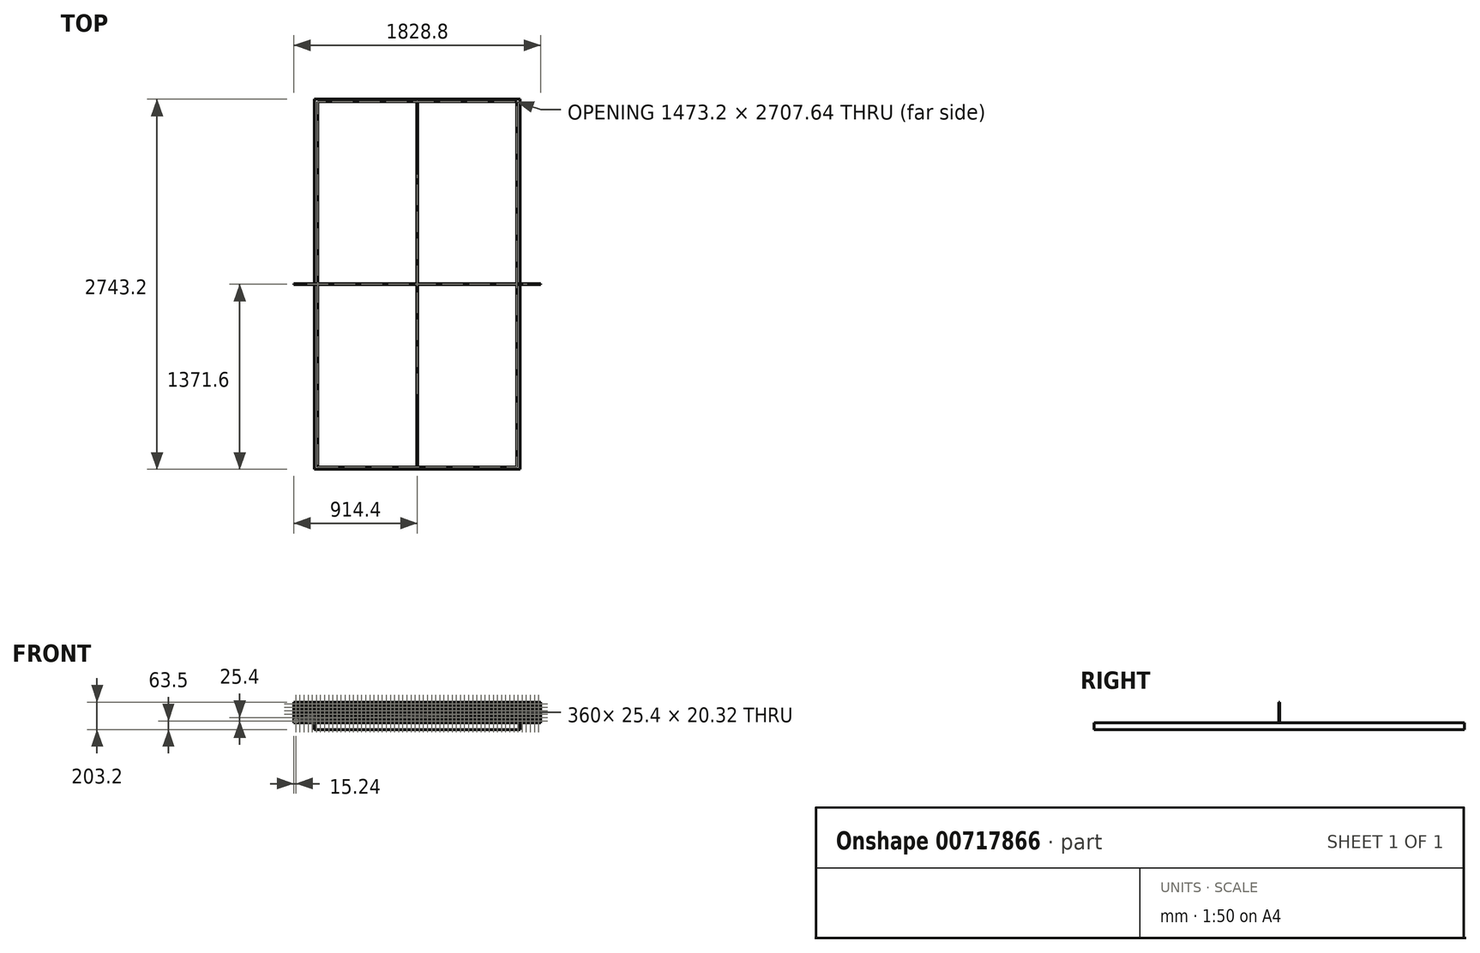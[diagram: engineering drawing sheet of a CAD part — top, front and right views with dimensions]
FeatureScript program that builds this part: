
annotation { "Feature Type Name" : "Feature", "Feature Type Description" : "" }
export const myFeature = defineFeature(function(context is Context, id is Id, definition is map)
    precondition{}
    {
        {
            var Q0;
            Q0=qCreatedBy(makeId("Top.planeOp"),FACE);
            var sketch = newSketch(context, id + "F0", { "sketchPlane" : qUnion([Q0])});
            skLineSegment(sketch, "E0.bottom", {"start": v(762, 1371.6) * mm, "end": v(-762, 1371.6) * mm});
            skLineSegment(sketch, "E0.top", {"start": v(762, -1371.6) * mm, "end": v(-762, -1371.6) * mm});
            skLineSegment(sketch, "E0.left", {"start": v(762, 1371.6) * mm, "end": v(762, -1371.6) * mm});
            skLineSegment(sketch, "E0.right", {"start": v(-762, 1371.6) * mm, "end": v(-762, -1371.6) * mm});
            skPoint(sketch, "E0.middle", {"position": v(0, 0) * mm});
            skSolve(sketch);
        }
        {
            var Q0;
            Q0=makeQuery(id+"F0.imprint","IMPRINT",FACE,{"disambiguationData":[TD([[makeQuery(id+"F0.imprint","IMPRINT",EDGE,{"derivedFrom":sQuery(id+"F0.wireOp",EDGE,"E0.bottom")}),1.0]])]});
            extrude(context, id + "F1", {"entities" : qUnion([Q0]), "endBound" : BoundingType.SYMMETRIC, "depth" : 50.8 * mm, "offsetDistance" : 25.4 * mm});
        }
        {
            var Q0;
            Q0=makeQuery(id+"F1.opExtrude","CAP_FACE",FACE,{"disambiguationData":[OSD([sQuery(id+"F0.wireOp",EDGE,"E0.bottom"),sQuery(id+"F0.wireOp",EDGE,"E0.top"),sQuery(id+"F0.wireOp",EDGE,"E0.left"),sQuery(id+"F0.wireOp",EDGE,"E0.right")])],"isStart":false});
            var sketch = newSketch(context, id + "F2", { "sketchPlane" : qUnion([Q0])});
            skLineSegment(sketch, "E1.bottom", {"start": v(914.4, 3.18) * mm, "end": v(-914.4, 3.18) * mm});
            skLineSegment(sketch, "E1.top", {"start": v(914.4, -3.18) * mm, "end": v(-914.4, -3.18) * mm});
            skLineSegment(sketch, "E1.left", {"start": v(914.4, 3.18) * mm, "end": v(914.4, -3.18) * mm});
            skLineSegment(sketch, "E1.right", {"start": v(-914.4, 3.18) * mm, "end": v(-914.4, -3.18) * mm});
            skPoint(sketch, "E1.middle", {"position": v(0, 0) * mm});
            skSolve(sketch);
        }
        {
            var Q0;
            {var subQ0=sQuery(id+"F2.wireOp",EDGE,"E1.right");Q0=makeQuery(id+"F2.imprint","IMPRINT",FACE,{"disambiguationData":[TD([[makeQuery(id+"F2.imprint","IMPRINT",EDGE,{"derivedFrom":subQ0}),1.0]])]});}
            var Q1;
            {var subQ0=sQuery(id+"F2.wireOp",EDGE,"E1.bottom");var subQ1=makeQuery(id+"F1.opExtrude","CAP_EDGE",EDGE,{"disambiguationData":[OSD([sQuery(id+"F0.wireOp",EDGE,"E0.left")])],"isStart":false});var subQ2=makeQuery(id+"F2.imprint","INTERSECT",VERTEX,{"derivedFrom":[subQ1,subQ0]});Q1=makeQuery(id+"F2.imprint","IMPRINT",FACE,{"disambiguationData":[TD([[makeQuery(id+"F2.imprint","IMPRINT",EDGE,{"disambiguationData":[TD([[subQ2,-1.0]])],"derivedFrom":subQ0}),1.0]])]});}
            var Q2;
            {var subQ0=sQuery(id+"F2.wireOp",EDGE,"E1.left");Q2=makeQuery(id+"F2.imprint","IMPRINT",FACE,{"disambiguationData":[TD([[makeQuery(id+"F2.imprint","IMPRINT",EDGE,{"derivedFrom":subQ0}),-1.0]])]});}
            extrude(context, id + "F3", {"entities" : qUnion([Q0, Q1, Q2]), "operationType" : NewBodyOperationType.ADD, "depth" : 152.4 * mm, "offsetDistance" : 25.4 * mm});
        }
        {
            var Q0;
            Q0=makeQuery(id+"F3.opExtrude","SWEPT_FACE",FACE,{"disambiguationData":[OSD([sQuery(id+"F2.wireOp",EDGE,"E1.top")])]});
            var sketch = newSketch(context, id + "F4", { "sketchPlane" : qUnion([Q0])});
            skLineSegment(sketch, "E2.bottom", {"start": v(-911.86, 175.26) * mm, "end": v(-886.46, 175.26) * mm});
            skLineSegment(sketch, "E2.top", {"start": v(-911.86, 154.94) * mm, "end": v(-886.46, 154.94) * mm});
            skLineSegment(sketch, "E2.left", {"start": v(-911.86, 175.26) * mm, "end": v(-911.86, 154.94) * mm});
            skLineSegment(sketch, "E3.1.0.3", {"start": v(-886.46, 175.26) * mm, "end": v(-886.46, 154.94) * mm});
            skLineSegment(sketch, "E4.1.0.0", {"start": v(-855.98, 175.26) * mm, "end": v(-855.98, 154.94) * mm});
            skLineSegment(sketch, "E4.1.0.1", {"start": v(-881.38, 175.26) * mm, "end": v(-855.98, 175.26) * mm});
            skLineSegment(sketch, "E4.1.0.2", {"start": v(-881.38, 175.26) * mm, "end": v(-881.38, 154.94) * mm});
            skLineSegment(sketch, "E4.1.0.3", {"start": v(-881.38, 154.94) * mm, "end": v(-855.98, 154.94) * mm});
            skLineSegment(sketch, "E4.2.0.0", {"start": v(-825.5, 175.26) * mm, "end": v(-825.5, 154.94) * mm});
            skLineSegment(sketch, "E4.2.0.1", {"start": v(-850.9, 175.26) * mm, "end": v(-825.5, 175.26) * mm});
            skLineSegment(sketch, "E4.2.0.2", {"start": v(-850.9, 175.26) * mm, "end": v(-850.9, 154.94) * mm});
            skLineSegment(sketch, "E4.2.0.3", {"start": v(-850.9, 154.94) * mm, "end": v(-825.5, 154.94) * mm});
            skLineSegment(sketch, "E4.3.0.0", {"start": v(-795.02, 175.26) * mm, "end": v(-795.02, 154.94) * mm});
            skLineSegment(sketch, "E4.3.0.1", {"start": v(-820.42, 175.26) * mm, "end": v(-795.02, 175.26) * mm});
            skLineSegment(sketch, "E4.3.0.2", {"start": v(-820.42, 175.26) * mm, "end": v(-820.42, 154.94) * mm});
            skLineSegment(sketch, "E4.3.0.3", {"start": v(-820.42, 154.94) * mm, "end": v(-795.02, 154.94) * mm});
            skLineSegment(sketch, "E4.4.0.0", {"start": v(-764.54, 175.26) * mm, "end": v(-764.54, 154.94) * mm});
            skLineSegment(sketch, "E4.4.0.1", {"start": v(-789.94, 175.26) * mm, "end": v(-764.54, 175.26) * mm});
            skLineSegment(sketch, "E4.4.0.2", {"start": v(-789.94, 175.26) * mm, "end": v(-789.94, 154.94) * mm});
            skLineSegment(sketch, "E4.4.0.3", {"start": v(-789.94, 154.94) * mm, "end": v(-764.54, 154.94) * mm});
            skLineSegment(sketch, "E4.5.0.0", {"start": v(-734.06, 175.26) * mm, "end": v(-734.06, 154.94) * mm});
            skLineSegment(sketch, "E4.5.0.1", {"start": v(-759.46, 175.26) * mm, "end": v(-734.06, 175.26) * mm});
            skLineSegment(sketch, "E4.5.0.2", {"start": v(-759.46, 175.26) * mm, "end": v(-759.46, 154.94) * mm});
            skLineSegment(sketch, "E4.5.0.3", {"start": v(-759.46, 154.94) * mm, "end": v(-734.06, 154.94) * mm});
            skLineSegment(sketch, "E4.6.0.0", {"start": v(-703.58, 175.26) * mm, "end": v(-703.58, 154.94) * mm});
            skLineSegment(sketch, "E4.6.0.1", {"start": v(-728.98, 175.26) * mm, "end": v(-703.58, 175.26) * mm});
            skLineSegment(sketch, "E4.6.0.2", {"start": v(-728.98, 175.26) * mm, "end": v(-728.98, 154.94) * mm});
            skLineSegment(sketch, "E4.6.0.3", {"start": v(-728.98, 154.94) * mm, "end": v(-703.58, 154.94) * mm});
            skLineSegment(sketch, "E4.7.0.0", {"start": v(-673.1, 175.26) * mm, "end": v(-673.1, 154.94) * mm});
            skLineSegment(sketch, "E4.7.0.1", {"start": v(-698.5, 175.26) * mm, "end": v(-673.1, 175.26) * mm});
            skLineSegment(sketch, "E4.7.0.2", {"start": v(-698.5, 175.26) * mm, "end": v(-698.5, 154.94) * mm});
            skLineSegment(sketch, "E4.7.0.3", {"start": v(-698.5, 154.94) * mm, "end": v(-673.1, 154.94) * mm});
            skLineSegment(sketch, "E4.8.0.0", {"start": v(-642.62, 175.26) * mm, "end": v(-642.62, 154.94) * mm});
            skLineSegment(sketch, "E4.8.0.1", {"start": v(-668.02, 175.26) * mm, "end": v(-642.62, 175.26) * mm});
            skLineSegment(sketch, "E4.8.0.2", {"start": v(-668.02, 175.26) * mm, "end": v(-668.02, 154.94) * mm});
            skLineSegment(sketch, "E4.8.0.3", {"start": v(-668.02, 154.94) * mm, "end": v(-642.62, 154.94) * mm});
            skLineSegment(sketch, "E4.9.0.0", {"start": v(-612.14, 175.26) * mm, "end": v(-612.14, 154.94) * mm});
            skLineSegment(sketch, "E4.9.0.1", {"start": v(-637.54, 175.26) * mm, "end": v(-612.14, 175.26) * mm});
            skLineSegment(sketch, "E4.9.0.2", {"start": v(-637.54, 175.26) * mm, "end": v(-637.54, 154.94) * mm});
            skLineSegment(sketch, "E4.9.0.3", {"start": v(-637.54, 154.94) * mm, "end": v(-612.14, 154.94) * mm});
            skLineSegment(sketch, "E4.10.0.0", {"start": v(-581.66, 175.26) * mm, "end": v(-581.66, 154.94) * mm});
            skLineSegment(sketch, "E4.10.0.1", {"start": v(-607.06, 175.26) * mm, "end": v(-581.66, 175.26) * mm});
            skLineSegment(sketch, "E4.10.0.2", {"start": v(-607.06, 175.26) * mm, "end": v(-607.06, 154.94) * mm});
            skLineSegment(sketch, "E4.10.0.3", {"start": v(-607.06, 154.94) * mm, "end": v(-581.66, 154.94) * mm});
            skLineSegment(sketch, "E4.11.0.0", {"start": v(-551.18, 175.26) * mm, "end": v(-551.18, 154.94) * mm});
            skLineSegment(sketch, "E4.11.0.1", {"start": v(-576.58, 175.26) * mm, "end": v(-551.18, 175.26) * mm});
            skLineSegment(sketch, "E4.11.0.2", {"start": v(-576.58, 175.26) * mm, "end": v(-576.58, 154.94) * mm});
            skLineSegment(sketch, "E4.11.0.3", {"start": v(-576.58, 154.94) * mm, "end": v(-551.18, 154.94) * mm});
            skLineSegment(sketch, "E4.12.0.0", {"start": v(-520.7, 175.26) * mm, "end": v(-520.7, 154.94) * mm});
            skLineSegment(sketch, "E4.12.0.1", {"start": v(-546.1, 175.26) * mm, "end": v(-520.7, 175.26) * mm});
            skLineSegment(sketch, "E4.12.0.2", {"start": v(-546.1, 175.26) * mm, "end": v(-546.1, 154.94) * mm});
            skLineSegment(sketch, "E4.12.0.3", {"start": v(-546.1, 154.94) * mm, "end": v(-520.7, 154.94) * mm});
            skLineSegment(sketch, "E4.13.0.0", {"start": v(-490.22, 175.26) * mm, "end": v(-490.22, 154.94) * mm});
            skLineSegment(sketch, "E4.13.0.1", {"start": v(-515.62, 175.26) * mm, "end": v(-490.22, 175.26) * mm});
            skLineSegment(sketch, "E4.13.0.2", {"start": v(-515.62, 175.26) * mm, "end": v(-515.62, 154.94) * mm});
            skLineSegment(sketch, "E4.13.0.3", {"start": v(-515.62, 154.94) * mm, "end": v(-490.22, 154.94) * mm});
            skLineSegment(sketch, "E4.14.0.0", {"start": v(-459.74, 175.26) * mm, "end": v(-459.74, 154.94) * mm});
            skLineSegment(sketch, "E4.14.0.1", {"start": v(-485.14, 175.26) * mm, "end": v(-459.74, 175.26) * mm});
            skLineSegment(sketch, "E4.14.0.2", {"start": v(-485.14, 175.26) * mm, "end": v(-485.14, 154.94) * mm});
            skLineSegment(sketch, "E4.14.0.3", {"start": v(-485.14, 154.94) * mm, "end": v(-459.74, 154.94) * mm});
            skLineSegment(sketch, "E4.15.0.0", {"start": v(-429.26, 175.26) * mm, "end": v(-429.26, 154.94) * mm});
            skLineSegment(sketch, "E4.15.0.1", {"start": v(-454.66, 175.26) * mm, "end": v(-429.26, 175.26) * mm});
            skLineSegment(sketch, "E4.15.0.2", {"start": v(-454.66, 175.26) * mm, "end": v(-454.66, 154.94) * mm});
            skLineSegment(sketch, "E4.15.0.3", {"start": v(-454.66, 154.94) * mm, "end": v(-429.26, 154.94) * mm});
            skLineSegment(sketch, "E4.16.0.0", {"start": v(-398.78, 175.26) * mm, "end": v(-398.78, 154.94) * mm});
            skLineSegment(sketch, "E4.16.0.1", {"start": v(-424.18, 175.26) * mm, "end": v(-398.78, 175.26) * mm});
            skLineSegment(sketch, "E4.16.0.2", {"start": v(-424.18, 175.26) * mm, "end": v(-424.18, 154.94) * mm});
            skLineSegment(sketch, "E4.16.0.3", {"start": v(-424.18, 154.94) * mm, "end": v(-398.78, 154.94) * mm});
            skLineSegment(sketch, "E4.17.0.0", {"start": v(-368.3, 175.26) * mm, "end": v(-368.3, 154.94) * mm});
            skLineSegment(sketch, "E4.17.0.1", {"start": v(-393.7, 175.26) * mm, "end": v(-368.3, 175.26) * mm});
            skLineSegment(sketch, "E4.17.0.2", {"start": v(-393.7, 175.26) * mm, "end": v(-393.7, 154.94) * mm});
            skLineSegment(sketch, "E4.17.0.3", {"start": v(-393.7, 154.94) * mm, "end": v(-368.3, 154.94) * mm});
            skLineSegment(sketch, "E4.18.0.0", {"start": v(-337.82, 175.26) * mm, "end": v(-337.82, 154.94) * mm});
            skLineSegment(sketch, "E4.18.0.1", {"start": v(-363.22, 175.26) * mm, "end": v(-337.82, 175.26) * mm});
            skLineSegment(sketch, "E4.18.0.2", {"start": v(-363.22, 175.26) * mm, "end": v(-363.22, 154.94) * mm});
            skLineSegment(sketch, "E4.18.0.3", {"start": v(-363.22, 154.94) * mm, "end": v(-337.82, 154.94) * mm});
            skLineSegment(sketch, "E4.19.0.0", {"start": v(-307.34, 175.26) * mm, "end": v(-307.34, 154.94) * mm});
            skLineSegment(sketch, "E4.19.0.1", {"start": v(-332.74, 175.26) * mm, "end": v(-307.34, 175.26) * mm});
            skLineSegment(sketch, "E4.19.0.2", {"start": v(-332.74, 175.26) * mm, "end": v(-332.74, 154.94) * mm});
            skLineSegment(sketch, "E4.19.0.3", {"start": v(-332.74, 154.94) * mm, "end": v(-307.34, 154.94) * mm});
            skLineSegment(sketch, "E4.20.0.0", {"start": v(-276.86, 175.26) * mm, "end": v(-276.86, 154.94) * mm});
            skLineSegment(sketch, "E4.20.0.1", {"start": v(-302.26, 175.26) * mm, "end": v(-276.86, 175.26) * mm});
            skLineSegment(sketch, "E4.20.0.2", {"start": v(-302.26, 175.26) * mm, "end": v(-302.26, 154.94) * mm});
            skLineSegment(sketch, "E4.20.0.3", {"start": v(-302.26, 154.94) * mm, "end": v(-276.86, 154.94) * mm});
            skLineSegment(sketch, "E4.21.0.0", {"start": v(-246.38, 175.26) * mm, "end": v(-246.38, 154.94) * mm});
            skLineSegment(sketch, "E4.21.0.1", {"start": v(-271.78, 175.26) * mm, "end": v(-246.38, 175.26) * mm});
            skLineSegment(sketch, "E4.21.0.2", {"start": v(-271.78, 175.26) * mm, "end": v(-271.78, 154.94) * mm});
            skLineSegment(sketch, "E4.21.0.3", {"start": v(-271.78, 154.94) * mm, "end": v(-246.38, 154.94) * mm});
            skLineSegment(sketch, "E4.22.0.0", {"start": v(-215.9, 175.26) * mm, "end": v(-215.9, 154.94) * mm});
            skLineSegment(sketch, "E4.22.0.1", {"start": v(-241.3, 175.26) * mm, "end": v(-215.9, 175.26) * mm});
            skLineSegment(sketch, "E4.22.0.2", {"start": v(-241.3, 175.26) * mm, "end": v(-241.3, 154.94) * mm});
            skLineSegment(sketch, "E4.22.0.3", {"start": v(-241.3, 154.94) * mm, "end": v(-215.9, 154.94) * mm});
            skLineSegment(sketch, "E4.23.0.0", {"start": v(-185.42, 175.26) * mm, "end": v(-185.42, 154.94) * mm});
            skLineSegment(sketch, "E4.23.0.1", {"start": v(-210.82, 175.26) * mm, "end": v(-185.42, 175.26) * mm});
            skLineSegment(sketch, "E4.23.0.2", {"start": v(-210.82, 175.26) * mm, "end": v(-210.82, 154.94) * mm});
            skLineSegment(sketch, "E4.23.0.3", {"start": v(-210.82, 154.94) * mm, "end": v(-185.42, 154.94) * mm});
            skLineSegment(sketch, "E4.24.0.0", {"start": v(-154.94, 175.26) * mm, "end": v(-154.94, 154.94) * mm});
            skLineSegment(sketch, "E4.24.0.1", {"start": v(-180.34, 175.26) * mm, "end": v(-154.94, 175.26) * mm});
            skLineSegment(sketch, "E4.24.0.2", {"start": v(-180.34, 175.26) * mm, "end": v(-180.34, 154.94) * mm});
            skLineSegment(sketch, "E4.24.0.3", {"start": v(-180.34, 154.94) * mm, "end": v(-154.94, 154.94) * mm});
            skLineSegment(sketch, "E4.25.0.0", {"start": v(-124.46, 175.26) * mm, "end": v(-124.46, 154.94) * mm});
            skLineSegment(sketch, "E4.25.0.1", {"start": v(-149.86, 175.26) * mm, "end": v(-124.46, 175.26) * mm});
            skLineSegment(sketch, "E4.25.0.2", {"start": v(-149.86, 175.26) * mm, "end": v(-149.86, 154.94) * mm});
            skLineSegment(sketch, "E4.25.0.3", {"start": v(-149.86, 154.94) * mm, "end": v(-124.46, 154.94) * mm});
            skLineSegment(sketch, "E4.26.0.0", {"start": v(-93.98, 175.26) * mm, "end": v(-93.98, 154.94) * mm});
            skLineSegment(sketch, "E4.26.0.1", {"start": v(-119.38, 175.26) * mm, "end": v(-93.98, 175.26) * mm});
            skLineSegment(sketch, "E4.26.0.2", {"start": v(-119.38, 175.26) * mm, "end": v(-119.38, 154.94) * mm});
            skLineSegment(sketch, "E4.26.0.3", {"start": v(-119.38, 154.94) * mm, "end": v(-93.98, 154.94) * mm});
            skLineSegment(sketch, "E4.27.0.0", {"start": v(-63.5, 175.26) * mm, "end": v(-63.5, 154.94) * mm});
            skLineSegment(sketch, "E4.27.0.1", {"start": v(-88.9, 175.26) * mm, "end": v(-63.5, 175.26) * mm});
            skLineSegment(sketch, "E4.27.0.2", {"start": v(-88.9, 175.26) * mm, "end": v(-88.9, 154.94) * mm});
            skLineSegment(sketch, "E4.27.0.3", {"start": v(-88.9, 154.94) * mm, "end": v(-63.5, 154.94) * mm});
            skLineSegment(sketch, "E4.28.0.0", {"start": v(-33.02, 175.26) * mm, "end": v(-33.02, 154.94) * mm});
            skLineSegment(sketch, "E4.28.0.1", {"start": v(-58.42, 175.26) * mm, "end": v(-33.02, 175.26) * mm});
            skLineSegment(sketch, "E4.28.0.2", {"start": v(-58.42, 175.26) * mm, "end": v(-58.42, 154.94) * mm});
            skLineSegment(sketch, "E4.28.0.3", {"start": v(-58.42, 154.94) * mm, "end": v(-33.02, 154.94) * mm});
            skLineSegment(sketch, "E4.29.0.0", {"start": v(-2.54, 175.26) * mm, "end": v(-2.54, 154.94) * mm});
            skLineSegment(sketch, "E4.29.0.1", {"start": v(-27.94, 175.26) * mm, "end": v(-2.54, 175.26) * mm});
            skLineSegment(sketch, "E4.29.0.2", {"start": v(-27.94, 175.26) * mm, "end": v(-27.94, 154.94) * mm});
            skLineSegment(sketch, "E4.29.0.3", {"start": v(-27.94, 154.94) * mm, "end": v(-2.54, 154.94) * mm});
            skLineSegment(sketch, "E4.30.0.0", {"start": v(27.94, 175.26) * mm, "end": v(27.94, 154.94) * mm});
            skLineSegment(sketch, "E4.30.0.1", {"start": v(2.54, 175.26) * mm, "end": v(27.94, 175.26) * mm});
            skLineSegment(sketch, "E4.30.0.2", {"start": v(2.54, 175.26) * mm, "end": v(2.54, 154.94) * mm});
            skLineSegment(sketch, "E4.30.0.3", {"start": v(2.54, 154.94) * mm, "end": v(27.94, 154.94) * mm});
            skLineSegment(sketch, "E4.31.0.0", {"start": v(58.42, 175.26) * mm, "end": v(58.42, 154.94) * mm});
            skLineSegment(sketch, "E4.31.0.1", {"start": v(33.02, 175.26) * mm, "end": v(58.42, 175.26) * mm});
            skLineSegment(sketch, "E4.31.0.2", {"start": v(33.02, 175.26) * mm, "end": v(33.02, 154.94) * mm});
            skLineSegment(sketch, "E4.31.0.3", {"start": v(33.02, 154.94) * mm, "end": v(58.42, 154.94) * mm});
            skLineSegment(sketch, "E4.32.0.0", {"start": v(88.9, 175.26) * mm, "end": v(88.9, 154.94) * mm});
            skLineSegment(sketch, "E4.32.0.1", {"start": v(63.5, 175.26) * mm, "end": v(88.9, 175.26) * mm});
            skLineSegment(sketch, "E4.32.0.2", {"start": v(63.5, 175.26) * mm, "end": v(63.5, 154.94) * mm});
            skLineSegment(sketch, "E4.32.0.3", {"start": v(63.5, 154.94) * mm, "end": v(88.9, 154.94) * mm});
            skLineSegment(sketch, "E4.33.0.0", {"start": v(119.38, 175.26) * mm, "end": v(119.38, 154.94) * mm});
            skLineSegment(sketch, "E4.33.0.1", {"start": v(93.98, 175.26) * mm, "end": v(119.38, 175.26) * mm});
            skLineSegment(sketch, "E4.33.0.2", {"start": v(93.98, 175.26) * mm, "end": v(93.98, 154.94) * mm});
            skLineSegment(sketch, "E4.33.0.3", {"start": v(93.98, 154.94) * mm, "end": v(119.38, 154.94) * mm});
            skLineSegment(sketch, "E4.34.0.0", {"start": v(149.86, 175.26) * mm, "end": v(149.86, 154.94) * mm});
            skLineSegment(sketch, "E4.34.0.1", {"start": v(124.46, 175.26) * mm, "end": v(149.86, 175.26) * mm});
            skLineSegment(sketch, "E4.34.0.2", {"start": v(124.46, 175.26) * mm, "end": v(124.46, 154.94) * mm});
            skLineSegment(sketch, "E4.34.0.3", {"start": v(124.46, 154.94) * mm, "end": v(149.86, 154.94) * mm});
            skLineSegment(sketch, "E4.35.0.0", {"start": v(180.34, 175.26) * mm, "end": v(180.34, 154.94) * mm});
            skLineSegment(sketch, "E4.35.0.1", {"start": v(154.94, 175.26) * mm, "end": v(180.34, 175.26) * mm});
            skLineSegment(sketch, "E4.35.0.2", {"start": v(154.94, 175.26) * mm, "end": v(154.94, 154.94) * mm});
            skLineSegment(sketch, "E4.35.0.3", {"start": v(154.94, 154.94) * mm, "end": v(180.34, 154.94) * mm});
            skLineSegment(sketch, "E4.36.0.0", {"start": v(210.82, 175.26) * mm, "end": v(210.82, 154.94) * mm});
            skLineSegment(sketch, "E4.36.0.1", {"start": v(185.42, 175.26) * mm, "end": v(210.82, 175.26) * mm});
            skLineSegment(sketch, "E4.36.0.2", {"start": v(185.42, 175.26) * mm, "end": v(185.42, 154.94) * mm});
            skLineSegment(sketch, "E4.36.0.3", {"start": v(185.42, 154.94) * mm, "end": v(210.82, 154.94) * mm});
            skLineSegment(sketch, "E4.37.0.0", {"start": v(241.3, 175.26) * mm, "end": v(241.3, 154.94) * mm});
            skLineSegment(sketch, "E4.37.0.1", {"start": v(215.9, 175.26) * mm, "end": v(241.3, 175.26) * mm});
            skLineSegment(sketch, "E4.37.0.2", {"start": v(215.9, 175.26) * mm, "end": v(215.9, 154.94) * mm});
            skLineSegment(sketch, "E4.37.0.3", {"start": v(215.9, 154.94) * mm, "end": v(241.3, 154.94) * mm});
            skLineSegment(sketch, "E4.38.0.0", {"start": v(271.78, 175.26) * mm, "end": v(271.78, 154.94) * mm});
            skLineSegment(sketch, "E4.38.0.1", {"start": v(246.38, 175.26) * mm, "end": v(271.78, 175.26) * mm});
            skLineSegment(sketch, "E4.38.0.2", {"start": v(246.38, 175.26) * mm, "end": v(246.38, 154.94) * mm});
            skLineSegment(sketch, "E4.38.0.3", {"start": v(246.38, 154.94) * mm, "end": v(271.78, 154.94) * mm});
            skLineSegment(sketch, "E4.39.0.0", {"start": v(302.26, 175.26) * mm, "end": v(302.26, 154.94) * mm});
            skLineSegment(sketch, "E4.39.0.1", {"start": v(276.86, 175.26) * mm, "end": v(302.26, 175.26) * mm});
            skLineSegment(sketch, "E4.39.0.2", {"start": v(276.86, 175.26) * mm, "end": v(276.86, 154.94) * mm});
            skLineSegment(sketch, "E4.39.0.3", {"start": v(276.86, 154.94) * mm, "end": v(302.26, 154.94) * mm});
            skLineSegment(sketch, "E4.40.0.0", {"start": v(332.74, 175.26) * mm, "end": v(332.74, 154.94) * mm});
            skLineSegment(sketch, "E4.40.0.1", {"start": v(307.34, 175.26) * mm, "end": v(332.74, 175.26) * mm});
            skLineSegment(sketch, "E4.40.0.2", {"start": v(307.34, 175.26) * mm, "end": v(307.34, 154.94) * mm});
            skLineSegment(sketch, "E4.40.0.3", {"start": v(307.34, 154.94) * mm, "end": v(332.74, 154.94) * mm});
            skLineSegment(sketch, "E4.41.0.0", {"start": v(363.22, 175.26) * mm, "end": v(363.22, 154.94) * mm});
            skLineSegment(sketch, "E4.41.0.1", {"start": v(337.82, 175.26) * mm, "end": v(363.22, 175.26) * mm});
            skLineSegment(sketch, "E4.41.0.2", {"start": v(337.82, 175.26) * mm, "end": v(337.82, 154.94) * mm});
            skLineSegment(sketch, "E4.41.0.3", {"start": v(337.82, 154.94) * mm, "end": v(363.22, 154.94) * mm});
            skLineSegment(sketch, "E4.42.0.0", {"start": v(393.7, 175.26) * mm, "end": v(393.7, 154.94) * mm});
            skLineSegment(sketch, "E4.42.0.1", {"start": v(368.3, 175.26) * mm, "end": v(393.7, 175.26) * mm});
            skLineSegment(sketch, "E4.42.0.2", {"start": v(368.3, 175.26) * mm, "end": v(368.3, 154.94) * mm});
            skLineSegment(sketch, "E4.42.0.3", {"start": v(368.3, 154.94) * mm, "end": v(393.7, 154.94) * mm});
            skLineSegment(sketch, "E4.43.0.0", {"start": v(424.18, 175.26) * mm, "end": v(424.18, 154.94) * mm});
            skLineSegment(sketch, "E4.43.0.1", {"start": v(398.78, 175.26) * mm, "end": v(424.18, 175.26) * mm});
            skLineSegment(sketch, "E4.43.0.2", {"start": v(398.78, 175.26) * mm, "end": v(398.78, 154.94) * mm});
            skLineSegment(sketch, "E4.43.0.3", {"start": v(398.78, 154.94) * mm, "end": v(424.18, 154.94) * mm});
            skLineSegment(sketch, "E4.44.0.0", {"start": v(454.66, 175.26) * mm, "end": v(454.66, 154.94) * mm});
            skLineSegment(sketch, "E4.44.0.1", {"start": v(429.26, 175.26) * mm, "end": v(454.66, 175.26) * mm});
            skLineSegment(sketch, "E4.44.0.2", {"start": v(429.26, 175.26) * mm, "end": v(429.26, 154.94) * mm});
            skLineSegment(sketch, "E4.44.0.3", {"start": v(429.26, 154.94) * mm, "end": v(454.66, 154.94) * mm});
            skLineSegment(sketch, "E4.45.0.0", {"start": v(485.14, 175.26) * mm, "end": v(485.14, 154.94) * mm});
            skLineSegment(sketch, "E4.45.0.1", {"start": v(459.74, 175.26) * mm, "end": v(485.14, 175.26) * mm});
            skLineSegment(sketch, "E4.45.0.2", {"start": v(459.74, 175.26) * mm, "end": v(459.74, 154.94) * mm});
            skLineSegment(sketch, "E4.45.0.3", {"start": v(459.74, 154.94) * mm, "end": v(485.14, 154.94) * mm});
            skLineSegment(sketch, "E4.46.0.0", {"start": v(515.62, 175.26) * mm, "end": v(515.62, 154.94) * mm});
            skLineSegment(sketch, "E4.46.0.1", {"start": v(490.22, 175.26) * mm, "end": v(515.62, 175.26) * mm});
            skLineSegment(sketch, "E4.46.0.2", {"start": v(490.22, 175.26) * mm, "end": v(490.22, 154.94) * mm});
            skLineSegment(sketch, "E4.46.0.3", {"start": v(490.22, 154.94) * mm, "end": v(515.62, 154.94) * mm});
            skLineSegment(sketch, "E4.47.0.0", {"start": v(546.1, 175.26) * mm, "end": v(546.1, 154.94) * mm});
            skLineSegment(sketch, "E4.47.0.1", {"start": v(520.7, 175.26) * mm, "end": v(546.1, 175.26) * mm});
            skLineSegment(sketch, "E4.47.0.2", {"start": v(520.7, 175.26) * mm, "end": v(520.7, 154.94) * mm});
            skLineSegment(sketch, "E4.47.0.3", {"start": v(520.7, 154.94) * mm, "end": v(546.1, 154.94) * mm});
            skLineSegment(sketch, "E4.48.0.0", {"start": v(576.58, 175.26) * mm, "end": v(576.58, 154.94) * mm});
            skLineSegment(sketch, "E4.48.0.1", {"start": v(551.18, 175.26) * mm, "end": v(576.58, 175.26) * mm});
            skLineSegment(sketch, "E4.48.0.2", {"start": v(551.18, 175.26) * mm, "end": v(551.18, 154.94) * mm});
            skLineSegment(sketch, "E4.48.0.3", {"start": v(551.18, 154.94) * mm, "end": v(576.58, 154.94) * mm});
            skLineSegment(sketch, "E4.49.0.0", {"start": v(607.06, 175.26) * mm, "end": v(607.06, 154.94) * mm});
            skLineSegment(sketch, "E4.49.0.1", {"start": v(581.66, 175.26) * mm, "end": v(607.06, 175.26) * mm});
            skLineSegment(sketch, "E4.49.0.2", {"start": v(581.66, 175.26) * mm, "end": v(581.66, 154.94) * mm});
            skLineSegment(sketch, "E4.49.0.3", {"start": v(581.66, 154.94) * mm, "end": v(607.06, 154.94) * mm});
            skLineSegment(sketch, "E4.50.0.0", {"start": v(637.54, 175.26) * mm, "end": v(637.54, 154.94) * mm});
            skLineSegment(sketch, "E4.50.0.1", {"start": v(612.14, 175.26) * mm, "end": v(637.54, 175.26) * mm});
            skLineSegment(sketch, "E4.50.0.2", {"start": v(612.14, 175.26) * mm, "end": v(612.14, 154.94) * mm});
            skLineSegment(sketch, "E4.50.0.3", {"start": v(612.14, 154.94) * mm, "end": v(637.54, 154.94) * mm});
            skLineSegment(sketch, "E4.51.0.0", {"start": v(668.02, 175.26) * mm, "end": v(668.02, 154.94) * mm});
            skLineSegment(sketch, "E4.51.0.1", {"start": v(642.62, 175.26) * mm, "end": v(668.02, 175.26) * mm});
            skLineSegment(sketch, "E4.51.0.2", {"start": v(642.62, 175.26) * mm, "end": v(642.62, 154.94) * mm});
            skLineSegment(sketch, "E4.51.0.3", {"start": v(642.62, 154.94) * mm, "end": v(668.02, 154.94) * mm});
            skLineSegment(sketch, "E4.52.0.0", {"start": v(698.5, 175.26) * mm, "end": v(698.5, 154.94) * mm});
            skLineSegment(sketch, "E4.52.0.1", {"start": v(673.1, 175.26) * mm, "end": v(698.5, 175.26) * mm});
            skLineSegment(sketch, "E4.52.0.2", {"start": v(673.1, 175.26) * mm, "end": v(673.1, 154.94) * mm});
            skLineSegment(sketch, "E4.52.0.3", {"start": v(673.1, 154.94) * mm, "end": v(698.5, 154.94) * mm});
            skLineSegment(sketch, "E4.53.0.0", {"start": v(728.98, 175.26) * mm, "end": v(728.98, 154.94) * mm});
            skLineSegment(sketch, "E4.53.0.1", {"start": v(703.58, 175.26) * mm, "end": v(728.98, 175.26) * mm});
            skLineSegment(sketch, "E4.53.0.2", {"start": v(703.58, 175.26) * mm, "end": v(703.58, 154.94) * mm});
            skLineSegment(sketch, "E4.53.0.3", {"start": v(703.58, 154.94) * mm, "end": v(728.98, 154.94) * mm});
            skLineSegment(sketch, "E4.54.0.0", {"start": v(759.46, 175.26) * mm, "end": v(759.46, 154.94) * mm});
            skLineSegment(sketch, "E4.54.0.1", {"start": v(734.06, 175.26) * mm, "end": v(759.46, 175.26) * mm});
            skLineSegment(sketch, "E4.54.0.2", {"start": v(734.06, 175.26) * mm, "end": v(734.06, 154.94) * mm});
            skLineSegment(sketch, "E4.54.0.3", {"start": v(734.06, 154.94) * mm, "end": v(759.46, 154.94) * mm});
            skLineSegment(sketch, "E4.55.0.0", {"start": v(789.94, 175.26) * mm, "end": v(789.94, 154.94) * mm});
            skLineSegment(sketch, "E4.55.0.1", {"start": v(764.54, 175.26) * mm, "end": v(789.94, 175.26) * mm});
            skLineSegment(sketch, "E4.55.0.2", {"start": v(764.54, 175.26) * mm, "end": v(764.54, 154.94) * mm});
            skLineSegment(sketch, "E4.55.0.3", {"start": v(764.54, 154.94) * mm, "end": v(789.94, 154.94) * mm});
            skLineSegment(sketch, "E4.56.0.0", {"start": v(820.42, 175.26) * mm, "end": v(820.42, 154.94) * mm});
            skLineSegment(sketch, "E4.56.0.1", {"start": v(795.02, 175.26) * mm, "end": v(820.42, 175.26) * mm});
            skLineSegment(sketch, "E4.56.0.2", {"start": v(795.02, 175.26) * mm, "end": v(795.02, 154.94) * mm});
            skLineSegment(sketch, "E4.56.0.3", {"start": v(795.02, 154.94) * mm, "end": v(820.42, 154.94) * mm});
            skLineSegment(sketch, "E4.57.0.0", {"start": v(850.9, 175.26) * mm, "end": v(850.9, 154.94) * mm});
            skLineSegment(sketch, "E4.57.0.1", {"start": v(825.5, 175.26) * mm, "end": v(850.9, 175.26) * mm});
            skLineSegment(sketch, "E4.57.0.2", {"start": v(825.5, 175.26) * mm, "end": v(825.5, 154.94) * mm});
            skLineSegment(sketch, "E4.57.0.3", {"start": v(825.5, 154.94) * mm, "end": v(850.9, 154.94) * mm});
            skLineSegment(sketch, "E4.58.0.0", {"start": v(881.38, 175.26) * mm, "end": v(881.38, 154.94) * mm});
            skLineSegment(sketch, "E4.58.0.1", {"start": v(855.98, 175.26) * mm, "end": v(881.38, 175.26) * mm});
            skLineSegment(sketch, "E4.58.0.2", {"start": v(855.98, 175.26) * mm, "end": v(855.98, 154.94) * mm});
            skLineSegment(sketch, "E4.58.0.3", {"start": v(855.98, 154.94) * mm, "end": v(881.38, 154.94) * mm});
            skLineSegment(sketch, "E4.59.0.0", {"start": v(911.86, 175.26) * mm, "end": v(911.86, 154.94) * mm});
            skLineSegment(sketch, "E4.59.0.1", {"start": v(886.46, 175.26) * mm, "end": v(911.86, 175.26) * mm});
            skLineSegment(sketch, "E4.59.0.2", {"start": v(886.46, 175.26) * mm, "end": v(886.46, 154.94) * mm});
            skLineSegment(sketch, "E4.59.0.3", {"start": v(886.46, 154.94) * mm, "end": v(911.86, 154.94) * mm});
            skLineSegment(sketch, "E4.direction1", {"start": v(-886.46, 154.94) * mm, "end": v(-855.98, 154.94) * mm, "construction": true});
            skLineSegment(sketch, "E5.0.1.0", {"start": v(886.46, 129.54) * mm, "end": v(911.86, 129.54) * mm});
            skLineSegment(sketch, "E5.0.1.1", {"start": v(911.86, 149.86) * mm, "end": v(911.86, 129.54) * mm});
            skLineSegment(sketch, "E5.0.1.2", {"start": v(886.46, 149.86) * mm, "end": v(911.86, 149.86) * mm});
            skLineSegment(sketch, "E5.0.1.3", {"start": v(886.46, 149.86) * mm, "end": v(886.46, 129.54) * mm});
            skLineSegment(sketch, "E5.0.1.4", {"start": v(881.38, 149.86) * mm, "end": v(881.38, 129.54) * mm});
            skLineSegment(sketch, "E5.0.1.5", {"start": v(855.98, 149.86) * mm, "end": v(881.38, 149.86) * mm});
            skLineSegment(sketch, "E5.0.1.6", {"start": v(855.98, 129.54) * mm, "end": v(881.38, 129.54) * mm});
            skLineSegment(sketch, "E5.0.1.7", {"start": v(855.98, 149.86) * mm, "end": v(855.98, 129.54) * mm});
            skLineSegment(sketch, "E5.0.1.8", {"start": v(520.7, 129.54) * mm, "end": v(546.1, 129.54) * mm});
            skLineSegment(sketch, "E5.0.1.9", {"start": v(398.78, 129.54) * mm, "end": v(424.18, 129.54) * mm});
            skLineSegment(sketch, "E5.0.1.10", {"start": v(820.42, 149.86) * mm, "end": v(820.42, 129.54) * mm});
            skLineSegment(sketch, "E5.0.1.11", {"start": v(642.62, 129.54) * mm, "end": v(668.02, 129.54) * mm});
            skLineSegment(sketch, "E5.0.1.12", {"start": v(764.54, 129.54) * mm, "end": v(789.94, 129.54) * mm});
            skLineSegment(sketch, "E5.0.1.13", {"start": v(698.5, 149.86) * mm, "end": v(698.5, 129.54) * mm});
            skLineSegment(sketch, "E5.0.1.14", {"start": v(576.58, 149.86) * mm, "end": v(576.58, 129.54) * mm});
            skLineSegment(sketch, "E5.0.1.15", {"start": v(454.66, 149.86) * mm, "end": v(454.66, 129.54) * mm});
            skLineSegment(sketch, "E5.0.1.16", {"start": v(795.02, 149.86) * mm, "end": v(820.42, 149.86) * mm});
            skLineSegment(sketch, "E5.0.1.17", {"start": v(673.1, 149.86) * mm, "end": v(698.5, 149.86) * mm});
            skLineSegment(sketch, "E5.0.1.18", {"start": v(551.18, 149.86) * mm, "end": v(576.58, 149.86) * mm});
            skLineSegment(sketch, "E5.0.1.19", {"start": v(429.26, 149.86) * mm, "end": v(454.66, 149.86) * mm});
            skLineSegment(sketch, "E5.0.1.20", {"start": v(795.02, 149.86) * mm, "end": v(795.02, 129.54) * mm});
            skLineSegment(sketch, "E5.0.1.21", {"start": v(673.1, 149.86) * mm, "end": v(673.1, 129.54) * mm});
            skLineSegment(sketch, "E5.0.1.22", {"start": v(551.18, 149.86) * mm, "end": v(551.18, 129.54) * mm});
            skLineSegment(sketch, "E5.0.1.23", {"start": v(429.26, 149.86) * mm, "end": v(429.26, 129.54) * mm});
            skLineSegment(sketch, "E5.0.1.24", {"start": v(795.02, 129.54) * mm, "end": v(820.42, 129.54) * mm});
            skLineSegment(sketch, "E5.0.1.25", {"start": v(673.1, 129.54) * mm, "end": v(698.5, 129.54) * mm});
            skLineSegment(sketch, "E5.0.1.26", {"start": v(551.18, 129.54) * mm, "end": v(576.58, 129.54) * mm});
            skLineSegment(sketch, "E5.0.1.27", {"start": v(429.26, 129.54) * mm, "end": v(454.66, 129.54) * mm});
            skLineSegment(sketch, "E5.0.1.28", {"start": v(850.9, 149.86) * mm, "end": v(850.9, 129.54) * mm});
            skLineSegment(sketch, "E5.0.1.29", {"start": v(728.98, 149.86) * mm, "end": v(728.98, 129.54) * mm});
            skLineSegment(sketch, "E5.0.1.30", {"start": v(607.06, 149.86) * mm, "end": v(607.06, 129.54) * mm});
            skLineSegment(sketch, "E5.0.1.31", {"start": v(485.14, 149.86) * mm, "end": v(485.14, 129.54) * mm});
            skLineSegment(sketch, "E5.0.1.32", {"start": v(825.5, 149.86) * mm, "end": v(850.9, 149.86) * mm});
            skLineSegment(sketch, "E5.0.1.33", {"start": v(703.58, 149.86) * mm, "end": v(728.98, 149.86) * mm});
            skLineSegment(sketch, "E5.0.1.34", {"start": v(581.66, 149.86) * mm, "end": v(607.06, 149.86) * mm});
            skLineSegment(sketch, "E5.0.1.35", {"start": v(459.74, 149.86) * mm, "end": v(485.14, 149.86) * mm});
            skLineSegment(sketch, "E5.0.1.36", {"start": v(825.5, 149.86) * mm, "end": v(825.5, 129.54) * mm});
            skLineSegment(sketch, "E5.0.1.37", {"start": v(703.58, 149.86) * mm, "end": v(703.58, 129.54) * mm});
            skLineSegment(sketch, "E5.0.1.38", {"start": v(581.66, 149.86) * mm, "end": v(581.66, 129.54) * mm});
            skLineSegment(sketch, "E5.0.1.39", {"start": v(459.74, 149.86) * mm, "end": v(459.74, 129.54) * mm});
            skLineSegment(sketch, "E5.0.1.40", {"start": v(581.66, 129.54) * mm, "end": v(607.06, 129.54) * mm});
            skLineSegment(sketch, "E5.0.1.41", {"start": v(459.74, 129.54) * mm, "end": v(485.14, 129.54) * mm});
            skLineSegment(sketch, "E5.0.1.42", {"start": v(825.5, 129.54) * mm, "end": v(850.9, 129.54) * mm});
            skLineSegment(sketch, "E5.0.1.43", {"start": v(703.58, 129.54) * mm, "end": v(728.98, 129.54) * mm});
            skLineSegment(sketch, "E5.0.1.44", {"start": v(637.54, 149.86) * mm, "end": v(637.54, 129.54) * mm});
            skLineSegment(sketch, "E5.0.1.45", {"start": v(515.62, 149.86) * mm, "end": v(515.62, 129.54) * mm});
            skLineSegment(sketch, "E5.0.1.46", {"start": v(393.7, 149.86) * mm, "end": v(393.7, 129.54) * mm});
            skLineSegment(sketch, "E5.0.1.47", {"start": v(759.46, 149.86) * mm, "end": v(759.46, 129.54) * mm});
            skLineSegment(sketch, "E5.0.1.48", {"start": v(612.14, 149.86) * mm, "end": v(637.54, 149.86) * mm});
            skLineSegment(sketch, "E5.0.1.49", {"start": v(490.22, 149.86) * mm, "end": v(515.62, 149.86) * mm});
            skLineSegment(sketch, "E5.0.1.50", {"start": v(368.3, 149.86) * mm, "end": v(393.7, 149.86) * mm});
            skLineSegment(sketch, "E5.0.1.51", {"start": v(734.06, 149.86) * mm, "end": v(759.46, 149.86) * mm});
            skLineSegment(sketch, "E5.0.1.52", {"start": v(612.14, 149.86) * mm, "end": v(612.14, 129.54) * mm});
            skLineSegment(sketch, "E5.0.1.53", {"start": v(490.22, 149.86) * mm, "end": v(490.22, 129.54) * mm});
            skLineSegment(sketch, "E5.0.1.54", {"start": v(734.06, 149.86) * mm, "end": v(734.06, 129.54) * mm});
            skLineSegment(sketch, "E5.0.1.55", {"start": v(612.14, 129.54) * mm, "end": v(637.54, 129.54) * mm});
            skLineSegment(sketch, "E5.0.1.56", {"start": v(490.22, 129.54) * mm, "end": v(515.62, 129.54) * mm});
            skLineSegment(sketch, "E5.0.1.57", {"start": v(368.3, 129.54) * mm, "end": v(393.7, 129.54) * mm});
            skLineSegment(sketch, "E5.0.1.58", {"start": v(734.06, 129.54) * mm, "end": v(759.46, 129.54) * mm});
            skLineSegment(sketch, "E5.0.1.59", {"start": v(764.54, 149.86) * mm, "end": v(789.94, 149.86) * mm});
            skLineSegment(sketch, "E5.0.1.60", {"start": v(642.62, 149.86) * mm, "end": v(668.02, 149.86) * mm});
            skLineSegment(sketch, "E5.0.1.61", {"start": v(520.7, 149.86) * mm, "end": v(546.1, 149.86) * mm});
            skLineSegment(sketch, "E5.0.1.62", {"start": v(398.78, 149.86) * mm, "end": v(424.18, 149.86) * mm});
            skLineSegment(sketch, "E5.0.1.63", {"start": v(668.02, 149.86) * mm, "end": v(668.02, 129.54) * mm});
            skLineSegment(sketch, "E5.0.1.64", {"start": v(546.1, 149.86) * mm, "end": v(546.1, 129.54) * mm});
            skLineSegment(sketch, "E5.0.1.65", {"start": v(424.18, 149.86) * mm, "end": v(424.18, 129.54) * mm});
            skLineSegment(sketch, "E5.0.1.66", {"start": v(789.94, 149.86) * mm, "end": v(789.94, 129.54) * mm});
            skLineSegment(sketch, "E5.0.1.67", {"start": v(764.54, 149.86) * mm, "end": v(764.54, 129.54) * mm});
            skLineSegment(sketch, "E5.0.1.68", {"start": v(642.62, 149.86) * mm, "end": v(642.62, 129.54) * mm});
            skLineSegment(sketch, "E5.0.1.69", {"start": v(520.7, 149.86) * mm, "end": v(520.7, 129.54) * mm});
            skLineSegment(sketch, "E5.0.1.70", {"start": v(398.78, 149.86) * mm, "end": v(398.78, 129.54) * mm});
            skLineSegment(sketch, "E5.0.1.71", {"start": v(332.74, 149.86) * mm, "end": v(332.74, 129.54) * mm});
            skLineSegment(sketch, "E5.0.1.72", {"start": v(210.82, 149.86) * mm, "end": v(210.82, 129.54) * mm});
            skLineSegment(sketch, "E5.0.1.73", {"start": v(88.9, 149.86) * mm, "end": v(88.9, 129.54) * mm});
            skLineSegment(sketch, "E5.0.1.74", {"start": v(33.02, 129.54) * mm, "end": v(58.42, 129.54) * mm});
            skLineSegment(sketch, "E5.0.1.75", {"start": v(154.94, 129.54) * mm, "end": v(180.34, 129.54) * mm});
            skLineSegment(sketch, "E5.0.1.76", {"start": v(276.86, 129.54) * mm, "end": v(302.26, 129.54) * mm});
            skLineSegment(sketch, "E5.0.1.77", {"start": v(307.34, 149.86) * mm, "end": v(332.74, 149.86) * mm});
            skLineSegment(sketch, "E5.0.1.78", {"start": v(185.42, 149.86) * mm, "end": v(210.82, 149.86) * mm});
            skLineSegment(sketch, "E5.0.1.79", {"start": v(63.5, 149.86) * mm, "end": v(88.9, 149.86) * mm});
            skLineSegment(sketch, "E5.0.1.80", {"start": v(307.34, 149.86) * mm, "end": v(307.34, 129.54) * mm});
            skLineSegment(sketch, "E5.0.1.81", {"start": v(185.42, 149.86) * mm, "end": v(185.42, 129.54) * mm});
            skLineSegment(sketch, "E5.0.1.82", {"start": v(63.5, 149.86) * mm, "end": v(63.5, 129.54) * mm});
            skLineSegment(sketch, "E5.0.1.83", {"start": v(307.34, 129.54) * mm, "end": v(332.74, 129.54) * mm});
            skLineSegment(sketch, "E5.0.1.84", {"start": v(185.42, 129.54) * mm, "end": v(210.82, 129.54) * mm});
            skLineSegment(sketch, "E5.0.1.85", {"start": v(63.5, 129.54) * mm, "end": v(88.9, 129.54) * mm});
            skLineSegment(sketch, "E5.0.1.86", {"start": v(363.22, 149.86) * mm, "end": v(363.22, 129.54) * mm});
            skLineSegment(sketch, "E5.0.1.87", {"start": v(241.3, 149.86) * mm, "end": v(241.3, 129.54) * mm});
            skLineSegment(sketch, "E5.0.1.88", {"start": v(119.38, 149.86) * mm, "end": v(119.38, 129.54) * mm});
            skLineSegment(sketch, "E5.0.1.89", {"start": v(337.82, 149.86) * mm, "end": v(363.22, 149.86) * mm});
            skLineSegment(sketch, "E5.0.1.90", {"start": v(215.9, 149.86) * mm, "end": v(241.3, 149.86) * mm});
            skLineSegment(sketch, "E5.0.1.91", {"start": v(93.98, 149.86) * mm, "end": v(119.38, 149.86) * mm});
            skLineSegment(sketch, "E5.0.1.92", {"start": v(337.82, 149.86) * mm, "end": v(337.82, 129.54) * mm});
            skLineSegment(sketch, "E5.0.1.93", {"start": v(215.9, 149.86) * mm, "end": v(215.9, 129.54) * mm});
            skLineSegment(sketch, "E5.0.1.94", {"start": v(93.98, 149.86) * mm, "end": v(93.98, 129.54) * mm});
            skLineSegment(sketch, "E5.0.1.95", {"start": v(93.98, 129.54) * mm, "end": v(119.38, 129.54) * mm});
            skLineSegment(sketch, "E5.0.1.96", {"start": v(337.82, 129.54) * mm, "end": v(363.22, 129.54) * mm});
            skLineSegment(sketch, "E5.0.1.97", {"start": v(215.9, 129.54) * mm, "end": v(241.3, 129.54) * mm});
            skLineSegment(sketch, "E5.0.1.98", {"start": v(149.86, 149.86) * mm, "end": v(149.86, 129.54) * mm});
            skLineSegment(sketch, "E5.0.1.99", {"start": v(27.94, 149.86) * mm, "end": v(27.94, 129.54) * mm});
            skLineSegment(sketch, "E5.0.1.100", {"start": v(271.78, 149.86) * mm, "end": v(271.78, 129.54) * mm});
            skLineSegment(sketch, "E5.0.1.101", {"start": v(124.46, 149.86) * mm, "end": v(149.86, 149.86) * mm});
            skLineSegment(sketch, "E5.0.1.102", {"start": v(2.54, 149.86) * mm, "end": v(27.94, 149.86) * mm});
            skLineSegment(sketch, "E5.0.1.103", {"start": v(246.38, 149.86) * mm, "end": v(271.78, 149.86) * mm});
            skLineSegment(sketch, "E5.0.1.104", {"start": v(124.46, 149.86) * mm, "end": v(124.46, 129.54) * mm});
            skLineSegment(sketch, "E5.0.1.105", {"start": v(2.54, 149.86) * mm, "end": v(2.54, 129.54) * mm});
            skLineSegment(sketch, "E5.0.1.106", {"start": v(368.3, 149.86) * mm, "end": v(368.3, 129.54) * mm});
            skLineSegment(sketch, "E5.0.1.107", {"start": v(246.38, 149.86) * mm, "end": v(246.38, 129.54) * mm});
            skLineSegment(sketch, "E5.0.1.108", {"start": v(124.46, 129.54) * mm, "end": v(149.86, 129.54) * mm});
            skLineSegment(sketch, "E5.0.1.109", {"start": v(2.54, 129.54) * mm, "end": v(27.94, 129.54) * mm});
            skLineSegment(sketch, "E5.0.1.110", {"start": v(246.38, 129.54) * mm, "end": v(271.78, 129.54) * mm});
            skLineSegment(sketch, "E5.0.1.111", {"start": v(276.86, 149.86) * mm, "end": v(302.26, 149.86) * mm});
            skLineSegment(sketch, "E5.0.1.112", {"start": v(154.94, 149.86) * mm, "end": v(180.34, 149.86) * mm});
            skLineSegment(sketch, "E5.0.1.113", {"start": v(33.02, 149.86) * mm, "end": v(58.42, 149.86) * mm});
            skLineSegment(sketch, "E5.0.1.114", {"start": v(180.34, 149.86) * mm, "end": v(180.34, 129.54) * mm});
            skLineSegment(sketch, "E5.0.1.115", {"start": v(58.42, 149.86) * mm, "end": v(58.42, 129.54) * mm});
            skLineSegment(sketch, "E5.0.1.116", {"start": v(302.26, 149.86) * mm, "end": v(302.26, 129.54) * mm});
            skLineSegment(sketch, "E5.0.1.117", {"start": v(276.86, 149.86) * mm, "end": v(276.86, 129.54) * mm});
            skLineSegment(sketch, "E5.0.1.118", {"start": v(154.94, 149.86) * mm, "end": v(154.94, 129.54) * mm});
            skLineSegment(sketch, "E5.0.1.119", {"start": v(33.02, 149.86) * mm, "end": v(33.02, 129.54) * mm});
            skLineSegment(sketch, "E5.0.1.120", {"start": v(-520.7, 149.86) * mm, "end": v(-520.7, 129.54) * mm});
            skLineSegment(sketch, "E5.0.1.121", {"start": v(-332.74, 129.54) * mm, "end": v(-307.34, 129.54) * mm});
            skLineSegment(sketch, "E5.0.1.122", {"start": v(-398.78, 149.86) * mm, "end": v(-398.78, 129.54) * mm});
            skLineSegment(sketch, "E5.0.1.123", {"start": v(-33.02, 149.86) * mm, "end": v(-33.02, 129.54) * mm});
            skLineSegment(sketch, "E5.0.1.124", {"start": v(-88.9, 129.54) * mm, "end": v(-63.5, 129.54) * mm});
            skLineSegment(sketch, "E5.0.1.125", {"start": v(-698.5, 129.54) * mm, "end": v(-673.1, 129.54) * mm});
            skLineSegment(sketch, "E5.0.1.126", {"start": v(-454.66, 129.54) * mm, "end": v(-429.26, 129.54) * mm});
            skLineSegment(sketch, "E5.0.1.127", {"start": v(-642.62, 149.86) * mm, "end": v(-642.62, 129.54) * mm});
            skLineSegment(sketch, "E5.0.1.128", {"start": v(-764.54, 149.86) * mm, "end": v(-764.54, 129.54) * mm});
            skLineSegment(sketch, "E5.0.1.129", {"start": v(-154.94, 149.86) * mm, "end": v(-154.94, 129.54) * mm});
            skLineSegment(sketch, "E5.0.1.130", {"start": v(-210.82, 129.54) * mm, "end": v(-185.42, 129.54) * mm});
            skLineSegment(sketch, "E5.0.1.131", {"start": v(-576.58, 129.54) * mm, "end": v(-551.18, 129.54) * mm});
            skLineSegment(sketch, "E5.0.1.132", {"start": v(-276.86, 149.86) * mm, "end": v(-276.86, 129.54) * mm});
            skLineSegment(sketch, "E5.0.1.133", {"start": v(-886.46, 129.54) * mm, "end": v(-855.98, 129.54) * mm, "construction": true});
            skLineSegment(sketch, "E5.0.1.134", {"start": v(-180.34, 149.86) * mm, "end": v(-154.94, 149.86) * mm});
            skLineSegment(sketch, "E5.0.1.135", {"start": v(-302.26, 149.86) * mm, "end": v(-276.86, 149.86) * mm});
            skLineSegment(sketch, "E5.0.1.136", {"start": v(-424.18, 149.86) * mm, "end": v(-398.78, 149.86) * mm});
            skLineSegment(sketch, "E5.0.1.137", {"start": v(-546.1, 149.86) * mm, "end": v(-520.7, 149.86) * mm});
            skLineSegment(sketch, "E5.0.1.138", {"start": v(-58.42, 149.86) * mm, "end": v(-33.02, 149.86) * mm});
            skLineSegment(sketch, "E5.0.1.139", {"start": v(-668.02, 149.86) * mm, "end": v(-642.62, 149.86) * mm});
            skLineSegment(sketch, "E5.0.1.140", {"start": v(-789.94, 149.86) * mm, "end": v(-764.54, 149.86) * mm});
            skLineSegment(sketch, "E5.0.1.141", {"start": v(-58.42, 149.86) * mm, "end": v(-58.42, 129.54) * mm});
            skLineSegment(sketch, "E5.0.1.142", {"start": v(-668.02, 149.86) * mm, "end": v(-668.02, 129.54) * mm});
            skLineSegment(sketch, "E5.0.1.143", {"start": v(-789.94, 149.86) * mm, "end": v(-789.94, 129.54) * mm});
            skLineSegment(sketch, "E5.0.1.144", {"start": v(-180.34, 149.86) * mm, "end": v(-180.34, 129.54) * mm});
            skLineSegment(sketch, "E5.0.1.145", {"start": v(-302.26, 149.86) * mm, "end": v(-302.26, 129.54) * mm});
            skLineSegment(sketch, "E5.0.1.146", {"start": v(-424.18, 149.86) * mm, "end": v(-424.18, 129.54) * mm});
            skLineSegment(sketch, "E5.0.1.147", {"start": v(-546.1, 149.86) * mm, "end": v(-546.1, 129.54) * mm});
            skLineSegment(sketch, "E5.0.1.148", {"start": v(-668.02, 129.54) * mm, "end": v(-642.62, 129.54) * mm});
            skLineSegment(sketch, "E5.0.1.149", {"start": v(-789.94, 129.54) * mm, "end": v(-764.54, 129.54) * mm});
            skLineSegment(sketch, "E5.0.1.150", {"start": v(-180.34, 129.54) * mm, "end": v(-154.94, 129.54) * mm});
            skLineSegment(sketch, "E5.0.1.151", {"start": v(-302.26, 129.54) * mm, "end": v(-276.86, 129.54) * mm});
            skLineSegment(sketch, "E5.0.1.152", {"start": v(-424.18, 129.54) * mm, "end": v(-398.78, 129.54) * mm});
            skLineSegment(sketch, "E5.0.1.153", {"start": v(-546.1, 129.54) * mm, "end": v(-520.7, 129.54) * mm});
            skLineSegment(sketch, "E5.0.1.154", {"start": v(-58.42, 129.54) * mm, "end": v(-33.02, 129.54) * mm});
            skLineSegment(sketch, "E5.0.1.155", {"start": v(-612.14, 149.86) * mm, "end": v(-612.14, 129.54) * mm});
            skLineSegment(sketch, "E5.0.1.156", {"start": v(-734.06, 149.86) * mm, "end": v(-734.06, 129.54) * mm});
            skLineSegment(sketch, "E5.0.1.157", {"start": v(-124.46, 149.86) * mm, "end": v(-124.46, 129.54) * mm});
            skLineSegment(sketch, "E5.0.1.158", {"start": v(-246.38, 149.86) * mm, "end": v(-246.38, 129.54) * mm});
            skLineSegment(sketch, "E5.0.1.159", {"start": v(-368.3, 149.86) * mm, "end": v(-368.3, 129.54) * mm});
            skLineSegment(sketch, "E5.0.1.160", {"start": v(-490.22, 149.86) * mm, "end": v(-490.22, 129.54) * mm});
            skLineSegment(sketch, "E5.0.1.161", {"start": v(-2.54, 149.86) * mm, "end": v(-2.54, 129.54) * mm});
            skLineSegment(sketch, "E5.0.1.162", {"start": v(-637.54, 149.86) * mm, "end": v(-612.14, 149.86) * mm});
            skLineSegment(sketch, "E5.0.1.163", {"start": v(-759.46, 149.86) * mm, "end": v(-734.06, 149.86) * mm});
            skLineSegment(sketch, "E5.0.1.164", {"start": v(-149.86, 149.86) * mm, "end": v(-124.46, 149.86) * mm});
            skLineSegment(sketch, "E5.0.1.165", {"start": v(-271.78, 149.86) * mm, "end": v(-246.38, 149.86) * mm});
            skLineSegment(sketch, "E5.0.1.166", {"start": v(-393.7, 149.86) * mm, "end": v(-368.3, 149.86) * mm});
            skLineSegment(sketch, "E5.0.1.167", {"start": v(-515.62, 149.86) * mm, "end": v(-490.22, 149.86) * mm});
            skLineSegment(sketch, "E5.0.1.168", {"start": v(-27.94, 149.86) * mm, "end": v(-2.54, 149.86) * mm});
            skLineSegment(sketch, "E5.0.1.169", {"start": v(-637.54, 149.86) * mm, "end": v(-637.54, 129.54) * mm});
            skLineSegment(sketch, "E5.0.1.170", {"start": v(-759.46, 149.86) * mm, "end": v(-759.46, 129.54) * mm});
            skLineSegment(sketch, "E5.0.1.171", {"start": v(-149.86, 149.86) * mm, "end": v(-149.86, 129.54) * mm});
            skLineSegment(sketch, "E5.0.1.172", {"start": v(-271.78, 149.86) * mm, "end": v(-271.78, 129.54) * mm});
            skLineSegment(sketch, "E5.0.1.173", {"start": v(-393.7, 149.86) * mm, "end": v(-393.7, 129.54) * mm});
            skLineSegment(sketch, "E5.0.1.174", {"start": v(-515.62, 149.86) * mm, "end": v(-515.62, 129.54) * mm});
            skLineSegment(sketch, "E5.0.1.175", {"start": v(-27.94, 149.86) * mm, "end": v(-27.94, 129.54) * mm});
            skLineSegment(sketch, "E5.0.1.176", {"start": v(-393.7, 129.54) * mm, "end": v(-368.3, 129.54) * mm});
            skLineSegment(sketch, "E5.0.1.177", {"start": v(-515.62, 129.54) * mm, "end": v(-490.22, 129.54) * mm});
            skLineSegment(sketch, "E5.0.1.178", {"start": v(-637.54, 129.54) * mm, "end": v(-612.14, 129.54) * mm});
            skLineSegment(sketch, "E5.0.1.179", {"start": v(-759.46, 129.54) * mm, "end": v(-734.06, 129.54) * mm});
            skLineSegment(sketch, "E5.0.1.180", {"start": v(-27.94, 129.54) * mm, "end": v(-2.54, 129.54) * mm});
            skLineSegment(sketch, "E5.0.1.181", {"start": v(-149.86, 129.54) * mm, "end": v(-124.46, 129.54) * mm});
            skLineSegment(sketch, "E5.0.1.182", {"start": v(-271.78, 129.54) * mm, "end": v(-246.38, 129.54) * mm});
            skLineSegment(sketch, "E5.0.1.183", {"start": v(-337.82, 149.86) * mm, "end": v(-337.82, 129.54) * mm});
            skLineSegment(sketch, "E5.0.1.184", {"start": v(-459.74, 149.86) * mm, "end": v(-459.74, 129.54) * mm});
            skLineSegment(sketch, "E5.0.1.185", {"start": v(-581.66, 149.86) * mm, "end": v(-581.66, 129.54) * mm});
            skLineSegment(sketch, "E5.0.1.186", {"start": v(-703.58, 149.86) * mm, "end": v(-703.58, 129.54) * mm});
            skLineSegment(sketch, "E5.0.1.187", {"start": v(-93.98, 149.86) * mm, "end": v(-93.98, 129.54) * mm});
            skLineSegment(sketch, "E5.0.1.188", {"start": v(-215.9, 149.86) * mm, "end": v(-215.9, 129.54) * mm});
            skLineSegment(sketch, "E5.0.1.189", {"start": v(-363.22, 149.86) * mm, "end": v(-337.82, 149.86) * mm});
            skLineSegment(sketch, "E5.0.1.190", {"start": v(-485.14, 149.86) * mm, "end": v(-459.74, 149.86) * mm});
            skLineSegment(sketch, "E5.0.1.191", {"start": v(-607.06, 149.86) * mm, "end": v(-581.66, 149.86) * mm});
            skLineSegment(sketch, "E5.0.1.192", {"start": v(-728.98, 149.86) * mm, "end": v(-703.58, 149.86) * mm});
            skLineSegment(sketch, "E5.0.1.193", {"start": v(-119.38, 149.86) * mm, "end": v(-93.98, 149.86) * mm});
            skLineSegment(sketch, "E5.0.1.194", {"start": v(-241.3, 149.86) * mm, "end": v(-215.9, 149.86) * mm});
            skLineSegment(sketch, "E5.0.1.195", {"start": v(-363.22, 149.86) * mm, "end": v(-363.22, 129.54) * mm});
            skLineSegment(sketch, "E5.0.1.196", {"start": v(-485.14, 149.86) * mm, "end": v(-485.14, 129.54) * mm});
            skLineSegment(sketch, "E5.0.1.197", {"start": v(-607.06, 149.86) * mm, "end": v(-607.06, 129.54) * mm});
            skLineSegment(sketch, "E5.0.1.198", {"start": v(-728.98, 149.86) * mm, "end": v(-728.98, 129.54) * mm});
            skLineSegment(sketch, "E5.0.1.199", {"start": v(-119.38, 149.86) * mm, "end": v(-119.38, 129.54) * mm});
            skLineSegment(sketch, "E5.0.1.200", {"start": v(-241.3, 149.86) * mm, "end": v(-241.3, 129.54) * mm});
            skLineSegment(sketch, "E5.0.1.201", {"start": v(-363.22, 129.54) * mm, "end": v(-337.82, 129.54) * mm});
            skLineSegment(sketch, "E5.0.1.202", {"start": v(-485.14, 129.54) * mm, "end": v(-459.74, 129.54) * mm});
            skLineSegment(sketch, "E5.0.1.203", {"start": v(-607.06, 129.54) * mm, "end": v(-581.66, 129.54) * mm});
            skLineSegment(sketch, "E5.0.1.204", {"start": v(-728.98, 129.54) * mm, "end": v(-703.58, 129.54) * mm});
            skLineSegment(sketch, "E5.0.1.205", {"start": v(-119.38, 129.54) * mm, "end": v(-93.98, 129.54) * mm});
            skLineSegment(sketch, "E5.0.1.206", {"start": v(-241.3, 129.54) * mm, "end": v(-215.9, 129.54) * mm});
            skLineSegment(sketch, "E5.0.1.207", {"start": v(-698.5, 149.86) * mm, "end": v(-673.1, 149.86) * mm});
            skLineSegment(sketch, "E5.0.1.208", {"start": v(-210.82, 149.86) * mm, "end": v(-185.42, 149.86) * mm});
            skLineSegment(sketch, "E5.0.1.209", {"start": v(-332.74, 149.86) * mm, "end": v(-307.34, 149.86) * mm});
            skLineSegment(sketch, "E5.0.1.210", {"start": v(-454.66, 149.86) * mm, "end": v(-429.26, 149.86) * mm});
            skLineSegment(sketch, "E5.0.1.211", {"start": v(-576.58, 149.86) * mm, "end": v(-551.18, 149.86) * mm});
            skLineSegment(sketch, "E5.0.1.212", {"start": v(-88.9, 149.86) * mm, "end": v(-63.5, 149.86) * mm});
            skLineSegment(sketch, "E5.0.1.213", {"start": v(-820.42, 149.86) * mm, "end": v(-795.02, 149.86) * mm});
            skLineSegment(sketch, "E5.0.1.214", {"start": v(-820.42, 149.86) * mm, "end": v(-820.42, 129.54) * mm});
            skLineSegment(sketch, "E5.0.1.215", {"start": v(-820.42, 129.54) * mm, "end": v(-795.02, 129.54) * mm});
            skLineSegment(sketch, "E5.0.1.216", {"start": v(-911.86, 149.86) * mm, "end": v(-886.46, 149.86) * mm});
            skLineSegment(sketch, "E5.0.1.217", {"start": v(-911.86, 129.54) * mm, "end": v(-886.46, 129.54) * mm});
            skLineSegment(sketch, "E5.0.1.218", {"start": v(-911.86, 149.86) * mm, "end": v(-911.86, 129.54) * mm});
            skLineSegment(sketch, "E5.0.1.219", {"start": v(-886.46, 149.86) * mm, "end": v(-886.46, 129.54) * mm});
            skLineSegment(sketch, "E5.0.1.220", {"start": v(-855.98, 149.86) * mm, "end": v(-855.98, 129.54) * mm});
            skLineSegment(sketch, "E5.0.1.221", {"start": v(-881.38, 149.86) * mm, "end": v(-855.98, 149.86) * mm});
            skLineSegment(sketch, "E5.0.1.222", {"start": v(-881.38, 149.86) * mm, "end": v(-881.38, 129.54) * mm});
            skLineSegment(sketch, "E5.0.1.223", {"start": v(-825.5, 149.86) * mm, "end": v(-825.5, 129.54) * mm});
            skLineSegment(sketch, "E5.0.1.224", {"start": v(-850.9, 149.86) * mm, "end": v(-825.5, 149.86) * mm});
            skLineSegment(sketch, "E5.0.1.225", {"start": v(-307.34, 149.86) * mm, "end": v(-307.34, 129.54) * mm});
            skLineSegment(sketch, "E5.0.1.226", {"start": v(-850.9, 149.86) * mm, "end": v(-850.9, 129.54) * mm});
            skLineSegment(sketch, "E5.0.1.227", {"start": v(-429.26, 149.86) * mm, "end": v(-429.26, 129.54) * mm});
            skLineSegment(sketch, "E5.0.1.228", {"start": v(-551.18, 149.86) * mm, "end": v(-551.18, 129.54) * mm});
            skLineSegment(sketch, "E5.0.1.229", {"start": v(-673.1, 149.86) * mm, "end": v(-673.1, 129.54) * mm});
            skLineSegment(sketch, "E5.0.1.230", {"start": v(-850.9, 129.54) * mm, "end": v(-825.5, 129.54) * mm});
            skLineSegment(sketch, "E5.0.1.231", {"start": v(-63.5, 149.86) * mm, "end": v(-63.5, 129.54) * mm});
            skLineSegment(sketch, "E5.0.1.232", {"start": v(-185.42, 149.86) * mm, "end": v(-185.42, 129.54) * mm});
            skLineSegment(sketch, "E5.0.1.233", {"start": v(-795.02, 149.86) * mm, "end": v(-795.02, 129.54) * mm});
            skLineSegment(sketch, "E5.0.1.234", {"start": v(-698.5, 149.86) * mm, "end": v(-698.5, 129.54) * mm});
            skLineSegment(sketch, "E5.0.1.235", {"start": v(-210.82, 149.86) * mm, "end": v(-210.82, 129.54) * mm});
            skLineSegment(sketch, "E5.0.1.236", {"start": v(-332.74, 149.86) * mm, "end": v(-332.74, 129.54) * mm});
            skLineSegment(sketch, "E5.0.1.237", {"start": v(-454.66, 149.86) * mm, "end": v(-454.66, 129.54) * mm});
            skLineSegment(sketch, "E5.0.1.238", {"start": v(-576.58, 149.86) * mm, "end": v(-576.58, 129.54) * mm});
            skLineSegment(sketch, "E5.0.1.239", {"start": v(-88.9, 149.86) * mm, "end": v(-88.9, 129.54) * mm});
            skLineSegment(sketch, "E5.0.1.240", {"start": v(-881.38, 129.54) * mm, "end": v(-855.98, 129.54) * mm});
            skLineSegment(sketch, "E5.direction1", {"start": v(886.46, 154.94) * mm, "end": v(966.22, 154.94) * mm, "construction": true});
            skLineSegment(sketch, "E5.direction2", {"start": v(886.46, 154.94) * mm, "end": v(886.46, 129.54) * mm, "construction": true});
            skLineSegment(sketch, "E6.0.0.2", {"start": v(886.46, 104.14) * mm, "end": v(911.86, 104.14) * mm});
            skLineSegment(sketch, "E6.3.0.2", {"start": v(911.86, 124.46) * mm, "end": v(911.86, 104.14) * mm});
            skLineSegment(sketch, "E6.6.0.2", {"start": v(886.46, 124.46) * mm, "end": v(911.86, 124.46) * mm});
            skLineSegment(sketch, "E6.9.0.2", {"start": v(886.46, 124.46) * mm, "end": v(886.46, 104.14) * mm});
            skLineSegment(sketch, "E6.12.0.2", {"start": v(881.38, 124.46) * mm, "end": v(881.38, 104.14) * mm});
            skLineSegment(sketch, "E6.15.0.2", {"start": v(855.98, 124.46) * mm, "end": v(881.38, 124.46) * mm});
            skLineSegment(sketch, "E6.18.0.2", {"start": v(855.98, 104.14) * mm, "end": v(881.38, 104.14) * mm});
            skLineSegment(sketch, "E6.21.0.2", {"start": v(855.98, 124.46) * mm, "end": v(855.98, 104.14) * mm});
            skLineSegment(sketch, "E6.24.0.2", {"start": v(520.7, 104.14) * mm, "end": v(546.1, 104.14) * mm});
            skLineSegment(sketch, "E6.27.0.2", {"start": v(398.78, 104.14) * mm, "end": v(424.18, 104.14) * mm});
            skLineSegment(sketch, "E6.30.0.2", {"start": v(820.42, 124.46) * mm, "end": v(820.42, 104.14) * mm});
            skLineSegment(sketch, "E6.33.0.2", {"start": v(642.62, 104.14) * mm, "end": v(668.02, 104.14) * mm});
            skLineSegment(sketch, "E6.36.0.2", {"start": v(764.54, 104.14) * mm, "end": v(789.94, 104.14) * mm});
            skLineSegment(sketch, "E6.39.0.2", {"start": v(698.5, 124.46) * mm, "end": v(698.5, 104.14) * mm});
            skLineSegment(sketch, "E6.42.0.2", {"start": v(576.58, 124.46) * mm, "end": v(576.58, 104.14) * mm});
            skLineSegment(sketch, "E6.45.0.2", {"start": v(454.66, 124.46) * mm, "end": v(454.66, 104.14) * mm});
            skLineSegment(sketch, "E6.48.0.2", {"start": v(795.02, 124.46) * mm, "end": v(820.42, 124.46) * mm});
            skLineSegment(sketch, "E6.51.0.2", {"start": v(673.1, 124.46) * mm, "end": v(698.5, 124.46) * mm});
            skLineSegment(sketch, "E6.54.0.2", {"start": v(551.18, 124.46) * mm, "end": v(576.58, 124.46) * mm});
            skLineSegment(sketch, "E6.57.0.2", {"start": v(429.26, 124.46) * mm, "end": v(454.66, 124.46) * mm});
            skLineSegment(sketch, "E6.60.0.2", {"start": v(795.02, 124.46) * mm, "end": v(795.02, 104.14) * mm});
            skLineSegment(sketch, "E6.63.0.2", {"start": v(673.1, 124.46) * mm, "end": v(673.1, 104.14) * mm});
            skLineSegment(sketch, "E6.66.0.2", {"start": v(551.18, 124.46) * mm, "end": v(551.18, 104.14) * mm});
            skLineSegment(sketch, "E6.69.0.2", {"start": v(429.26, 124.46) * mm, "end": v(429.26, 104.14) * mm});
            skLineSegment(sketch, "E6.72.0.2", {"start": v(795.02, 104.14) * mm, "end": v(820.42, 104.14) * mm});
            skLineSegment(sketch, "E6.75.0.2", {"start": v(673.1, 104.14) * mm, "end": v(698.5, 104.14) * mm});
            skLineSegment(sketch, "E6.78.0.2", {"start": v(551.18, 104.14) * mm, "end": v(576.58, 104.14) * mm});
            skLineSegment(sketch, "E6.81.0.2", {"start": v(429.26, 104.14) * mm, "end": v(454.66, 104.14) * mm});
            skLineSegment(sketch, "E6.84.0.2", {"start": v(850.9, 124.46) * mm, "end": v(850.9, 104.14) * mm});
            skLineSegment(sketch, "E6.87.0.2", {"start": v(728.98, 124.46) * mm, "end": v(728.98, 104.14) * mm});
            skLineSegment(sketch, "E6.90.0.2", {"start": v(607.06, 124.46) * mm, "end": v(607.06, 104.14) * mm});
            skLineSegment(sketch, "E6.93.0.2", {"start": v(485.14, 124.46) * mm, "end": v(485.14, 104.14) * mm});
            skLineSegment(sketch, "E6.96.0.2", {"start": v(825.5, 124.46) * mm, "end": v(850.9, 124.46) * mm});
            skLineSegment(sketch, "E6.99.0.2", {"start": v(703.58, 124.46) * mm, "end": v(728.98, 124.46) * mm});
            skLineSegment(sketch, "E6.102.0.2", {"start": v(581.66, 124.46) * mm, "end": v(607.06, 124.46) * mm});
            skLineSegment(sketch, "E6.105.0.2", {"start": v(459.74, 124.46) * mm, "end": v(485.14, 124.46) * mm});
            skLineSegment(sketch, "E6.108.0.2", {"start": v(825.5, 124.46) * mm, "end": v(825.5, 104.14) * mm});
            skLineSegment(sketch, "E6.111.0.2", {"start": v(703.58, 124.46) * mm, "end": v(703.58, 104.14) * mm});
            skLineSegment(sketch, "E6.114.0.2", {"start": v(581.66, 124.46) * mm, "end": v(581.66, 104.14) * mm});
            skLineSegment(sketch, "E6.117.0.2", {"start": v(459.74, 124.46) * mm, "end": v(459.74, 104.14) * mm});
            skLineSegment(sketch, "E6.120.0.2", {"start": v(581.66, 104.14) * mm, "end": v(607.06, 104.14) * mm});
            skLineSegment(sketch, "E6.123.0.2", {"start": v(459.74, 104.14) * mm, "end": v(485.14, 104.14) * mm});
            skLineSegment(sketch, "E6.126.0.2", {"start": v(825.5, 104.14) * mm, "end": v(850.9, 104.14) * mm});
            skLineSegment(sketch, "E6.129.0.2", {"start": v(703.58, 104.14) * mm, "end": v(728.98, 104.14) * mm});
            skLineSegment(sketch, "E6.132.0.2", {"start": v(637.54, 124.46) * mm, "end": v(637.54, 104.14) * mm});
            skLineSegment(sketch, "E6.135.0.2", {"start": v(515.62, 124.46) * mm, "end": v(515.62, 104.14) * mm});
            skLineSegment(sketch, "E6.138.0.2", {"start": v(393.7, 124.46) * mm, "end": v(393.7, 104.14) * mm});
            skLineSegment(sketch, "E6.141.0.2", {"start": v(759.46, 124.46) * mm, "end": v(759.46, 104.14) * mm});
            skLineSegment(sketch, "E6.144.0.2", {"start": v(612.14, 124.46) * mm, "end": v(637.54, 124.46) * mm});
            skLineSegment(sketch, "E6.147.0.2", {"start": v(490.22, 124.46) * mm, "end": v(515.62, 124.46) * mm});
            skLineSegment(sketch, "E6.150.0.2", {"start": v(368.3, 124.46) * mm, "end": v(393.7, 124.46) * mm});
            skLineSegment(sketch, "E6.153.0.2", {"start": v(734.06, 124.46) * mm, "end": v(759.46, 124.46) * mm});
            skLineSegment(sketch, "E6.156.0.2", {"start": v(612.14, 124.46) * mm, "end": v(612.14, 104.14) * mm});
            skLineSegment(sketch, "E6.159.0.2", {"start": v(490.22, 124.46) * mm, "end": v(490.22, 104.14) * mm});
            skLineSegment(sketch, "E6.162.0.2", {"start": v(734.06, 124.46) * mm, "end": v(734.06, 104.14) * mm});
            skLineSegment(sketch, "E6.165.0.2", {"start": v(612.14, 104.14) * mm, "end": v(637.54, 104.14) * mm});
            skLineSegment(sketch, "E6.168.0.2", {"start": v(490.22, 104.14) * mm, "end": v(515.62, 104.14) * mm});
            skLineSegment(sketch, "E6.171.0.2", {"start": v(368.3, 104.14) * mm, "end": v(393.7, 104.14) * mm});
            skLineSegment(sketch, "E6.174.0.2", {"start": v(734.06, 104.14) * mm, "end": v(759.46, 104.14) * mm});
            skLineSegment(sketch, "E6.177.0.2", {"start": v(764.54, 124.46) * mm, "end": v(789.94, 124.46) * mm});
            skLineSegment(sketch, "E6.180.0.2", {"start": v(642.62, 124.46) * mm, "end": v(668.02, 124.46) * mm});
            skLineSegment(sketch, "E6.183.0.2", {"start": v(520.7, 124.46) * mm, "end": v(546.1, 124.46) * mm});
            skLineSegment(sketch, "E6.186.0.2", {"start": v(398.78, 124.46) * mm, "end": v(424.18, 124.46) * mm});
            skLineSegment(sketch, "E6.189.0.2", {"start": v(668.02, 124.46) * mm, "end": v(668.02, 104.14) * mm});
            skLineSegment(sketch, "E6.192.0.2", {"start": v(546.1, 124.46) * mm, "end": v(546.1, 104.14) * mm});
            skLineSegment(sketch, "E6.195.0.2", {"start": v(424.18, 124.46) * mm, "end": v(424.18, 104.14) * mm});
            skLineSegment(sketch, "E6.198.0.2", {"start": v(789.94, 124.46) * mm, "end": v(789.94, 104.14) * mm});
            skLineSegment(sketch, "E6.201.0.2", {"start": v(764.54, 124.46) * mm, "end": v(764.54, 104.14) * mm});
            skLineSegment(sketch, "E6.204.0.2", {"start": v(642.62, 124.46) * mm, "end": v(642.62, 104.14) * mm});
            skLineSegment(sketch, "E6.207.0.2", {"start": v(520.7, 124.46) * mm, "end": v(520.7, 104.14) * mm});
            skLineSegment(sketch, "E6.210.0.2", {"start": v(398.78, 124.46) * mm, "end": v(398.78, 104.14) * mm});
            skLineSegment(sketch, "E6.213.0.2", {"start": v(332.74, 124.46) * mm, "end": v(332.74, 104.14) * mm});
            skLineSegment(sketch, "E6.216.0.2", {"start": v(210.82, 124.46) * mm, "end": v(210.82, 104.14) * mm});
            skLineSegment(sketch, "E6.219.0.2", {"start": v(88.9, 124.46) * mm, "end": v(88.9, 104.14) * mm});
            skLineSegment(sketch, "E6.222.0.2", {"start": v(33.02, 104.14) * mm, "end": v(58.42, 104.14) * mm});
            skLineSegment(sketch, "E6.225.0.2", {"start": v(154.94, 104.14) * mm, "end": v(180.34, 104.14) * mm});
            skLineSegment(sketch, "E6.228.0.2", {"start": v(276.86, 104.14) * mm, "end": v(302.26, 104.14) * mm});
            skLineSegment(sketch, "E6.231.0.2", {"start": v(307.34, 124.46) * mm, "end": v(332.74, 124.46) * mm});
            skLineSegment(sketch, "E6.234.0.2", {"start": v(185.42, 124.46) * mm, "end": v(210.82, 124.46) * mm});
            skLineSegment(sketch, "E6.237.0.2", {"start": v(63.5, 124.46) * mm, "end": v(88.9, 124.46) * mm});
            skLineSegment(sketch, "E6.240.0.2", {"start": v(307.34, 124.46) * mm, "end": v(307.34, 104.14) * mm});
            skLineSegment(sketch, "E6.243.0.2", {"start": v(185.42, 124.46) * mm, "end": v(185.42, 104.14) * mm});
            skLineSegment(sketch, "E6.246.0.2", {"start": v(63.5, 124.46) * mm, "end": v(63.5, 104.14) * mm});
            skLineSegment(sketch, "E6.249.0.2", {"start": v(307.34, 104.14) * mm, "end": v(332.74, 104.14) * mm});
            skLineSegment(sketch, "E6.252.0.2", {"start": v(185.42, 104.14) * mm, "end": v(210.82, 104.14) * mm});
            skLineSegment(sketch, "E6.255.0.2", {"start": v(63.5, 104.14) * mm, "end": v(88.9, 104.14) * mm});
            skLineSegment(sketch, "E6.258.0.2", {"start": v(363.22, 124.46) * mm, "end": v(363.22, 104.14) * mm});
            skLineSegment(sketch, "E6.261.0.2", {"start": v(241.3, 124.46) * mm, "end": v(241.3, 104.14) * mm});
            skLineSegment(sketch, "E6.264.0.2", {"start": v(119.38, 124.46) * mm, "end": v(119.38, 104.14) * mm});
            skLineSegment(sketch, "E6.267.0.2", {"start": v(337.82, 124.46) * mm, "end": v(363.22, 124.46) * mm});
            skLineSegment(sketch, "E6.270.0.2", {"start": v(215.9, 124.46) * mm, "end": v(241.3, 124.46) * mm});
            skLineSegment(sketch, "E6.273.0.2", {"start": v(93.98, 124.46) * mm, "end": v(119.38, 124.46) * mm});
            skLineSegment(sketch, "E6.276.0.2", {"start": v(337.82, 124.46) * mm, "end": v(337.82, 104.14) * mm});
            skLineSegment(sketch, "E6.279.0.2", {"start": v(215.9, 124.46) * mm, "end": v(215.9, 104.14) * mm});
            skLineSegment(sketch, "E6.282.0.2", {"start": v(93.98, 124.46) * mm, "end": v(93.98, 104.14) * mm});
            skLineSegment(sketch, "E6.285.0.2", {"start": v(93.98, 104.14) * mm, "end": v(119.38, 104.14) * mm});
            skLineSegment(sketch, "E6.288.0.2", {"start": v(337.82, 104.14) * mm, "end": v(363.22, 104.14) * mm});
            skLineSegment(sketch, "E6.291.0.2", {"start": v(215.9, 104.14) * mm, "end": v(241.3, 104.14) * mm});
            skLineSegment(sketch, "E6.294.0.2", {"start": v(149.86, 124.46) * mm, "end": v(149.86, 104.14) * mm});
            skLineSegment(sketch, "E6.297.0.2", {"start": v(27.94, 124.46) * mm, "end": v(27.94, 104.14) * mm});
            skLineSegment(sketch, "E6.300.0.2", {"start": v(271.78, 124.46) * mm, "end": v(271.78, 104.14) * mm});
            skLineSegment(sketch, "E6.303.0.2", {"start": v(124.46, 124.46) * mm, "end": v(149.86, 124.46) * mm});
            skLineSegment(sketch, "E6.306.0.2", {"start": v(2.54, 124.46) * mm, "end": v(27.94, 124.46) * mm});
            skLineSegment(sketch, "E6.309.0.2", {"start": v(246.38, 124.46) * mm, "end": v(271.78, 124.46) * mm});
            skLineSegment(sketch, "E6.312.0.2", {"start": v(124.46, 124.46) * mm, "end": v(124.46, 104.14) * mm});
            skLineSegment(sketch, "E6.315.0.2", {"start": v(2.54, 124.46) * mm, "end": v(2.54, 104.14) * mm});
            skLineSegment(sketch, "E6.318.0.2", {"start": v(368.3, 124.46) * mm, "end": v(368.3, 104.14) * mm});
            skLineSegment(sketch, "E6.321.0.2", {"start": v(246.38, 124.46) * mm, "end": v(246.38, 104.14) * mm});
            skLineSegment(sketch, "E6.324.0.2", {"start": v(124.46, 104.14) * mm, "end": v(149.86, 104.14) * mm});
            skLineSegment(sketch, "E6.327.0.2", {"start": v(2.54, 104.14) * mm, "end": v(27.94, 104.14) * mm});
            skLineSegment(sketch, "E6.330.0.2", {"start": v(246.38, 104.14) * mm, "end": v(271.78, 104.14) * mm});
            skLineSegment(sketch, "E6.333.0.2", {"start": v(276.86, 124.46) * mm, "end": v(302.26, 124.46) * mm});
            skLineSegment(sketch, "E6.336.0.2", {"start": v(154.94, 124.46) * mm, "end": v(180.34, 124.46) * mm});
            skLineSegment(sketch, "E6.339.0.2", {"start": v(33.02, 124.46) * mm, "end": v(58.42, 124.46) * mm});
            skLineSegment(sketch, "E6.342.0.2", {"start": v(180.34, 124.46) * mm, "end": v(180.34, 104.14) * mm});
            skLineSegment(sketch, "E6.345.0.2", {"start": v(58.42, 124.46) * mm, "end": v(58.42, 104.14) * mm});
            skLineSegment(sketch, "E6.348.0.2", {"start": v(302.26, 124.46) * mm, "end": v(302.26, 104.14) * mm});
            skLineSegment(sketch, "E6.351.0.2", {"start": v(276.86, 124.46) * mm, "end": v(276.86, 104.14) * mm});
            skLineSegment(sketch, "E6.354.0.2", {"start": v(154.94, 124.46) * mm, "end": v(154.94, 104.14) * mm});
            skLineSegment(sketch, "E6.357.0.2", {"start": v(33.02, 124.46) * mm, "end": v(33.02, 104.14) * mm});
            skLineSegment(sketch, "E6.360.0.2", {"start": v(-520.7, 124.46) * mm, "end": v(-520.7, 104.14) * mm});
            skLineSegment(sketch, "E6.363.0.2", {"start": v(-332.74, 104.14) * mm, "end": v(-307.34, 104.14) * mm});
            skLineSegment(sketch, "E6.366.0.2", {"start": v(-398.78, 124.46) * mm, "end": v(-398.78, 104.14) * mm});
            skLineSegment(sketch, "E6.369.0.2", {"start": v(-33.02, 124.46) * mm, "end": v(-33.02, 104.14) * mm});
            skLineSegment(sketch, "E6.372.0.2", {"start": v(-88.9, 104.14) * mm, "end": v(-63.5, 104.14) * mm});
            skLineSegment(sketch, "E6.375.0.2", {"start": v(-698.5, 104.14) * mm, "end": v(-673.1, 104.14) * mm});
            skLineSegment(sketch, "E6.378.0.2", {"start": v(-454.66, 104.14) * mm, "end": v(-429.26, 104.14) * mm});
            skLineSegment(sketch, "E6.381.0.2", {"start": v(-642.62, 124.46) * mm, "end": v(-642.62, 104.14) * mm});
            skLineSegment(sketch, "E6.384.0.2", {"start": v(-764.54, 124.46) * mm, "end": v(-764.54, 104.14) * mm});
            skLineSegment(sketch, "E6.387.0.2", {"start": v(-154.94, 124.46) * mm, "end": v(-154.94, 104.14) * mm});
            skLineSegment(sketch, "E6.390.0.2", {"start": v(-210.82, 104.14) * mm, "end": v(-185.42, 104.14) * mm});
            skLineSegment(sketch, "E6.393.0.2", {"start": v(-576.58, 104.14) * mm, "end": v(-551.18, 104.14) * mm});
            skLineSegment(sketch, "E6.396.0.2", {"start": v(-276.86, 124.46) * mm, "end": v(-276.86, 104.14) * mm});
            skLineSegment(sketch, "E6.399.0.2", {"start": v(-886.46, 104.14) * mm, "end": v(-855.98, 104.14) * mm, "construction": true});
            skLineSegment(sketch, "E6.402.0.2", {"start": v(-180.34, 124.46) * mm, "end": v(-154.94, 124.46) * mm});
            skLineSegment(sketch, "E6.405.0.2", {"start": v(-302.26, 124.46) * mm, "end": v(-276.86, 124.46) * mm});
            skLineSegment(sketch, "E6.408.0.2", {"start": v(-424.18, 124.46) * mm, "end": v(-398.78, 124.46) * mm});
            skLineSegment(sketch, "E6.411.0.2", {"start": v(-546.1, 124.46) * mm, "end": v(-520.7, 124.46) * mm});
            skLineSegment(sketch, "E6.414.0.2", {"start": v(-58.42, 124.46) * mm, "end": v(-33.02, 124.46) * mm});
            skLineSegment(sketch, "E6.417.0.2", {"start": v(-668.02, 124.46) * mm, "end": v(-642.62, 124.46) * mm});
            skLineSegment(sketch, "E6.420.0.2", {"start": v(-789.94, 124.46) * mm, "end": v(-764.54, 124.46) * mm});
            skLineSegment(sketch, "E6.423.0.2", {"start": v(-58.42, 124.46) * mm, "end": v(-58.42, 104.14) * mm});
            skLineSegment(sketch, "E6.426.0.2", {"start": v(-668.02, 124.46) * mm, "end": v(-668.02, 104.14) * mm});
            skLineSegment(sketch, "E6.429.0.2", {"start": v(-789.94, 124.46) * mm, "end": v(-789.94, 104.14) * mm});
            skLineSegment(sketch, "E6.432.0.2", {"start": v(-180.34, 124.46) * mm, "end": v(-180.34, 104.14) * mm});
            skLineSegment(sketch, "E6.435.0.2", {"start": v(-302.26, 124.46) * mm, "end": v(-302.26, 104.14) * mm});
            skLineSegment(sketch, "E6.438.0.2", {"start": v(-424.18, 124.46) * mm, "end": v(-424.18, 104.14) * mm});
            skLineSegment(sketch, "E6.441.0.2", {"start": v(-546.1, 124.46) * mm, "end": v(-546.1, 104.14) * mm});
            skLineSegment(sketch, "E6.444.0.2", {"start": v(-668.02, 104.14) * mm, "end": v(-642.62, 104.14) * mm});
            skLineSegment(sketch, "E6.447.0.2", {"start": v(-789.94, 104.14) * mm, "end": v(-764.54, 104.14) * mm});
            skLineSegment(sketch, "E6.450.0.2", {"start": v(-180.34, 104.14) * mm, "end": v(-154.94, 104.14) * mm});
            skLineSegment(sketch, "E6.453.0.2", {"start": v(-302.26, 104.14) * mm, "end": v(-276.86, 104.14) * mm});
            skLineSegment(sketch, "E6.456.0.2", {"start": v(-424.18, 104.14) * mm, "end": v(-398.78, 104.14) * mm});
            skLineSegment(sketch, "E6.459.0.2", {"start": v(-546.1, 104.14) * mm, "end": v(-520.7, 104.14) * mm});
            skLineSegment(sketch, "E6.462.0.2", {"start": v(-58.42, 104.14) * mm, "end": v(-33.02, 104.14) * mm});
            skLineSegment(sketch, "E6.465.0.2", {"start": v(-612.14, 124.46) * mm, "end": v(-612.14, 104.14) * mm});
            skLineSegment(sketch, "E6.468.0.2", {"start": v(-734.06, 124.46) * mm, "end": v(-734.06, 104.14) * mm});
            skLineSegment(sketch, "E6.471.0.2", {"start": v(-124.46, 124.46) * mm, "end": v(-124.46, 104.14) * mm});
            skLineSegment(sketch, "E6.474.0.2", {"start": v(-246.38, 124.46) * mm, "end": v(-246.38, 104.14) * mm});
            skLineSegment(sketch, "E6.477.0.2", {"start": v(-368.3, 124.46) * mm, "end": v(-368.3, 104.14) * mm});
            skLineSegment(sketch, "E6.480.0.2", {"start": v(-490.22, 124.46) * mm, "end": v(-490.22, 104.14) * mm});
            skLineSegment(sketch, "E6.483.0.2", {"start": v(-2.54, 124.46) * mm, "end": v(-2.54, 104.14) * mm});
            skLineSegment(sketch, "E6.486.0.2", {"start": v(-637.54, 124.46) * mm, "end": v(-612.14, 124.46) * mm});
            skLineSegment(sketch, "E6.489.0.2", {"start": v(-759.46, 124.46) * mm, "end": v(-734.06, 124.46) * mm});
            skLineSegment(sketch, "E6.492.0.2", {"start": v(-149.86, 124.46) * mm, "end": v(-124.46, 124.46) * mm});
            skLineSegment(sketch, "E6.495.0.2", {"start": v(-271.78, 124.46) * mm, "end": v(-246.38, 124.46) * mm});
            skLineSegment(sketch, "E6.498.0.2", {"start": v(-393.7, 124.46) * mm, "end": v(-368.3, 124.46) * mm});
            skLineSegment(sketch, "E6.501.0.2", {"start": v(-515.62, 124.46) * mm, "end": v(-490.22, 124.46) * mm});
            skLineSegment(sketch, "E6.504.0.2", {"start": v(-27.94, 124.46) * mm, "end": v(-2.54, 124.46) * mm});
            skLineSegment(sketch, "E6.507.0.2", {"start": v(-637.54, 124.46) * mm, "end": v(-637.54, 104.14) * mm});
            skLineSegment(sketch, "E6.510.0.2", {"start": v(-759.46, 124.46) * mm, "end": v(-759.46, 104.14) * mm});
            skLineSegment(sketch, "E6.513.0.2", {"start": v(-149.86, 124.46) * mm, "end": v(-149.86, 104.14) * mm});
            skLineSegment(sketch, "E6.516.0.2", {"start": v(-271.78, 124.46) * mm, "end": v(-271.78, 104.14) * mm});
            skLineSegment(sketch, "E6.519.0.2", {"start": v(-393.7, 124.46) * mm, "end": v(-393.7, 104.14) * mm});
            skLineSegment(sketch, "E6.522.0.2", {"start": v(-515.62, 124.46) * mm, "end": v(-515.62, 104.14) * mm});
            skLineSegment(sketch, "E6.525.0.2", {"start": v(-27.94, 124.46) * mm, "end": v(-27.94, 104.14) * mm});
            skLineSegment(sketch, "E6.528.0.2", {"start": v(-393.7, 104.14) * mm, "end": v(-368.3, 104.14) * mm});
            skLineSegment(sketch, "E6.531.0.2", {"start": v(-515.62, 104.14) * mm, "end": v(-490.22, 104.14) * mm});
            skLineSegment(sketch, "E6.534.0.2", {"start": v(-637.54, 104.14) * mm, "end": v(-612.14, 104.14) * mm});
            skLineSegment(sketch, "E6.537.0.2", {"start": v(-759.46, 104.14) * mm, "end": v(-734.06, 104.14) * mm});
            skLineSegment(sketch, "E6.540.0.2", {"start": v(-27.94, 104.14) * mm, "end": v(-2.54, 104.14) * mm});
            skLineSegment(sketch, "E6.543.0.2", {"start": v(-149.86, 104.14) * mm, "end": v(-124.46, 104.14) * mm});
            skLineSegment(sketch, "E6.546.0.2", {"start": v(-271.78, 104.14) * mm, "end": v(-246.38, 104.14) * mm});
            skLineSegment(sketch, "E6.549.0.2", {"start": v(-337.82, 124.46) * mm, "end": v(-337.82, 104.14) * mm});
            skLineSegment(sketch, "E6.552.0.2", {"start": v(-459.74, 124.46) * mm, "end": v(-459.74, 104.14) * mm});
            skLineSegment(sketch, "E6.555.0.2", {"start": v(-581.66, 124.46) * mm, "end": v(-581.66, 104.14) * mm});
            skLineSegment(sketch, "E6.558.0.2", {"start": v(-703.58, 124.46) * mm, "end": v(-703.58, 104.14) * mm});
            skLineSegment(sketch, "E6.561.0.2", {"start": v(-93.98, 124.46) * mm, "end": v(-93.98, 104.14) * mm});
            skLineSegment(sketch, "E6.564.0.2", {"start": v(-215.9, 124.46) * mm, "end": v(-215.9, 104.14) * mm});
            skLineSegment(sketch, "E6.567.0.2", {"start": v(-363.22, 124.46) * mm, "end": v(-337.82, 124.46) * mm});
            skLineSegment(sketch, "E6.570.0.2", {"start": v(-485.14, 124.46) * mm, "end": v(-459.74, 124.46) * mm});
            skLineSegment(sketch, "E6.573.0.2", {"start": v(-607.06, 124.46) * mm, "end": v(-581.66, 124.46) * mm});
            skLineSegment(sketch, "E6.576.0.2", {"start": v(-728.98, 124.46) * mm, "end": v(-703.58, 124.46) * mm});
            skLineSegment(sketch, "E6.579.0.2", {"start": v(-119.38, 124.46) * mm, "end": v(-93.98, 124.46) * mm});
            skLineSegment(sketch, "E6.582.0.2", {"start": v(-241.3, 124.46) * mm, "end": v(-215.9, 124.46) * mm});
            skLineSegment(sketch, "E6.585.0.2", {"start": v(-363.22, 124.46) * mm, "end": v(-363.22, 104.14) * mm});
            skLineSegment(sketch, "E6.588.0.2", {"start": v(-485.14, 124.46) * mm, "end": v(-485.14, 104.14) * mm});
            skLineSegment(sketch, "E6.591.0.2", {"start": v(-607.06, 124.46) * mm, "end": v(-607.06, 104.14) * mm});
            skLineSegment(sketch, "E6.594.0.2", {"start": v(-728.98, 124.46) * mm, "end": v(-728.98, 104.14) * mm});
            skLineSegment(sketch, "E6.597.0.2", {"start": v(-119.38, 124.46) * mm, "end": v(-119.38, 104.14) * mm});
            skLineSegment(sketch, "E6.600.0.2", {"start": v(-241.3, 124.46) * mm, "end": v(-241.3, 104.14) * mm});
            skLineSegment(sketch, "E6.603.0.2", {"start": v(-363.22, 104.14) * mm, "end": v(-337.82, 104.14) * mm});
            skLineSegment(sketch, "E6.606.0.2", {"start": v(-485.14, 104.14) * mm, "end": v(-459.74, 104.14) * mm});
            skLineSegment(sketch, "E6.609.0.2", {"start": v(-607.06, 104.14) * mm, "end": v(-581.66, 104.14) * mm});
            skLineSegment(sketch, "E6.612.0.2", {"start": v(-728.98, 104.14) * mm, "end": v(-703.58, 104.14) * mm});
            skLineSegment(sketch, "E6.615.0.2", {"start": v(-119.38, 104.14) * mm, "end": v(-93.98, 104.14) * mm});
            skLineSegment(sketch, "E6.618.0.2", {"start": v(-241.3, 104.14) * mm, "end": v(-215.9, 104.14) * mm});
            skLineSegment(sketch, "E6.621.0.2", {"start": v(-698.5, 124.46) * mm, "end": v(-673.1, 124.46) * mm});
            skLineSegment(sketch, "E6.624.0.2", {"start": v(-210.82, 124.46) * mm, "end": v(-185.42, 124.46) * mm});
            skLineSegment(sketch, "E6.627.0.2", {"start": v(-332.74, 124.46) * mm, "end": v(-307.34, 124.46) * mm});
            skLineSegment(sketch, "E6.630.0.2", {"start": v(-454.66, 124.46) * mm, "end": v(-429.26, 124.46) * mm});
            skLineSegment(sketch, "E6.633.0.2", {"start": v(-576.58, 124.46) * mm, "end": v(-551.18, 124.46) * mm});
            skLineSegment(sketch, "E6.636.0.2", {"start": v(-88.9, 124.46) * mm, "end": v(-63.5, 124.46) * mm});
            skLineSegment(sketch, "E6.639.0.2", {"start": v(-820.42, 124.46) * mm, "end": v(-795.02, 124.46) * mm});
            skLineSegment(sketch, "E6.642.0.2", {"start": v(-820.42, 124.46) * mm, "end": v(-820.42, 104.14) * mm});
            skLineSegment(sketch, "E6.645.0.2", {"start": v(-820.42, 104.14) * mm, "end": v(-795.02, 104.14) * mm});
            skLineSegment(sketch, "E6.648.0.2", {"start": v(-911.86, 124.46) * mm, "end": v(-886.46, 124.46) * mm});
            skLineSegment(sketch, "E6.651.0.2", {"start": v(-911.86, 104.14) * mm, "end": v(-886.46, 104.14) * mm});
            skLineSegment(sketch, "E6.654.0.2", {"start": v(-911.86, 124.46) * mm, "end": v(-911.86, 104.14) * mm});
            skLineSegment(sketch, "E6.657.0.2", {"start": v(-886.46, 124.46) * mm, "end": v(-886.46, 104.14) * mm});
            skLineSegment(sketch, "E6.660.0.2", {"start": v(-855.98, 124.46) * mm, "end": v(-855.98, 104.14) * mm});
            skLineSegment(sketch, "E6.663.0.2", {"start": v(-881.38, 124.46) * mm, "end": v(-855.98, 124.46) * mm});
            skLineSegment(sketch, "E6.666.0.2", {"start": v(-881.38, 124.46) * mm, "end": v(-881.38, 104.14) * mm});
            skLineSegment(sketch, "E6.669.0.2", {"start": v(-825.5, 124.46) * mm, "end": v(-825.5, 104.14) * mm});
            skLineSegment(sketch, "E6.672.0.2", {"start": v(-850.9, 124.46) * mm, "end": v(-825.5, 124.46) * mm});
            skLineSegment(sketch, "E6.675.0.2", {"start": v(-307.34, 124.46) * mm, "end": v(-307.34, 104.14) * mm});
            skLineSegment(sketch, "E6.678.0.2", {"start": v(-850.9, 124.46) * mm, "end": v(-850.9, 104.14) * mm});
            skLineSegment(sketch, "E6.681.0.2", {"start": v(-429.26, 124.46) * mm, "end": v(-429.26, 104.14) * mm});
            skLineSegment(sketch, "E6.684.0.2", {"start": v(-551.18, 124.46) * mm, "end": v(-551.18, 104.14) * mm});
            skLineSegment(sketch, "E6.687.0.2", {"start": v(-673.1, 124.46) * mm, "end": v(-673.1, 104.14) * mm});
            skLineSegment(sketch, "E6.690.0.2", {"start": v(-850.9, 104.14) * mm, "end": v(-825.5, 104.14) * mm});
            skLineSegment(sketch, "E6.693.0.2", {"start": v(-63.5, 124.46) * mm, "end": v(-63.5, 104.14) * mm});
            skLineSegment(sketch, "E6.696.0.2", {"start": v(-185.42, 124.46) * mm, "end": v(-185.42, 104.14) * mm});
            skLineSegment(sketch, "E6.699.0.2", {"start": v(-795.02, 124.46) * mm, "end": v(-795.02, 104.14) * mm});
            skLineSegment(sketch, "E6.702.0.2", {"start": v(-698.5, 124.46) * mm, "end": v(-698.5, 104.14) * mm});
            skLineSegment(sketch, "E6.705.0.2", {"start": v(-210.82, 124.46) * mm, "end": v(-210.82, 104.14) * mm});
            skLineSegment(sketch, "E6.708.0.2", {"start": v(-332.74, 124.46) * mm, "end": v(-332.74, 104.14) * mm});
            skLineSegment(sketch, "E6.711.0.2", {"start": v(-454.66, 124.46) * mm, "end": v(-454.66, 104.14) * mm});
            skLineSegment(sketch, "E6.714.0.2", {"start": v(-576.58, 124.46) * mm, "end": v(-576.58, 104.14) * mm});
            skLineSegment(sketch, "E6.717.0.2", {"start": v(-88.9, 124.46) * mm, "end": v(-88.9, 104.14) * mm});
            skLineSegment(sketch, "E6.720.0.2", {"start": v(-881.38, 104.14) * mm, "end": v(-855.98, 104.14) * mm});
            skLineSegment(sketch, "E6.0.0.3", {"start": v(886.46, 78.74) * mm, "end": v(911.86, 78.74) * mm});
            skLineSegment(sketch, "E6.3.0.3", {"start": v(911.86, 99.06) * mm, "end": v(911.86, 78.74) * mm});
            skLineSegment(sketch, "E6.6.0.3", {"start": v(886.46, 99.06) * mm, "end": v(911.86, 99.06) * mm});
            skLineSegment(sketch, "E6.9.0.3", {"start": v(886.46, 99.06) * mm, "end": v(886.46, 78.74) * mm});
            skLineSegment(sketch, "E6.12.0.3", {"start": v(881.38, 99.06) * mm, "end": v(881.38, 78.74) * mm});
            skLineSegment(sketch, "E6.15.0.3", {"start": v(855.98, 99.06) * mm, "end": v(881.38, 99.06) * mm});
            skLineSegment(sketch, "E6.18.0.3", {"start": v(855.98, 78.74) * mm, "end": v(881.38, 78.74) * mm});
            skLineSegment(sketch, "E6.21.0.3", {"start": v(855.98, 99.06) * mm, "end": v(855.98, 78.74) * mm});
            skLineSegment(sketch, "E6.24.0.3", {"start": v(520.7, 78.74) * mm, "end": v(546.1, 78.74) * mm});
            skLineSegment(sketch, "E6.27.0.3", {"start": v(398.78, 78.74) * mm, "end": v(424.18, 78.74) * mm});
            skLineSegment(sketch, "E6.30.0.3", {"start": v(820.42, 99.06) * mm, "end": v(820.42, 78.74) * mm});
            skLineSegment(sketch, "E6.33.0.3", {"start": v(642.62, 78.74) * mm, "end": v(668.02, 78.74) * mm});
            skLineSegment(sketch, "E6.36.0.3", {"start": v(764.54, 78.74) * mm, "end": v(789.94, 78.74) * mm});
            skLineSegment(sketch, "E6.39.0.3", {"start": v(698.5, 99.06) * mm, "end": v(698.5, 78.74) * mm});
            skLineSegment(sketch, "E6.42.0.3", {"start": v(576.58, 99.06) * mm, "end": v(576.58, 78.74) * mm});
            skLineSegment(sketch, "E6.45.0.3", {"start": v(454.66, 99.06) * mm, "end": v(454.66, 78.74) * mm});
            skLineSegment(sketch, "E6.48.0.3", {"start": v(795.02, 99.06) * mm, "end": v(820.42, 99.06) * mm});
            skLineSegment(sketch, "E6.51.0.3", {"start": v(673.1, 99.06) * mm, "end": v(698.5, 99.06) * mm});
            skLineSegment(sketch, "E6.54.0.3", {"start": v(551.18, 99.06) * mm, "end": v(576.58, 99.06) * mm});
            skLineSegment(sketch, "E6.57.0.3", {"start": v(429.26, 99.06) * mm, "end": v(454.66, 99.06) * mm});
            skLineSegment(sketch, "E6.60.0.3", {"start": v(795.02, 99.06) * mm, "end": v(795.02, 78.74) * mm});
            skLineSegment(sketch, "E6.63.0.3", {"start": v(673.1, 99.06) * mm, "end": v(673.1, 78.74) * mm});
            skLineSegment(sketch, "E6.66.0.3", {"start": v(551.18, 99.06) * mm, "end": v(551.18, 78.74) * mm});
            skLineSegment(sketch, "E6.69.0.3", {"start": v(429.26, 99.06) * mm, "end": v(429.26, 78.74) * mm});
            skLineSegment(sketch, "E6.72.0.3", {"start": v(795.02, 78.74) * mm, "end": v(820.42, 78.74) * mm});
            skLineSegment(sketch, "E6.75.0.3", {"start": v(673.1, 78.74) * mm, "end": v(698.5, 78.74) * mm});
            skLineSegment(sketch, "E6.78.0.3", {"start": v(551.18, 78.74) * mm, "end": v(576.58, 78.74) * mm});
            skLineSegment(sketch, "E6.81.0.3", {"start": v(429.26, 78.74) * mm, "end": v(454.66, 78.74) * mm});
            skLineSegment(sketch, "E6.84.0.3", {"start": v(850.9, 99.06) * mm, "end": v(850.9, 78.74) * mm});
            skLineSegment(sketch, "E6.87.0.3", {"start": v(728.98, 99.06) * mm, "end": v(728.98, 78.74) * mm});
            skLineSegment(sketch, "E6.90.0.3", {"start": v(607.06, 99.06) * mm, "end": v(607.06, 78.74) * mm});
            skLineSegment(sketch, "E6.93.0.3", {"start": v(485.14, 99.06) * mm, "end": v(485.14, 78.74) * mm});
            skLineSegment(sketch, "E6.96.0.3", {"start": v(825.5, 99.06) * mm, "end": v(850.9, 99.06) * mm});
            skLineSegment(sketch, "E6.99.0.3", {"start": v(703.58, 99.06) * mm, "end": v(728.98, 99.06) * mm});
            skLineSegment(sketch, "E6.102.0.3", {"start": v(581.66, 99.06) * mm, "end": v(607.06, 99.06) * mm});
            skLineSegment(sketch, "E6.105.0.3", {"start": v(459.74, 99.06) * mm, "end": v(485.14, 99.06) * mm});
            skLineSegment(sketch, "E6.108.0.3", {"start": v(825.5, 99.06) * mm, "end": v(825.5, 78.74) * mm});
            skLineSegment(sketch, "E6.111.0.3", {"start": v(703.58, 99.06) * mm, "end": v(703.58, 78.74) * mm});
            skLineSegment(sketch, "E6.114.0.3", {"start": v(581.66, 99.06) * mm, "end": v(581.66, 78.74) * mm});
            skLineSegment(sketch, "E6.117.0.3", {"start": v(459.74, 99.06) * mm, "end": v(459.74, 78.74) * mm});
            skLineSegment(sketch, "E6.120.0.3", {"start": v(581.66, 78.74) * mm, "end": v(607.06, 78.74) * mm});
            skLineSegment(sketch, "E6.123.0.3", {"start": v(459.74, 78.74) * mm, "end": v(485.14, 78.74) * mm});
            skLineSegment(sketch, "E6.126.0.3", {"start": v(825.5, 78.74) * mm, "end": v(850.9, 78.74) * mm});
            skLineSegment(sketch, "E6.129.0.3", {"start": v(703.58, 78.74) * mm, "end": v(728.98, 78.74) * mm});
            skLineSegment(sketch, "E6.132.0.3", {"start": v(637.54, 99.06) * mm, "end": v(637.54, 78.74) * mm});
            skLineSegment(sketch, "E6.135.0.3", {"start": v(515.62, 99.06) * mm, "end": v(515.62, 78.74) * mm});
            skLineSegment(sketch, "E6.138.0.3", {"start": v(393.7, 99.06) * mm, "end": v(393.7, 78.74) * mm});
            skLineSegment(sketch, "E6.141.0.3", {"start": v(759.46, 99.06) * mm, "end": v(759.46, 78.74) * mm});
            skLineSegment(sketch, "E6.144.0.3", {"start": v(612.14, 99.06) * mm, "end": v(637.54, 99.06) * mm});
            skLineSegment(sketch, "E6.147.0.3", {"start": v(490.22, 99.06) * mm, "end": v(515.62, 99.06) * mm});
            skLineSegment(sketch, "E6.150.0.3", {"start": v(368.3, 99.06) * mm, "end": v(393.7, 99.06) * mm});
            skLineSegment(sketch, "E6.153.0.3", {"start": v(734.06, 99.06) * mm, "end": v(759.46, 99.06) * mm});
            skLineSegment(sketch, "E6.156.0.3", {"start": v(612.14, 99.06) * mm, "end": v(612.14, 78.74) * mm});
            skLineSegment(sketch, "E6.159.0.3", {"start": v(490.22, 99.06) * mm, "end": v(490.22, 78.74) * mm});
            skLineSegment(sketch, "E6.162.0.3", {"start": v(734.06, 99.06) * mm, "end": v(734.06, 78.74) * mm});
            skLineSegment(sketch, "E6.165.0.3", {"start": v(612.14, 78.74) * mm, "end": v(637.54, 78.74) * mm});
            skLineSegment(sketch, "E6.168.0.3", {"start": v(490.22, 78.74) * mm, "end": v(515.62, 78.74) * mm});
            skLineSegment(sketch, "E6.171.0.3", {"start": v(368.3, 78.74) * mm, "end": v(393.7, 78.74) * mm});
            skLineSegment(sketch, "E6.174.0.3", {"start": v(734.06, 78.74) * mm, "end": v(759.46, 78.74) * mm});
            skLineSegment(sketch, "E6.177.0.3", {"start": v(764.54, 99.06) * mm, "end": v(789.94, 99.06) * mm});
            skLineSegment(sketch, "E6.180.0.3", {"start": v(642.62, 99.06) * mm, "end": v(668.02, 99.06) * mm});
            skLineSegment(sketch, "E6.183.0.3", {"start": v(520.7, 99.06) * mm, "end": v(546.1, 99.06) * mm});
            skLineSegment(sketch, "E6.186.0.3", {"start": v(398.78, 99.06) * mm, "end": v(424.18, 99.06) * mm});
            skLineSegment(sketch, "E6.189.0.3", {"start": v(668.02, 99.06) * mm, "end": v(668.02, 78.74) * mm});
            skLineSegment(sketch, "E6.192.0.3", {"start": v(546.1, 99.06) * mm, "end": v(546.1, 78.74) * mm});
            skLineSegment(sketch, "E6.195.0.3", {"start": v(424.18, 99.06) * mm, "end": v(424.18, 78.74) * mm});
            skLineSegment(sketch, "E6.198.0.3", {"start": v(789.94, 99.06) * mm, "end": v(789.94, 78.74) * mm});
            skLineSegment(sketch, "E6.201.0.3", {"start": v(764.54, 99.06) * mm, "end": v(764.54, 78.74) * mm});
            skLineSegment(sketch, "E6.204.0.3", {"start": v(642.62, 99.06) * mm, "end": v(642.62, 78.74) * mm});
            skLineSegment(sketch, "E6.207.0.3", {"start": v(520.7, 99.06) * mm, "end": v(520.7, 78.74) * mm});
            skLineSegment(sketch, "E6.210.0.3", {"start": v(398.78, 99.06) * mm, "end": v(398.78, 78.74) * mm});
            skLineSegment(sketch, "E6.213.0.3", {"start": v(332.74, 99.06) * mm, "end": v(332.74, 78.74) * mm});
            skLineSegment(sketch, "E6.216.0.3", {"start": v(210.82, 99.06) * mm, "end": v(210.82, 78.74) * mm});
            skLineSegment(sketch, "E6.219.0.3", {"start": v(88.9, 99.06) * mm, "end": v(88.9, 78.74) * mm});
            skLineSegment(sketch, "E6.222.0.3", {"start": v(33.02, 78.74) * mm, "end": v(58.42, 78.74) * mm});
            skLineSegment(sketch, "E6.225.0.3", {"start": v(154.94, 78.74) * mm, "end": v(180.34, 78.74) * mm});
            skLineSegment(sketch, "E6.228.0.3", {"start": v(276.86, 78.74) * mm, "end": v(302.26, 78.74) * mm});
            skLineSegment(sketch, "E6.231.0.3", {"start": v(307.34, 99.06) * mm, "end": v(332.74, 99.06) * mm});
            skLineSegment(sketch, "E6.234.0.3", {"start": v(185.42, 99.06) * mm, "end": v(210.82, 99.06) * mm});
            skLineSegment(sketch, "E6.237.0.3", {"start": v(63.5, 99.06) * mm, "end": v(88.9, 99.06) * mm});
            skLineSegment(sketch, "E6.240.0.3", {"start": v(307.34, 99.06) * mm, "end": v(307.34, 78.74) * mm});
            skLineSegment(sketch, "E6.243.0.3", {"start": v(185.42, 99.06) * mm, "end": v(185.42, 78.74) * mm});
            skLineSegment(sketch, "E6.246.0.3", {"start": v(63.5, 99.06) * mm, "end": v(63.5, 78.74) * mm});
            skLineSegment(sketch, "E6.249.0.3", {"start": v(307.34, 78.74) * mm, "end": v(332.74, 78.74) * mm});
            skLineSegment(sketch, "E6.252.0.3", {"start": v(185.42, 78.74) * mm, "end": v(210.82, 78.74) * mm});
            skLineSegment(sketch, "E6.255.0.3", {"start": v(63.5, 78.74) * mm, "end": v(88.9, 78.74) * mm});
            skLineSegment(sketch, "E6.258.0.3", {"start": v(363.22, 99.06) * mm, "end": v(363.22, 78.74) * mm});
            skLineSegment(sketch, "E6.261.0.3", {"start": v(241.3, 99.06) * mm, "end": v(241.3, 78.74) * mm});
            skLineSegment(sketch, "E6.264.0.3", {"start": v(119.38, 99.06) * mm, "end": v(119.38, 78.74) * mm});
            skLineSegment(sketch, "E6.267.0.3", {"start": v(337.82, 99.06) * mm, "end": v(363.22, 99.06) * mm});
            skLineSegment(sketch, "E6.270.0.3", {"start": v(215.9, 99.06) * mm, "end": v(241.3, 99.06) * mm});
            skLineSegment(sketch, "E6.273.0.3", {"start": v(93.98, 99.06) * mm, "end": v(119.38, 99.06) * mm});
            skLineSegment(sketch, "E6.276.0.3", {"start": v(337.82, 99.06) * mm, "end": v(337.82, 78.74) * mm});
            skLineSegment(sketch, "E6.279.0.3", {"start": v(215.9, 99.06) * mm, "end": v(215.9, 78.74) * mm});
            skLineSegment(sketch, "E6.282.0.3", {"start": v(93.98, 99.06) * mm, "end": v(93.98, 78.74) * mm});
            skLineSegment(sketch, "E6.285.0.3", {"start": v(93.98, 78.74) * mm, "end": v(119.38, 78.74) * mm});
            skLineSegment(sketch, "E6.288.0.3", {"start": v(337.82, 78.74) * mm, "end": v(363.22, 78.74) * mm});
            skLineSegment(sketch, "E6.291.0.3", {"start": v(215.9, 78.74) * mm, "end": v(241.3, 78.74) * mm});
            skLineSegment(sketch, "E6.294.0.3", {"start": v(149.86, 99.06) * mm, "end": v(149.86, 78.74) * mm});
            skLineSegment(sketch, "E6.297.0.3", {"start": v(27.94, 99.06) * mm, "end": v(27.94, 78.74) * mm});
            skLineSegment(sketch, "E6.300.0.3", {"start": v(271.78, 99.06) * mm, "end": v(271.78, 78.74) * mm});
            skLineSegment(sketch, "E6.303.0.3", {"start": v(124.46, 99.06) * mm, "end": v(149.86, 99.06) * mm});
            skLineSegment(sketch, "E6.306.0.3", {"start": v(2.54, 99.06) * mm, "end": v(27.94, 99.06) * mm});
            skLineSegment(sketch, "E6.309.0.3", {"start": v(246.38, 99.06) * mm, "end": v(271.78, 99.06) * mm});
            skLineSegment(sketch, "E6.312.0.3", {"start": v(124.46, 99.06) * mm, "end": v(124.46, 78.74) * mm});
            skLineSegment(sketch, "E6.315.0.3", {"start": v(2.54, 99.06) * mm, "end": v(2.54, 78.74) * mm});
            skLineSegment(sketch, "E6.318.0.3", {"start": v(368.3, 99.06) * mm, "end": v(368.3, 78.74) * mm});
            skLineSegment(sketch, "E6.321.0.3", {"start": v(246.38, 99.06) * mm, "end": v(246.38, 78.74) * mm});
            skLineSegment(sketch, "E6.324.0.3", {"start": v(124.46, 78.74) * mm, "end": v(149.86, 78.74) * mm});
            skLineSegment(sketch, "E6.327.0.3", {"start": v(2.54, 78.74) * mm, "end": v(27.94, 78.74) * mm});
            skLineSegment(sketch, "E6.330.0.3", {"start": v(246.38, 78.74) * mm, "end": v(271.78, 78.74) * mm});
            skLineSegment(sketch, "E6.333.0.3", {"start": v(276.86, 99.06) * mm, "end": v(302.26, 99.06) * mm});
            skLineSegment(sketch, "E6.336.0.3", {"start": v(154.94, 99.06) * mm, "end": v(180.34, 99.06) * mm});
            skLineSegment(sketch, "E6.339.0.3", {"start": v(33.02, 99.06) * mm, "end": v(58.42, 99.06) * mm});
            skLineSegment(sketch, "E6.342.0.3", {"start": v(180.34, 99.06) * mm, "end": v(180.34, 78.74) * mm});
            skLineSegment(sketch, "E6.345.0.3", {"start": v(58.42, 99.06) * mm, "end": v(58.42, 78.74) * mm});
            skLineSegment(sketch, "E6.348.0.3", {"start": v(302.26, 99.06) * mm, "end": v(302.26, 78.74) * mm});
            skLineSegment(sketch, "E6.351.0.3", {"start": v(276.86, 99.06) * mm, "end": v(276.86, 78.74) * mm});
            skLineSegment(sketch, "E6.354.0.3", {"start": v(154.94, 99.06) * mm, "end": v(154.94, 78.74) * mm});
            skLineSegment(sketch, "E6.357.0.3", {"start": v(33.02, 99.06) * mm, "end": v(33.02, 78.74) * mm});
            skLineSegment(sketch, "E6.360.0.3", {"start": v(-520.7, 99.06) * mm, "end": v(-520.7, 78.74) * mm});
            skLineSegment(sketch, "E6.363.0.3", {"start": v(-332.74, 78.74) * mm, "end": v(-307.34, 78.74) * mm});
            skLineSegment(sketch, "E6.366.0.3", {"start": v(-398.78, 99.06) * mm, "end": v(-398.78, 78.74) * mm});
            skLineSegment(sketch, "E6.369.0.3", {"start": v(-33.02, 99.06) * mm, "end": v(-33.02, 78.74) * mm});
            skLineSegment(sketch, "E6.372.0.3", {"start": v(-88.9, 78.74) * mm, "end": v(-63.5, 78.74) * mm});
            skLineSegment(sketch, "E6.375.0.3", {"start": v(-698.5, 78.74) * mm, "end": v(-673.1, 78.74) * mm});
            skLineSegment(sketch, "E6.378.0.3", {"start": v(-454.66, 78.74) * mm, "end": v(-429.26, 78.74) * mm});
            skLineSegment(sketch, "E6.381.0.3", {"start": v(-642.62, 99.06) * mm, "end": v(-642.62, 78.74) * mm});
            skLineSegment(sketch, "E6.384.0.3", {"start": v(-764.54, 99.06) * mm, "end": v(-764.54, 78.74) * mm});
            skLineSegment(sketch, "E6.387.0.3", {"start": v(-154.94, 99.06) * mm, "end": v(-154.94, 78.74) * mm});
            skLineSegment(sketch, "E6.390.0.3", {"start": v(-210.82, 78.74) * mm, "end": v(-185.42, 78.74) * mm});
            skLineSegment(sketch, "E6.393.0.3", {"start": v(-576.58, 78.74) * mm, "end": v(-551.18, 78.74) * mm});
            skLineSegment(sketch, "E6.396.0.3", {"start": v(-276.86, 99.06) * mm, "end": v(-276.86, 78.74) * mm});
            skLineSegment(sketch, "E6.399.0.3", {"start": v(-886.46, 78.74) * mm, "end": v(-855.98, 78.74) * mm, "construction": true});
            skLineSegment(sketch, "E6.402.0.3", {"start": v(-180.34, 99.06) * mm, "end": v(-154.94, 99.06) * mm});
            skLineSegment(sketch, "E6.405.0.3", {"start": v(-302.26, 99.06) * mm, "end": v(-276.86, 99.06) * mm});
            skLineSegment(sketch, "E6.408.0.3", {"start": v(-424.18, 99.06) * mm, "end": v(-398.78, 99.06) * mm});
            skLineSegment(sketch, "E6.411.0.3", {"start": v(-546.1, 99.06) * mm, "end": v(-520.7, 99.06) * mm});
            skLineSegment(sketch, "E6.414.0.3", {"start": v(-58.42, 99.06) * mm, "end": v(-33.02, 99.06) * mm});
            skLineSegment(sketch, "E6.417.0.3", {"start": v(-668.02, 99.06) * mm, "end": v(-642.62, 99.06) * mm});
            skLineSegment(sketch, "E6.420.0.3", {"start": v(-789.94, 99.06) * mm, "end": v(-764.54, 99.06) * mm});
            skLineSegment(sketch, "E6.423.0.3", {"start": v(-58.42, 99.06) * mm, "end": v(-58.42, 78.74) * mm});
            skLineSegment(sketch, "E6.426.0.3", {"start": v(-668.02, 99.06) * mm, "end": v(-668.02, 78.74) * mm});
            skLineSegment(sketch, "E6.429.0.3", {"start": v(-789.94, 99.06) * mm, "end": v(-789.94, 78.74) * mm});
            skLineSegment(sketch, "E6.432.0.3", {"start": v(-180.34, 99.06) * mm, "end": v(-180.34, 78.74) * mm});
            skLineSegment(sketch, "E6.435.0.3", {"start": v(-302.26, 99.06) * mm, "end": v(-302.26, 78.74) * mm});
            skLineSegment(sketch, "E6.438.0.3", {"start": v(-424.18, 99.06) * mm, "end": v(-424.18, 78.74) * mm});
            skLineSegment(sketch, "E6.441.0.3", {"start": v(-546.1, 99.06) * mm, "end": v(-546.1, 78.74) * mm});
            skLineSegment(sketch, "E6.444.0.3", {"start": v(-668.02, 78.74) * mm, "end": v(-642.62, 78.74) * mm});
            skLineSegment(sketch, "E6.447.0.3", {"start": v(-789.94, 78.74) * mm, "end": v(-764.54, 78.74) * mm});
            skLineSegment(sketch, "E6.450.0.3", {"start": v(-180.34, 78.74) * mm, "end": v(-154.94, 78.74) * mm});
            skLineSegment(sketch, "E6.453.0.3", {"start": v(-302.26, 78.74) * mm, "end": v(-276.86, 78.74) * mm});
            skLineSegment(sketch, "E6.456.0.3", {"start": v(-424.18, 78.74) * mm, "end": v(-398.78, 78.74) * mm});
            skLineSegment(sketch, "E6.459.0.3", {"start": v(-546.1, 78.74) * mm, "end": v(-520.7, 78.74) * mm});
            skLineSegment(sketch, "E6.462.0.3", {"start": v(-58.42, 78.74) * mm, "end": v(-33.02, 78.74) * mm});
            skLineSegment(sketch, "E6.465.0.3", {"start": v(-612.14, 99.06) * mm, "end": v(-612.14, 78.74) * mm});
            skLineSegment(sketch, "E6.468.0.3", {"start": v(-734.06, 99.06) * mm, "end": v(-734.06, 78.74) * mm});
            skLineSegment(sketch, "E6.471.0.3", {"start": v(-124.46, 99.06) * mm, "end": v(-124.46, 78.74) * mm});
            skLineSegment(sketch, "E6.474.0.3", {"start": v(-246.38, 99.06) * mm, "end": v(-246.38, 78.74) * mm});
            skLineSegment(sketch, "E6.477.0.3", {"start": v(-368.3, 99.06) * mm, "end": v(-368.3, 78.74) * mm});
            skLineSegment(sketch, "E6.480.0.3", {"start": v(-490.22, 99.06) * mm, "end": v(-490.22, 78.74) * mm});
            skLineSegment(sketch, "E6.483.0.3", {"start": v(-2.54, 99.06) * mm, "end": v(-2.54, 78.74) * mm});
            skLineSegment(sketch, "E6.486.0.3", {"start": v(-637.54, 99.06) * mm, "end": v(-612.14, 99.06) * mm});
            skLineSegment(sketch, "E6.489.0.3", {"start": v(-759.46, 99.06) * mm, "end": v(-734.06, 99.06) * mm});
            skLineSegment(sketch, "E6.492.0.3", {"start": v(-149.86, 99.06) * mm, "end": v(-124.46, 99.06) * mm});
            skLineSegment(sketch, "E6.495.0.3", {"start": v(-271.78, 99.06) * mm, "end": v(-246.38, 99.06) * mm});
            skLineSegment(sketch, "E6.498.0.3", {"start": v(-393.7, 99.06) * mm, "end": v(-368.3, 99.06) * mm});
            skLineSegment(sketch, "E6.501.0.3", {"start": v(-515.62, 99.06) * mm, "end": v(-490.22, 99.06) * mm});
            skLineSegment(sketch, "E6.504.0.3", {"start": v(-27.94, 99.06) * mm, "end": v(-2.54, 99.06) * mm});
            skLineSegment(sketch, "E6.507.0.3", {"start": v(-637.54, 99.06) * mm, "end": v(-637.54, 78.74) * mm});
            skLineSegment(sketch, "E6.510.0.3", {"start": v(-759.46, 99.06) * mm, "end": v(-759.46, 78.74) * mm});
            skLineSegment(sketch, "E6.513.0.3", {"start": v(-149.86, 99.06) * mm, "end": v(-149.86, 78.74) * mm});
            skLineSegment(sketch, "E6.516.0.3", {"start": v(-271.78, 99.06) * mm, "end": v(-271.78, 78.74) * mm});
            skLineSegment(sketch, "E6.519.0.3", {"start": v(-393.7, 99.06) * mm, "end": v(-393.7, 78.74) * mm});
            skLineSegment(sketch, "E6.522.0.3", {"start": v(-515.62, 99.06) * mm, "end": v(-515.62, 78.74) * mm});
            skLineSegment(sketch, "E6.525.0.3", {"start": v(-27.94, 99.06) * mm, "end": v(-27.94, 78.74) * mm});
            skLineSegment(sketch, "E6.528.0.3", {"start": v(-393.7, 78.74) * mm, "end": v(-368.3, 78.74) * mm});
            skLineSegment(sketch, "E6.531.0.3", {"start": v(-515.62, 78.74) * mm, "end": v(-490.22, 78.74) * mm});
            skLineSegment(sketch, "E6.534.0.3", {"start": v(-637.54, 78.74) * mm, "end": v(-612.14, 78.74) * mm});
            skLineSegment(sketch, "E6.537.0.3", {"start": v(-759.46, 78.74) * mm, "end": v(-734.06, 78.74) * mm});
            skLineSegment(sketch, "E6.540.0.3", {"start": v(-27.94, 78.74) * mm, "end": v(-2.54, 78.74) * mm});
            skLineSegment(sketch, "E6.543.0.3", {"start": v(-149.86, 78.74) * mm, "end": v(-124.46, 78.74) * mm});
            skLineSegment(sketch, "E6.546.0.3", {"start": v(-271.78, 78.74) * mm, "end": v(-246.38, 78.74) * mm});
            skLineSegment(sketch, "E6.549.0.3", {"start": v(-337.82, 99.06) * mm, "end": v(-337.82, 78.74) * mm});
            skLineSegment(sketch, "E6.552.0.3", {"start": v(-459.74, 99.06) * mm, "end": v(-459.74, 78.74) * mm});
            skLineSegment(sketch, "E6.555.0.3", {"start": v(-581.66, 99.06) * mm, "end": v(-581.66, 78.74) * mm});
            skLineSegment(sketch, "E6.558.0.3", {"start": v(-703.58, 99.06) * mm, "end": v(-703.58, 78.74) * mm});
            skLineSegment(sketch, "E6.561.0.3", {"start": v(-93.98, 99.06) * mm, "end": v(-93.98, 78.74) * mm});
            skLineSegment(sketch, "E6.564.0.3", {"start": v(-215.9, 99.06) * mm, "end": v(-215.9, 78.74) * mm});
            skLineSegment(sketch, "E6.567.0.3", {"start": v(-363.22, 99.06) * mm, "end": v(-337.82, 99.06) * mm});
            skLineSegment(sketch, "E6.570.0.3", {"start": v(-485.14, 99.06) * mm, "end": v(-459.74, 99.06) * mm});
            skLineSegment(sketch, "E6.573.0.3", {"start": v(-607.06, 99.06) * mm, "end": v(-581.66, 99.06) * mm});
            skLineSegment(sketch, "E6.576.0.3", {"start": v(-728.98, 99.06) * mm, "end": v(-703.58, 99.06) * mm});
            skLineSegment(sketch, "E6.579.0.3", {"start": v(-119.38, 99.06) * mm, "end": v(-93.98, 99.06) * mm});
            skLineSegment(sketch, "E6.582.0.3", {"start": v(-241.3, 99.06) * mm, "end": v(-215.9, 99.06) * mm});
            skLineSegment(sketch, "E6.585.0.3", {"start": v(-363.22, 99.06) * mm, "end": v(-363.22, 78.74) * mm});
            skLineSegment(sketch, "E6.588.0.3", {"start": v(-485.14, 99.06) * mm, "end": v(-485.14, 78.74) * mm});
            skLineSegment(sketch, "E6.591.0.3", {"start": v(-607.06, 99.06) * mm, "end": v(-607.06, 78.74) * mm});
            skLineSegment(sketch, "E6.594.0.3", {"start": v(-728.98, 99.06) * mm, "end": v(-728.98, 78.74) * mm});
            skLineSegment(sketch, "E6.597.0.3", {"start": v(-119.38, 99.06) * mm, "end": v(-119.38, 78.74) * mm});
            skLineSegment(sketch, "E6.600.0.3", {"start": v(-241.3, 99.06) * mm, "end": v(-241.3, 78.74) * mm});
            skLineSegment(sketch, "E6.603.0.3", {"start": v(-363.22, 78.74) * mm, "end": v(-337.82, 78.74) * mm});
            skLineSegment(sketch, "E6.606.0.3", {"start": v(-485.14, 78.74) * mm, "end": v(-459.74, 78.74) * mm});
            skLineSegment(sketch, "E6.609.0.3", {"start": v(-607.06, 78.74) * mm, "end": v(-581.66, 78.74) * mm});
            skLineSegment(sketch, "E6.612.0.3", {"start": v(-728.98, 78.74) * mm, "end": v(-703.58, 78.74) * mm});
            skLineSegment(sketch, "E6.615.0.3", {"start": v(-119.38, 78.74) * mm, "end": v(-93.98, 78.74) * mm});
            skLineSegment(sketch, "E6.618.0.3", {"start": v(-241.3, 78.74) * mm, "end": v(-215.9, 78.74) * mm});
            skLineSegment(sketch, "E6.621.0.3", {"start": v(-698.5, 99.06) * mm, "end": v(-673.1, 99.06) * mm});
            skLineSegment(sketch, "E6.624.0.3", {"start": v(-210.82, 99.06) * mm, "end": v(-185.42, 99.06) * mm});
            skLineSegment(sketch, "E6.627.0.3", {"start": v(-332.74, 99.06) * mm, "end": v(-307.34, 99.06) * mm});
            skLineSegment(sketch, "E6.630.0.3", {"start": v(-454.66, 99.06) * mm, "end": v(-429.26, 99.06) * mm});
            skLineSegment(sketch, "E6.633.0.3", {"start": v(-576.58, 99.06) * mm, "end": v(-551.18, 99.06) * mm});
            skLineSegment(sketch, "E6.636.0.3", {"start": v(-88.9, 99.06) * mm, "end": v(-63.5, 99.06) * mm});
            skLineSegment(sketch, "E6.639.0.3", {"start": v(-820.42, 99.06) * mm, "end": v(-795.02, 99.06) * mm});
            skLineSegment(sketch, "E6.642.0.3", {"start": v(-820.42, 99.06) * mm, "end": v(-820.42, 78.74) * mm});
            skLineSegment(sketch, "E6.645.0.3", {"start": v(-820.42, 78.74) * mm, "end": v(-795.02, 78.74) * mm});
            skLineSegment(sketch, "E6.648.0.3", {"start": v(-911.86, 99.06) * mm, "end": v(-886.46, 99.06) * mm});
            skLineSegment(sketch, "E6.651.0.3", {"start": v(-911.86, 78.74) * mm, "end": v(-886.46, 78.74) * mm});
            skLineSegment(sketch, "E6.654.0.3", {"start": v(-911.86, 99.06) * mm, "end": v(-911.86, 78.74) * mm});
            skLineSegment(sketch, "E6.657.0.3", {"start": v(-886.46, 99.06) * mm, "end": v(-886.46, 78.74) * mm});
            skLineSegment(sketch, "E6.660.0.3", {"start": v(-855.98, 99.06) * mm, "end": v(-855.98, 78.74) * mm});
            skLineSegment(sketch, "E6.663.0.3", {"start": v(-881.38, 99.06) * mm, "end": v(-855.98, 99.06) * mm});
            skLineSegment(sketch, "E6.666.0.3", {"start": v(-881.38, 99.06) * mm, "end": v(-881.38, 78.74) * mm});
            skLineSegment(sketch, "E6.669.0.3", {"start": v(-825.5, 99.06) * mm, "end": v(-825.5, 78.74) * mm});
            skLineSegment(sketch, "E6.672.0.3", {"start": v(-850.9, 99.06) * mm, "end": v(-825.5, 99.06) * mm});
            skLineSegment(sketch, "E6.675.0.3", {"start": v(-307.34, 99.06) * mm, "end": v(-307.34, 78.74) * mm});
            skLineSegment(sketch, "E6.678.0.3", {"start": v(-850.9, 99.06) * mm, "end": v(-850.9, 78.74) * mm});
            skLineSegment(sketch, "E6.681.0.3", {"start": v(-429.26, 99.06) * mm, "end": v(-429.26, 78.74) * mm});
            skLineSegment(sketch, "E6.684.0.3", {"start": v(-551.18, 99.06) * mm, "end": v(-551.18, 78.74) * mm});
            skLineSegment(sketch, "E6.687.0.3", {"start": v(-673.1, 99.06) * mm, "end": v(-673.1, 78.74) * mm});
            skLineSegment(sketch, "E6.690.0.3", {"start": v(-850.9, 78.74) * mm, "end": v(-825.5, 78.74) * mm});
            skLineSegment(sketch, "E6.693.0.3", {"start": v(-63.5, 99.06) * mm, "end": v(-63.5, 78.74) * mm});
            skLineSegment(sketch, "E6.696.0.3", {"start": v(-185.42, 99.06) * mm, "end": v(-185.42, 78.74) * mm});
            skLineSegment(sketch, "E6.699.0.3", {"start": v(-795.02, 99.06) * mm, "end": v(-795.02, 78.74) * mm});
            skLineSegment(sketch, "E6.702.0.3", {"start": v(-698.5, 99.06) * mm, "end": v(-698.5, 78.74) * mm});
            skLineSegment(sketch, "E6.705.0.3", {"start": v(-210.82, 99.06) * mm, "end": v(-210.82, 78.74) * mm});
            skLineSegment(sketch, "E6.708.0.3", {"start": v(-332.74, 99.06) * mm, "end": v(-332.74, 78.74) * mm});
            skLineSegment(sketch, "E6.711.0.3", {"start": v(-454.66, 99.06) * mm, "end": v(-454.66, 78.74) * mm});
            skLineSegment(sketch, "E6.714.0.3", {"start": v(-576.58, 99.06) * mm, "end": v(-576.58, 78.74) * mm});
            skLineSegment(sketch, "E6.717.0.3", {"start": v(-88.9, 99.06) * mm, "end": v(-88.9, 78.74) * mm});
            skLineSegment(sketch, "E6.720.0.3", {"start": v(-881.38, 78.74) * mm, "end": v(-855.98, 78.74) * mm});
            skLineSegment(sketch, "E6.0.0.4", {"start": v(886.46, 53.34) * mm, "end": v(911.86, 53.34) * mm});
            skLineSegment(sketch, "E6.3.0.4", {"start": v(911.86, 73.66) * mm, "end": v(911.86, 53.34) * mm});
            skLineSegment(sketch, "E6.6.0.4", {"start": v(886.46, 73.66) * mm, "end": v(911.86, 73.66) * mm});
            skLineSegment(sketch, "E6.9.0.4", {"start": v(886.46, 73.66) * mm, "end": v(886.46, 53.34) * mm});
            skLineSegment(sketch, "E6.12.0.4", {"start": v(881.38, 73.66) * mm, "end": v(881.38, 53.34) * mm});
            skLineSegment(sketch, "E6.15.0.4", {"start": v(855.98, 73.66) * mm, "end": v(881.38, 73.66) * mm});
            skLineSegment(sketch, "E6.18.0.4", {"start": v(855.98, 53.34) * mm, "end": v(881.38, 53.34) * mm});
            skLineSegment(sketch, "E6.21.0.4", {"start": v(855.98, 73.66) * mm, "end": v(855.98, 53.34) * mm});
            skLineSegment(sketch, "E6.24.0.4", {"start": v(520.7, 53.34) * mm, "end": v(546.1, 53.34) * mm});
            skLineSegment(sketch, "E6.27.0.4", {"start": v(398.78, 53.34) * mm, "end": v(424.18, 53.34) * mm});
            skLineSegment(sketch, "E6.30.0.4", {"start": v(820.42, 73.66) * mm, "end": v(820.42, 53.34) * mm});
            skLineSegment(sketch, "E6.33.0.4", {"start": v(642.62, 53.34) * mm, "end": v(668.02, 53.34) * mm});
            skLineSegment(sketch, "E6.36.0.4", {"start": v(764.54, 53.34) * mm, "end": v(789.94, 53.34) * mm});
            skLineSegment(sketch, "E6.39.0.4", {"start": v(698.5, 73.66) * mm, "end": v(698.5, 53.34) * mm});
            skLineSegment(sketch, "E6.42.0.4", {"start": v(576.58, 73.66) * mm, "end": v(576.58, 53.34) * mm});
            skLineSegment(sketch, "E6.45.0.4", {"start": v(454.66, 73.66) * mm, "end": v(454.66, 53.34) * mm});
            skLineSegment(sketch, "E6.48.0.4", {"start": v(795.02, 73.66) * mm, "end": v(820.42, 73.66) * mm});
            skLineSegment(sketch, "E6.51.0.4", {"start": v(673.1, 73.66) * mm, "end": v(698.5, 73.66) * mm});
            skLineSegment(sketch, "E6.54.0.4", {"start": v(551.18, 73.66) * mm, "end": v(576.58, 73.66) * mm});
            skLineSegment(sketch, "E6.57.0.4", {"start": v(429.26, 73.66) * mm, "end": v(454.66, 73.66) * mm});
            skLineSegment(sketch, "E6.60.0.4", {"start": v(795.02, 73.66) * mm, "end": v(795.02, 53.34) * mm});
            skLineSegment(sketch, "E6.63.0.4", {"start": v(673.1, 73.66) * mm, "end": v(673.1, 53.34) * mm});
            skLineSegment(sketch, "E6.66.0.4", {"start": v(551.18, 73.66) * mm, "end": v(551.18, 53.34) * mm});
            skLineSegment(sketch, "E6.69.0.4", {"start": v(429.26, 73.66) * mm, "end": v(429.26, 53.34) * mm});
            skLineSegment(sketch, "E6.72.0.4", {"start": v(795.02, 53.34) * mm, "end": v(820.42, 53.34) * mm});
            skLineSegment(sketch, "E6.75.0.4", {"start": v(673.1, 53.34) * mm, "end": v(698.5, 53.34) * mm});
            skLineSegment(sketch, "E6.78.0.4", {"start": v(551.18, 53.34) * mm, "end": v(576.58, 53.34) * mm});
            skLineSegment(sketch, "E6.81.0.4", {"start": v(429.26, 53.34) * mm, "end": v(454.66, 53.34) * mm});
            skLineSegment(sketch, "E6.84.0.4", {"start": v(850.9, 73.66) * mm, "end": v(850.9, 53.34) * mm});
            skLineSegment(sketch, "E6.87.0.4", {"start": v(728.98, 73.66) * mm, "end": v(728.98, 53.34) * mm});
            skLineSegment(sketch, "E6.90.0.4", {"start": v(607.06, 73.66) * mm, "end": v(607.06, 53.34) * mm});
            skLineSegment(sketch, "E6.93.0.4", {"start": v(485.14, 73.66) * mm, "end": v(485.14, 53.34) * mm});
            skLineSegment(sketch, "E6.96.0.4", {"start": v(825.5, 73.66) * mm, "end": v(850.9, 73.66) * mm});
            skLineSegment(sketch, "E6.99.0.4", {"start": v(703.58, 73.66) * mm, "end": v(728.98, 73.66) * mm});
            skLineSegment(sketch, "E6.102.0.4", {"start": v(581.66, 73.66) * mm, "end": v(607.06, 73.66) * mm});
            skLineSegment(sketch, "E6.105.0.4", {"start": v(459.74, 73.66) * mm, "end": v(485.14, 73.66) * mm});
            skLineSegment(sketch, "E6.108.0.4", {"start": v(825.5, 73.66) * mm, "end": v(825.5, 53.34) * mm});
            skLineSegment(sketch, "E6.111.0.4", {"start": v(703.58, 73.66) * mm, "end": v(703.58, 53.34) * mm});
            skLineSegment(sketch, "E6.114.0.4", {"start": v(581.66, 73.66) * mm, "end": v(581.66, 53.34) * mm});
            skLineSegment(sketch, "E6.117.0.4", {"start": v(459.74, 73.66) * mm, "end": v(459.74, 53.34) * mm});
            skLineSegment(sketch, "E6.120.0.4", {"start": v(581.66, 53.34) * mm, "end": v(607.06, 53.34) * mm});
            skLineSegment(sketch, "E6.123.0.4", {"start": v(459.74, 53.34) * mm, "end": v(485.14, 53.34) * mm});
            skLineSegment(sketch, "E6.126.0.4", {"start": v(825.5, 53.34) * mm, "end": v(850.9, 53.34) * mm});
            skLineSegment(sketch, "E6.129.0.4", {"start": v(703.58, 53.34) * mm, "end": v(728.98, 53.34) * mm});
            skLineSegment(sketch, "E6.132.0.4", {"start": v(637.54, 73.66) * mm, "end": v(637.54, 53.34) * mm});
            skLineSegment(sketch, "E6.135.0.4", {"start": v(515.62, 73.66) * mm, "end": v(515.62, 53.34) * mm});
            skLineSegment(sketch, "E6.138.0.4", {"start": v(393.7, 73.66) * mm, "end": v(393.7, 53.34) * mm});
            skLineSegment(sketch, "E6.141.0.4", {"start": v(759.46, 73.66) * mm, "end": v(759.46, 53.34) * mm});
            skLineSegment(sketch, "E6.144.0.4", {"start": v(612.14, 73.66) * mm, "end": v(637.54, 73.66) * mm});
            skLineSegment(sketch, "E6.147.0.4", {"start": v(490.22, 73.66) * mm, "end": v(515.62, 73.66) * mm});
            skLineSegment(sketch, "E6.150.0.4", {"start": v(368.3, 73.66) * mm, "end": v(393.7, 73.66) * mm});
            skLineSegment(sketch, "E6.153.0.4", {"start": v(734.06, 73.66) * mm, "end": v(759.46, 73.66) * mm});
            skLineSegment(sketch, "E6.156.0.4", {"start": v(612.14, 73.66) * mm, "end": v(612.14, 53.34) * mm});
            skLineSegment(sketch, "E6.159.0.4", {"start": v(490.22, 73.66) * mm, "end": v(490.22, 53.34) * mm});
            skLineSegment(sketch, "E6.162.0.4", {"start": v(734.06, 73.66) * mm, "end": v(734.06, 53.34) * mm});
            skLineSegment(sketch, "E6.165.0.4", {"start": v(612.14, 53.34) * mm, "end": v(637.54, 53.34) * mm});
            skLineSegment(sketch, "E6.168.0.4", {"start": v(490.22, 53.34) * mm, "end": v(515.62, 53.34) * mm});
            skLineSegment(sketch, "E6.171.0.4", {"start": v(368.3, 53.34) * mm, "end": v(393.7, 53.34) * mm});
            skLineSegment(sketch, "E6.174.0.4", {"start": v(734.06, 53.34) * mm, "end": v(759.46, 53.34) * mm});
            skLineSegment(sketch, "E6.177.0.4", {"start": v(764.54, 73.66) * mm, "end": v(789.94, 73.66) * mm});
            skLineSegment(sketch, "E6.180.0.4", {"start": v(642.62, 73.66) * mm, "end": v(668.02, 73.66) * mm});
            skLineSegment(sketch, "E6.183.0.4", {"start": v(520.7, 73.66) * mm, "end": v(546.1, 73.66) * mm});
            skLineSegment(sketch, "E6.186.0.4", {"start": v(398.78, 73.66) * mm, "end": v(424.18, 73.66) * mm});
            skLineSegment(sketch, "E6.189.0.4", {"start": v(668.02, 73.66) * mm, "end": v(668.02, 53.34) * mm});
            skLineSegment(sketch, "E6.192.0.4", {"start": v(546.1, 73.66) * mm, "end": v(546.1, 53.34) * mm});
            skLineSegment(sketch, "E6.195.0.4", {"start": v(424.18, 73.66) * mm, "end": v(424.18, 53.34) * mm});
            skLineSegment(sketch, "E6.198.0.4", {"start": v(789.94, 73.66) * mm, "end": v(789.94, 53.34) * mm});
            skLineSegment(sketch, "E6.201.0.4", {"start": v(764.54, 73.66) * mm, "end": v(764.54, 53.34) * mm});
            skLineSegment(sketch, "E6.204.0.4", {"start": v(642.62, 73.66) * mm, "end": v(642.62, 53.34) * mm});
            skLineSegment(sketch, "E6.207.0.4", {"start": v(520.7, 73.66) * mm, "end": v(520.7, 53.34) * mm});
            skLineSegment(sketch, "E6.210.0.4", {"start": v(398.78, 73.66) * mm, "end": v(398.78, 53.34) * mm});
            skLineSegment(sketch, "E6.213.0.4", {"start": v(332.74, 73.66) * mm, "end": v(332.74, 53.34) * mm});
            skLineSegment(sketch, "E6.216.0.4", {"start": v(210.82, 73.66) * mm, "end": v(210.82, 53.34) * mm});
            skLineSegment(sketch, "E6.219.0.4", {"start": v(88.9, 73.66) * mm, "end": v(88.9, 53.34) * mm});
            skLineSegment(sketch, "E6.222.0.4", {"start": v(33.02, 53.34) * mm, "end": v(58.42, 53.34) * mm});
            skLineSegment(sketch, "E6.225.0.4", {"start": v(154.94, 53.34) * mm, "end": v(180.34, 53.34) * mm});
            skLineSegment(sketch, "E6.228.0.4", {"start": v(276.86, 53.34) * mm, "end": v(302.26, 53.34) * mm});
            skLineSegment(sketch, "E6.231.0.4", {"start": v(307.34, 73.66) * mm, "end": v(332.74, 73.66) * mm});
            skLineSegment(sketch, "E6.234.0.4", {"start": v(185.42, 73.66) * mm, "end": v(210.82, 73.66) * mm});
            skLineSegment(sketch, "E6.237.0.4", {"start": v(63.5, 73.66) * mm, "end": v(88.9, 73.66) * mm});
            skLineSegment(sketch, "E6.240.0.4", {"start": v(307.34, 73.66) * mm, "end": v(307.34, 53.34) * mm});
            skLineSegment(sketch, "E6.243.0.4", {"start": v(185.42, 73.66) * mm, "end": v(185.42, 53.34) * mm});
            skLineSegment(sketch, "E6.246.0.4", {"start": v(63.5, 73.66) * mm, "end": v(63.5, 53.34) * mm});
            skLineSegment(sketch, "E6.249.0.4", {"start": v(307.34, 53.34) * mm, "end": v(332.74, 53.34) * mm});
            skLineSegment(sketch, "E6.252.0.4", {"start": v(185.42, 53.34) * mm, "end": v(210.82, 53.34) * mm});
            skLineSegment(sketch, "E6.255.0.4", {"start": v(63.5, 53.34) * mm, "end": v(88.9, 53.34) * mm});
            skLineSegment(sketch, "E6.258.0.4", {"start": v(363.22, 73.66) * mm, "end": v(363.22, 53.34) * mm});
            skLineSegment(sketch, "E6.261.0.4", {"start": v(241.3, 73.66) * mm, "end": v(241.3, 53.34) * mm});
            skLineSegment(sketch, "E6.264.0.4", {"start": v(119.38, 73.66) * mm, "end": v(119.38, 53.34) * mm});
            skLineSegment(sketch, "E6.267.0.4", {"start": v(337.82, 73.66) * mm, "end": v(363.22, 73.66) * mm});
            skLineSegment(sketch, "E6.270.0.4", {"start": v(215.9, 73.66) * mm, "end": v(241.3, 73.66) * mm});
            skLineSegment(sketch, "E6.273.0.4", {"start": v(93.98, 73.66) * mm, "end": v(119.38, 73.66) * mm});
            skLineSegment(sketch, "E6.276.0.4", {"start": v(337.82, 73.66) * mm, "end": v(337.82, 53.34) * mm});
            skLineSegment(sketch, "E6.279.0.4", {"start": v(215.9, 73.66) * mm, "end": v(215.9, 53.34) * mm});
            skLineSegment(sketch, "E6.282.0.4", {"start": v(93.98, 73.66) * mm, "end": v(93.98, 53.34) * mm});
            skLineSegment(sketch, "E6.285.0.4", {"start": v(93.98, 53.34) * mm, "end": v(119.38, 53.34) * mm});
            skLineSegment(sketch, "E6.288.0.4", {"start": v(337.82, 53.34) * mm, "end": v(363.22, 53.34) * mm});
            skLineSegment(sketch, "E6.291.0.4", {"start": v(215.9, 53.34) * mm, "end": v(241.3, 53.34) * mm});
            skLineSegment(sketch, "E6.294.0.4", {"start": v(149.86, 73.66) * mm, "end": v(149.86, 53.34) * mm});
            skLineSegment(sketch, "E6.297.0.4", {"start": v(27.94, 73.66) * mm, "end": v(27.94, 53.34) * mm});
            skLineSegment(sketch, "E6.300.0.4", {"start": v(271.78, 73.66) * mm, "end": v(271.78, 53.34) * mm});
            skLineSegment(sketch, "E6.303.0.4", {"start": v(124.46, 73.66) * mm, "end": v(149.86, 73.66) * mm});
            skLineSegment(sketch, "E6.306.0.4", {"start": v(2.54, 73.66) * mm, "end": v(27.94, 73.66) * mm});
            skLineSegment(sketch, "E6.309.0.4", {"start": v(246.38, 73.66) * mm, "end": v(271.78, 73.66) * mm});
            skLineSegment(sketch, "E6.312.0.4", {"start": v(124.46, 73.66) * mm, "end": v(124.46, 53.34) * mm});
            skLineSegment(sketch, "E6.315.0.4", {"start": v(2.54, 73.66) * mm, "end": v(2.54, 53.34) * mm});
            skLineSegment(sketch, "E6.318.0.4", {"start": v(368.3, 73.66) * mm, "end": v(368.3, 53.34) * mm});
            skLineSegment(sketch, "E6.321.0.4", {"start": v(246.38, 73.66) * mm, "end": v(246.38, 53.34) * mm});
            skLineSegment(sketch, "E6.324.0.4", {"start": v(124.46, 53.34) * mm, "end": v(149.86, 53.34) * mm});
            skLineSegment(sketch, "E6.327.0.4", {"start": v(2.54, 53.34) * mm, "end": v(27.94, 53.34) * mm});
            skLineSegment(sketch, "E6.330.0.4", {"start": v(246.38, 53.34) * mm, "end": v(271.78, 53.34) * mm});
            skLineSegment(sketch, "E6.333.0.4", {"start": v(276.86, 73.66) * mm, "end": v(302.26, 73.66) * mm});
            skLineSegment(sketch, "E6.336.0.4", {"start": v(154.94, 73.66) * mm, "end": v(180.34, 73.66) * mm});
            skLineSegment(sketch, "E6.339.0.4", {"start": v(33.02, 73.66) * mm, "end": v(58.42, 73.66) * mm});
            skLineSegment(sketch, "E6.342.0.4", {"start": v(180.34, 73.66) * mm, "end": v(180.34, 53.34) * mm});
            skLineSegment(sketch, "E6.345.0.4", {"start": v(58.42, 73.66) * mm, "end": v(58.42, 53.34) * mm});
            skLineSegment(sketch, "E6.348.0.4", {"start": v(302.26, 73.66) * mm, "end": v(302.26, 53.34) * mm});
            skLineSegment(sketch, "E6.351.0.4", {"start": v(276.86, 73.66) * mm, "end": v(276.86, 53.34) * mm});
            skLineSegment(sketch, "E6.354.0.4", {"start": v(154.94, 73.66) * mm, "end": v(154.94, 53.34) * mm});
            skLineSegment(sketch, "E6.357.0.4", {"start": v(33.02, 73.66) * mm, "end": v(33.02, 53.34) * mm});
            skLineSegment(sketch, "E6.360.0.4", {"start": v(-520.7, 73.66) * mm, "end": v(-520.7, 53.34) * mm});
            skLineSegment(sketch, "E6.363.0.4", {"start": v(-332.74, 53.34) * mm, "end": v(-307.34, 53.34) * mm});
            skLineSegment(sketch, "E6.366.0.4", {"start": v(-398.78, 73.66) * mm, "end": v(-398.78, 53.34) * mm});
            skLineSegment(sketch, "E6.369.0.4", {"start": v(-33.02, 73.66) * mm, "end": v(-33.02, 53.34) * mm});
            skLineSegment(sketch, "E6.372.0.4", {"start": v(-88.9, 53.34) * mm, "end": v(-63.5, 53.34) * mm});
            skLineSegment(sketch, "E6.375.0.4", {"start": v(-698.5, 53.34) * mm, "end": v(-673.1, 53.34) * mm});
            skLineSegment(sketch, "E6.378.0.4", {"start": v(-454.66, 53.34) * mm, "end": v(-429.26, 53.34) * mm});
            skLineSegment(sketch, "E6.381.0.4", {"start": v(-642.62, 73.66) * mm, "end": v(-642.62, 53.34) * mm});
            skLineSegment(sketch, "E6.384.0.4", {"start": v(-764.54, 73.66) * mm, "end": v(-764.54, 53.34) * mm});
            skLineSegment(sketch, "E6.387.0.4", {"start": v(-154.94, 73.66) * mm, "end": v(-154.94, 53.34) * mm});
            skLineSegment(sketch, "E6.390.0.4", {"start": v(-210.82, 53.34) * mm, "end": v(-185.42, 53.34) * mm});
            skLineSegment(sketch, "E6.393.0.4", {"start": v(-576.58, 53.34) * mm, "end": v(-551.18, 53.34) * mm});
            skLineSegment(sketch, "E6.396.0.4", {"start": v(-276.86, 73.66) * mm, "end": v(-276.86, 53.34) * mm});
            skLineSegment(sketch, "E6.399.0.4", {"start": v(-886.46, 53.34) * mm, "end": v(-855.98, 53.34) * mm, "construction": true});
            skLineSegment(sketch, "E6.402.0.4", {"start": v(-180.34, 73.66) * mm, "end": v(-154.94, 73.66) * mm});
            skLineSegment(sketch, "E6.405.0.4", {"start": v(-302.26, 73.66) * mm, "end": v(-276.86, 73.66) * mm});
            skLineSegment(sketch, "E6.408.0.4", {"start": v(-424.18, 73.66) * mm, "end": v(-398.78, 73.66) * mm});
            skLineSegment(sketch, "E6.411.0.4", {"start": v(-546.1, 73.66) * mm, "end": v(-520.7, 73.66) * mm});
            skLineSegment(sketch, "E6.414.0.4", {"start": v(-58.42, 73.66) * mm, "end": v(-33.02, 73.66) * mm});
            skLineSegment(sketch, "E6.417.0.4", {"start": v(-668.02, 73.66) * mm, "end": v(-642.62, 73.66) * mm});
            skLineSegment(sketch, "E6.420.0.4", {"start": v(-789.94, 73.66) * mm, "end": v(-764.54, 73.66) * mm});
            skLineSegment(sketch, "E6.423.0.4", {"start": v(-58.42, 73.66) * mm, "end": v(-58.42, 53.34) * mm});
            skLineSegment(sketch, "E6.426.0.4", {"start": v(-668.02, 73.66) * mm, "end": v(-668.02, 53.34) * mm});
            skLineSegment(sketch, "E6.429.0.4", {"start": v(-789.94, 73.66) * mm, "end": v(-789.94, 53.34) * mm});
            skLineSegment(sketch, "E6.432.0.4", {"start": v(-180.34, 73.66) * mm, "end": v(-180.34, 53.34) * mm});
            skLineSegment(sketch, "E6.435.0.4", {"start": v(-302.26, 73.66) * mm, "end": v(-302.26, 53.34) * mm});
            skLineSegment(sketch, "E6.438.0.4", {"start": v(-424.18, 73.66) * mm, "end": v(-424.18, 53.34) * mm});
            skLineSegment(sketch, "E6.441.0.4", {"start": v(-546.1, 73.66) * mm, "end": v(-546.1, 53.34) * mm});
            skLineSegment(sketch, "E6.444.0.4", {"start": v(-668.02, 53.34) * mm, "end": v(-642.62, 53.34) * mm});
            skLineSegment(sketch, "E6.447.0.4", {"start": v(-789.94, 53.34) * mm, "end": v(-764.54, 53.34) * mm});
            skLineSegment(sketch, "E6.450.0.4", {"start": v(-180.34, 53.34) * mm, "end": v(-154.94, 53.34) * mm});
            skLineSegment(sketch, "E6.453.0.4", {"start": v(-302.26, 53.34) * mm, "end": v(-276.86, 53.34) * mm});
            skLineSegment(sketch, "E6.456.0.4", {"start": v(-424.18, 53.34) * mm, "end": v(-398.78, 53.34) * mm});
            skLineSegment(sketch, "E6.459.0.4", {"start": v(-546.1, 53.34) * mm, "end": v(-520.7, 53.34) * mm});
            skLineSegment(sketch, "E6.462.0.4", {"start": v(-58.42, 53.34) * mm, "end": v(-33.02, 53.34) * mm});
            skLineSegment(sketch, "E6.465.0.4", {"start": v(-612.14, 73.66) * mm, "end": v(-612.14, 53.34) * mm});
            skLineSegment(sketch, "E6.468.0.4", {"start": v(-734.06, 73.66) * mm, "end": v(-734.06, 53.34) * mm});
            skLineSegment(sketch, "E6.471.0.4", {"start": v(-124.46, 73.66) * mm, "end": v(-124.46, 53.34) * mm});
            skLineSegment(sketch, "E6.474.0.4", {"start": v(-246.38, 73.66) * mm, "end": v(-246.38, 53.34) * mm});
            skLineSegment(sketch, "E6.477.0.4", {"start": v(-368.3, 73.66) * mm, "end": v(-368.3, 53.34) * mm});
            skLineSegment(sketch, "E6.480.0.4", {"start": v(-490.22, 73.66) * mm, "end": v(-490.22, 53.34) * mm});
            skLineSegment(sketch, "E6.483.0.4", {"start": v(-2.54, 73.66) * mm, "end": v(-2.54, 53.34) * mm});
            skLineSegment(sketch, "E6.486.0.4", {"start": v(-637.54, 73.66) * mm, "end": v(-612.14, 73.66) * mm});
            skLineSegment(sketch, "E6.489.0.4", {"start": v(-759.46, 73.66) * mm, "end": v(-734.06, 73.66) * mm});
            skLineSegment(sketch, "E6.492.0.4", {"start": v(-149.86, 73.66) * mm, "end": v(-124.46, 73.66) * mm});
            skLineSegment(sketch, "E6.495.0.4", {"start": v(-271.78, 73.66) * mm, "end": v(-246.38, 73.66) * mm});
            skLineSegment(sketch, "E6.498.0.4", {"start": v(-393.7, 73.66) * mm, "end": v(-368.3, 73.66) * mm});
            skLineSegment(sketch, "E6.501.0.4", {"start": v(-515.62, 73.66) * mm, "end": v(-490.22, 73.66) * mm});
            skLineSegment(sketch, "E6.504.0.4", {"start": v(-27.94, 73.66) * mm, "end": v(-2.54, 73.66) * mm});
            skLineSegment(sketch, "E6.507.0.4", {"start": v(-637.54, 73.66) * mm, "end": v(-637.54, 53.34) * mm});
            skLineSegment(sketch, "E6.510.0.4", {"start": v(-759.46, 73.66) * mm, "end": v(-759.46, 53.34) * mm});
            skLineSegment(sketch, "E6.513.0.4", {"start": v(-149.86, 73.66) * mm, "end": v(-149.86, 53.34) * mm});
            skLineSegment(sketch, "E6.516.0.4", {"start": v(-271.78, 73.66) * mm, "end": v(-271.78, 53.34) * mm});
            skLineSegment(sketch, "E6.519.0.4", {"start": v(-393.7, 73.66) * mm, "end": v(-393.7, 53.34) * mm});
            skLineSegment(sketch, "E6.522.0.4", {"start": v(-515.62, 73.66) * mm, "end": v(-515.62, 53.34) * mm});
            skLineSegment(sketch, "E6.525.0.4", {"start": v(-27.94, 73.66) * mm, "end": v(-27.94, 53.34) * mm});
            skLineSegment(sketch, "E6.528.0.4", {"start": v(-393.7, 53.34) * mm, "end": v(-368.3, 53.34) * mm});
            skLineSegment(sketch, "E6.531.0.4", {"start": v(-515.62, 53.34) * mm, "end": v(-490.22, 53.34) * mm});
            skLineSegment(sketch, "E6.534.0.4", {"start": v(-637.54, 53.34) * mm, "end": v(-612.14, 53.34) * mm});
            skLineSegment(sketch, "E6.537.0.4", {"start": v(-759.46, 53.34) * mm, "end": v(-734.06, 53.34) * mm});
            skLineSegment(sketch, "E6.540.0.4", {"start": v(-27.94, 53.34) * mm, "end": v(-2.54, 53.34) * mm});
            skLineSegment(sketch, "E6.543.0.4", {"start": v(-149.86, 53.34) * mm, "end": v(-124.46, 53.34) * mm});
            skLineSegment(sketch, "E6.546.0.4", {"start": v(-271.78, 53.34) * mm, "end": v(-246.38, 53.34) * mm});
            skLineSegment(sketch, "E6.549.0.4", {"start": v(-337.82, 73.66) * mm, "end": v(-337.82, 53.34) * mm});
            skLineSegment(sketch, "E6.552.0.4", {"start": v(-459.74, 73.66) * mm, "end": v(-459.74, 53.34) * mm});
            skLineSegment(sketch, "E6.555.0.4", {"start": v(-581.66, 73.66) * mm, "end": v(-581.66, 53.34) * mm});
            skLineSegment(sketch, "E6.558.0.4", {"start": v(-703.58, 73.66) * mm, "end": v(-703.58, 53.34) * mm});
            skLineSegment(sketch, "E6.561.0.4", {"start": v(-93.98, 73.66) * mm, "end": v(-93.98, 53.34) * mm});
            skLineSegment(sketch, "E6.564.0.4", {"start": v(-215.9, 73.66) * mm, "end": v(-215.9, 53.34) * mm});
            skLineSegment(sketch, "E6.567.0.4", {"start": v(-363.22, 73.66) * mm, "end": v(-337.82, 73.66) * mm});
            skLineSegment(sketch, "E6.570.0.4", {"start": v(-485.14, 73.66) * mm, "end": v(-459.74, 73.66) * mm});
            skLineSegment(sketch, "E6.573.0.4", {"start": v(-607.06, 73.66) * mm, "end": v(-581.66, 73.66) * mm});
            skLineSegment(sketch, "E6.576.0.4", {"start": v(-728.98, 73.66) * mm, "end": v(-703.58, 73.66) * mm});
            skLineSegment(sketch, "E6.579.0.4", {"start": v(-119.38, 73.66) * mm, "end": v(-93.98, 73.66) * mm});
            skLineSegment(sketch, "E6.582.0.4", {"start": v(-241.3, 73.66) * mm, "end": v(-215.9, 73.66) * mm});
            skLineSegment(sketch, "E6.585.0.4", {"start": v(-363.22, 73.66) * mm, "end": v(-363.22, 53.34) * mm});
            skLineSegment(sketch, "E6.588.0.4", {"start": v(-485.14, 73.66) * mm, "end": v(-485.14, 53.34) * mm});
            skLineSegment(sketch, "E6.591.0.4", {"start": v(-607.06, 73.66) * mm, "end": v(-607.06, 53.34) * mm});
            skLineSegment(sketch, "E6.594.0.4", {"start": v(-728.98, 73.66) * mm, "end": v(-728.98, 53.34) * mm});
            skLineSegment(sketch, "E6.597.0.4", {"start": v(-119.38, 73.66) * mm, "end": v(-119.38, 53.34) * mm});
            skLineSegment(sketch, "E6.600.0.4", {"start": v(-241.3, 73.66) * mm, "end": v(-241.3, 53.34) * mm});
            skLineSegment(sketch, "E6.603.0.4", {"start": v(-363.22, 53.34) * mm, "end": v(-337.82, 53.34) * mm});
            skLineSegment(sketch, "E6.606.0.4", {"start": v(-485.14, 53.34) * mm, "end": v(-459.74, 53.34) * mm});
            skLineSegment(sketch, "E6.609.0.4", {"start": v(-607.06, 53.34) * mm, "end": v(-581.66, 53.34) * mm});
            skLineSegment(sketch, "E6.612.0.4", {"start": v(-728.98, 53.34) * mm, "end": v(-703.58, 53.34) * mm});
            skLineSegment(sketch, "E6.615.0.4", {"start": v(-119.38, 53.34) * mm, "end": v(-93.98, 53.34) * mm});
            skLineSegment(sketch, "E6.618.0.4", {"start": v(-241.3, 53.34) * mm, "end": v(-215.9, 53.34) * mm});
            skLineSegment(sketch, "E6.621.0.4", {"start": v(-698.5, 73.66) * mm, "end": v(-673.1, 73.66) * mm});
            skLineSegment(sketch, "E6.624.0.4", {"start": v(-210.82, 73.66) * mm, "end": v(-185.42, 73.66) * mm});
            skLineSegment(sketch, "E6.627.0.4", {"start": v(-332.74, 73.66) * mm, "end": v(-307.34, 73.66) * mm});
            skLineSegment(sketch, "E6.630.0.4", {"start": v(-454.66, 73.66) * mm, "end": v(-429.26, 73.66) * mm});
            skLineSegment(sketch, "E6.633.0.4", {"start": v(-576.58, 73.66) * mm, "end": v(-551.18, 73.66) * mm});
            skLineSegment(sketch, "E6.636.0.4", {"start": v(-88.9, 73.66) * mm, "end": v(-63.5, 73.66) * mm});
            skLineSegment(sketch, "E6.639.0.4", {"start": v(-820.42, 73.66) * mm, "end": v(-795.02, 73.66) * mm});
            skLineSegment(sketch, "E6.642.0.4", {"start": v(-820.42, 73.66) * mm, "end": v(-820.42, 53.34) * mm});
            skLineSegment(sketch, "E6.645.0.4", {"start": v(-820.42, 53.34) * mm, "end": v(-795.02, 53.34) * mm});
            skLineSegment(sketch, "E6.648.0.4", {"start": v(-911.86, 73.66) * mm, "end": v(-886.46, 73.66) * mm});
            skLineSegment(sketch, "E6.651.0.4", {"start": v(-911.86, 53.34) * mm, "end": v(-886.46, 53.34) * mm});
            skLineSegment(sketch, "E6.654.0.4", {"start": v(-911.86, 73.66) * mm, "end": v(-911.86, 53.34) * mm});
            skLineSegment(sketch, "E6.657.0.4", {"start": v(-886.46, 73.66) * mm, "end": v(-886.46, 53.34) * mm});
            skLineSegment(sketch, "E6.660.0.4", {"start": v(-855.98, 73.66) * mm, "end": v(-855.98, 53.34) * mm});
            skLineSegment(sketch, "E6.663.0.4", {"start": v(-881.38, 73.66) * mm, "end": v(-855.98, 73.66) * mm});
            skLineSegment(sketch, "E6.666.0.4", {"start": v(-881.38, 73.66) * mm, "end": v(-881.38, 53.34) * mm});
            skLineSegment(sketch, "E6.669.0.4", {"start": v(-825.5, 73.66) * mm, "end": v(-825.5, 53.34) * mm});
            skLineSegment(sketch, "E6.672.0.4", {"start": v(-850.9, 73.66) * mm, "end": v(-825.5, 73.66) * mm});
            skLineSegment(sketch, "E6.675.0.4", {"start": v(-307.34, 73.66) * mm, "end": v(-307.34, 53.34) * mm});
            skLineSegment(sketch, "E6.678.0.4", {"start": v(-850.9, 73.66) * mm, "end": v(-850.9, 53.34) * mm});
            skLineSegment(sketch, "E6.681.0.4", {"start": v(-429.26, 73.66) * mm, "end": v(-429.26, 53.34) * mm});
            skLineSegment(sketch, "E6.684.0.4", {"start": v(-551.18, 73.66) * mm, "end": v(-551.18, 53.34) * mm});
            skLineSegment(sketch, "E6.687.0.4", {"start": v(-673.1, 73.66) * mm, "end": v(-673.1, 53.34) * mm});
            skLineSegment(sketch, "E6.690.0.4", {"start": v(-850.9, 53.34) * mm, "end": v(-825.5, 53.34) * mm});
            skLineSegment(sketch, "E6.693.0.4", {"start": v(-63.5, 73.66) * mm, "end": v(-63.5, 53.34) * mm});
            skLineSegment(sketch, "E6.696.0.4", {"start": v(-185.42, 73.66) * mm, "end": v(-185.42, 53.34) * mm});
            skLineSegment(sketch, "E6.699.0.4", {"start": v(-795.02, 73.66) * mm, "end": v(-795.02, 53.34) * mm});
            skLineSegment(sketch, "E6.702.0.4", {"start": v(-698.5, 73.66) * mm, "end": v(-698.5, 53.34) * mm});
            skLineSegment(sketch, "E6.705.0.4", {"start": v(-210.82, 73.66) * mm, "end": v(-210.82, 53.34) * mm});
            skLineSegment(sketch, "E6.708.0.4", {"start": v(-332.74, 73.66) * mm, "end": v(-332.74, 53.34) * mm});
            skLineSegment(sketch, "E6.711.0.4", {"start": v(-454.66, 73.66) * mm, "end": v(-454.66, 53.34) * mm});
            skLineSegment(sketch, "E6.714.0.4", {"start": v(-576.58, 73.66) * mm, "end": v(-576.58, 53.34) * mm});
            skLineSegment(sketch, "E6.717.0.4", {"start": v(-88.9, 73.66) * mm, "end": v(-88.9, 53.34) * mm});
            skLineSegment(sketch, "E6.720.0.4", {"start": v(-881.38, 53.34) * mm, "end": v(-855.98, 53.34) * mm});
            skLineSegment(sketch, "E6.0.0.5", {"start": v(886.46, 27.94) * mm, "end": v(911.86, 27.94) * mm});
            skLineSegment(sketch, "E6.3.0.5", {"start": v(911.86, 48.26) * mm, "end": v(911.86, 27.94) * mm});
            skLineSegment(sketch, "E6.6.0.5", {"start": v(886.46, 48.26) * mm, "end": v(911.86, 48.26) * mm});
            skLineSegment(sketch, "E6.9.0.5", {"start": v(886.46, 48.26) * mm, "end": v(886.46, 27.94) * mm});
            skLineSegment(sketch, "E6.12.0.5", {"start": v(881.38, 48.26) * mm, "end": v(881.38, 27.94) * mm});
            skLineSegment(sketch, "E6.15.0.5", {"start": v(855.98, 48.26) * mm, "end": v(881.38, 48.26) * mm});
            skLineSegment(sketch, "E6.18.0.5", {"start": v(855.98, 27.94) * mm, "end": v(881.38, 27.94) * mm});
            skLineSegment(sketch, "E6.21.0.5", {"start": v(855.98, 48.26) * mm, "end": v(855.98, 27.94) * mm});
            skLineSegment(sketch, "E6.24.0.5", {"start": v(520.7, 27.94) * mm, "end": v(546.1, 27.94) * mm});
            skLineSegment(sketch, "E6.27.0.5", {"start": v(398.78, 27.94) * mm, "end": v(424.18, 27.94) * mm});
            skLineSegment(sketch, "E6.30.0.5", {"start": v(820.42, 48.26) * mm, "end": v(820.42, 27.94) * mm});
            skLineSegment(sketch, "E6.33.0.5", {"start": v(642.62, 27.94) * mm, "end": v(668.02, 27.94) * mm});
            skLineSegment(sketch, "E6.36.0.5", {"start": v(764.54, 27.94) * mm, "end": v(789.94, 27.94) * mm});
            skLineSegment(sketch, "E6.39.0.5", {"start": v(698.5, 48.26) * mm, "end": v(698.5, 27.94) * mm});
            skLineSegment(sketch, "E6.42.0.5", {"start": v(576.58, 48.26) * mm, "end": v(576.58, 27.94) * mm});
            skLineSegment(sketch, "E6.45.0.5", {"start": v(454.66, 48.26) * mm, "end": v(454.66, 27.94) * mm});
            skLineSegment(sketch, "E6.48.0.5", {"start": v(795.02, 48.26) * mm, "end": v(820.42, 48.26) * mm});
            skLineSegment(sketch, "E6.51.0.5", {"start": v(673.1, 48.26) * mm, "end": v(698.5, 48.26) * mm});
            skLineSegment(sketch, "E6.54.0.5", {"start": v(551.18, 48.26) * mm, "end": v(576.58, 48.26) * mm});
            skLineSegment(sketch, "E6.57.0.5", {"start": v(429.26, 48.26) * mm, "end": v(454.66, 48.26) * mm});
            skLineSegment(sketch, "E6.60.0.5", {"start": v(795.02, 48.26) * mm, "end": v(795.02, 27.94) * mm});
            skLineSegment(sketch, "E6.63.0.5", {"start": v(673.1, 48.26) * mm, "end": v(673.1, 27.94) * mm});
            skLineSegment(sketch, "E6.66.0.5", {"start": v(551.18, 48.26) * mm, "end": v(551.18, 27.94) * mm});
            skLineSegment(sketch, "E6.69.0.5", {"start": v(429.26, 48.26) * mm, "end": v(429.26, 27.94) * mm});
            skLineSegment(sketch, "E6.72.0.5", {"start": v(795.02, 27.94) * mm, "end": v(820.42, 27.94) * mm});
            skLineSegment(sketch, "E6.75.0.5", {"start": v(673.1, 27.94) * mm, "end": v(698.5, 27.94) * mm});
            skLineSegment(sketch, "E6.78.0.5", {"start": v(551.18, 27.94) * mm, "end": v(576.58, 27.94) * mm});
            skLineSegment(sketch, "E6.81.0.5", {"start": v(429.26, 27.94) * mm, "end": v(454.66, 27.94) * mm});
            skLineSegment(sketch, "E6.84.0.5", {"start": v(850.9, 48.26) * mm, "end": v(850.9, 27.94) * mm});
            skLineSegment(sketch, "E6.87.0.5", {"start": v(728.98, 48.26) * mm, "end": v(728.98, 27.94) * mm});
            skLineSegment(sketch, "E6.90.0.5", {"start": v(607.06, 48.26) * mm, "end": v(607.06, 27.94) * mm});
            skLineSegment(sketch, "E6.93.0.5", {"start": v(485.14, 48.26) * mm, "end": v(485.14, 27.94) * mm});
            skLineSegment(sketch, "E6.96.0.5", {"start": v(825.5, 48.26) * mm, "end": v(850.9, 48.26) * mm});
            skLineSegment(sketch, "E6.99.0.5", {"start": v(703.58, 48.26) * mm, "end": v(728.98, 48.26) * mm});
            skLineSegment(sketch, "E6.102.0.5", {"start": v(581.66, 48.26) * mm, "end": v(607.06, 48.26) * mm});
            skLineSegment(sketch, "E6.105.0.5", {"start": v(459.74, 48.26) * mm, "end": v(485.14, 48.26) * mm});
            skLineSegment(sketch, "E6.108.0.5", {"start": v(825.5, 48.26) * mm, "end": v(825.5, 27.94) * mm});
            skLineSegment(sketch, "E6.111.0.5", {"start": v(703.58, 48.26) * mm, "end": v(703.58, 27.94) * mm});
            skLineSegment(sketch, "E6.114.0.5", {"start": v(581.66, 48.26) * mm, "end": v(581.66, 27.94) * mm});
            skLineSegment(sketch, "E6.117.0.5", {"start": v(459.74, 48.26) * mm, "end": v(459.74, 27.94) * mm});
            skLineSegment(sketch, "E6.120.0.5", {"start": v(581.66, 27.94) * mm, "end": v(607.06, 27.94) * mm});
            skLineSegment(sketch, "E6.123.0.5", {"start": v(459.74, 27.94) * mm, "end": v(485.14, 27.94) * mm});
            skLineSegment(sketch, "E6.126.0.5", {"start": v(825.5, 27.94) * mm, "end": v(850.9, 27.94) * mm});
            skLineSegment(sketch, "E6.129.0.5", {"start": v(703.58, 27.94) * mm, "end": v(728.98, 27.94) * mm});
            skLineSegment(sketch, "E6.132.0.5", {"start": v(637.54, 48.26) * mm, "end": v(637.54, 27.94) * mm});
            skLineSegment(sketch, "E6.135.0.5", {"start": v(515.62, 48.26) * mm, "end": v(515.62, 27.94) * mm});
            skLineSegment(sketch, "E6.138.0.5", {"start": v(393.7, 48.26) * mm, "end": v(393.7, 27.94) * mm});
            skLineSegment(sketch, "E6.141.0.5", {"start": v(759.46, 48.26) * mm, "end": v(759.46, 27.94) * mm});
            skLineSegment(sketch, "E6.144.0.5", {"start": v(612.14, 48.26) * mm, "end": v(637.54, 48.26) * mm});
            skLineSegment(sketch, "E6.147.0.5", {"start": v(490.22, 48.26) * mm, "end": v(515.62, 48.26) * mm});
            skLineSegment(sketch, "E6.150.0.5", {"start": v(368.3, 48.26) * mm, "end": v(393.7, 48.26) * mm});
            skLineSegment(sketch, "E6.153.0.5", {"start": v(734.06, 48.26) * mm, "end": v(759.46, 48.26) * mm});
            skLineSegment(sketch, "E6.156.0.5", {"start": v(612.14, 48.26) * mm, "end": v(612.14, 27.94) * mm});
            skLineSegment(sketch, "E6.159.0.5", {"start": v(490.22, 48.26) * mm, "end": v(490.22, 27.94) * mm});
            skLineSegment(sketch, "E6.162.0.5", {"start": v(734.06, 48.26) * mm, "end": v(734.06, 27.94) * mm});
            skLineSegment(sketch, "E6.165.0.5", {"start": v(612.14, 27.94) * mm, "end": v(637.54, 27.94) * mm});
            skLineSegment(sketch, "E6.168.0.5", {"start": v(490.22, 27.94) * mm, "end": v(515.62, 27.94) * mm});
            skLineSegment(sketch, "E6.171.0.5", {"start": v(368.3, 27.94) * mm, "end": v(393.7, 27.94) * mm});
            skLineSegment(sketch, "E6.174.0.5", {"start": v(734.06, 27.94) * mm, "end": v(759.46, 27.94) * mm});
            skLineSegment(sketch, "E6.177.0.5", {"start": v(764.54, 48.26) * mm, "end": v(789.94, 48.26) * mm});
            skLineSegment(sketch, "E6.180.0.5", {"start": v(642.62, 48.26) * mm, "end": v(668.02, 48.26) * mm});
            skLineSegment(sketch, "E6.183.0.5", {"start": v(520.7, 48.26) * mm, "end": v(546.1, 48.26) * mm});
            skLineSegment(sketch, "E6.186.0.5", {"start": v(398.78, 48.26) * mm, "end": v(424.18, 48.26) * mm});
            skLineSegment(sketch, "E6.189.0.5", {"start": v(668.02, 48.26) * mm, "end": v(668.02, 27.94) * mm});
            skLineSegment(sketch, "E6.192.0.5", {"start": v(546.1, 48.26) * mm, "end": v(546.1, 27.94) * mm});
            skLineSegment(sketch, "E6.195.0.5", {"start": v(424.18, 48.26) * mm, "end": v(424.18, 27.94) * mm});
            skLineSegment(sketch, "E6.198.0.5", {"start": v(789.94, 48.26) * mm, "end": v(789.94, 27.94) * mm});
            skLineSegment(sketch, "E6.201.0.5", {"start": v(764.54, 48.26) * mm, "end": v(764.54, 27.94) * mm});
            skLineSegment(sketch, "E6.204.0.5", {"start": v(642.62, 48.26) * mm, "end": v(642.62, 27.94) * mm});
            skLineSegment(sketch, "E6.207.0.5", {"start": v(520.7, 48.26) * mm, "end": v(520.7, 27.94) * mm});
            skLineSegment(sketch, "E6.210.0.5", {"start": v(398.78, 48.26) * mm, "end": v(398.78, 27.94) * mm});
            skLineSegment(sketch, "E6.213.0.5", {"start": v(332.74, 48.26) * mm, "end": v(332.74, 27.94) * mm});
            skLineSegment(sketch, "E6.216.0.5", {"start": v(210.82, 48.26) * mm, "end": v(210.82, 27.94) * mm});
            skLineSegment(sketch, "E6.219.0.5", {"start": v(88.9, 48.26) * mm, "end": v(88.9, 27.94) * mm});
            skLineSegment(sketch, "E6.222.0.5", {"start": v(33.02, 27.94) * mm, "end": v(58.42, 27.94) * mm});
            skLineSegment(sketch, "E6.225.0.5", {"start": v(154.94, 27.94) * mm, "end": v(180.34, 27.94) * mm});
            skLineSegment(sketch, "E6.228.0.5", {"start": v(276.86, 27.94) * mm, "end": v(302.26, 27.94) * mm});
            skLineSegment(sketch, "E6.231.0.5", {"start": v(307.34, 48.26) * mm, "end": v(332.74, 48.26) * mm});
            skLineSegment(sketch, "E6.234.0.5", {"start": v(185.42, 48.26) * mm, "end": v(210.82, 48.26) * mm});
            skLineSegment(sketch, "E6.237.0.5", {"start": v(63.5, 48.26) * mm, "end": v(88.9, 48.26) * mm});
            skLineSegment(sketch, "E6.240.0.5", {"start": v(307.34, 48.26) * mm, "end": v(307.34, 27.94) * mm});
            skLineSegment(sketch, "E6.243.0.5", {"start": v(185.42, 48.26) * mm, "end": v(185.42, 27.94) * mm});
            skLineSegment(sketch, "E6.246.0.5", {"start": v(63.5, 48.26) * mm, "end": v(63.5, 27.94) * mm});
            skLineSegment(sketch, "E6.249.0.5", {"start": v(307.34, 27.94) * mm, "end": v(332.74, 27.94) * mm});
            skLineSegment(sketch, "E6.252.0.5", {"start": v(185.42, 27.94) * mm, "end": v(210.82, 27.94) * mm});
            skLineSegment(sketch, "E6.255.0.5", {"start": v(63.5, 27.94) * mm, "end": v(88.9, 27.94) * mm});
            skLineSegment(sketch, "E6.258.0.5", {"start": v(363.22, 48.26) * mm, "end": v(363.22, 27.94) * mm});
            skLineSegment(sketch, "E6.261.0.5", {"start": v(241.3, 48.26) * mm, "end": v(241.3, 27.94) * mm});
            skLineSegment(sketch, "E6.264.0.5", {"start": v(119.38, 48.26) * mm, "end": v(119.38, 27.94) * mm});
            skLineSegment(sketch, "E6.267.0.5", {"start": v(337.82, 48.26) * mm, "end": v(363.22, 48.26) * mm});
            skLineSegment(sketch, "E6.270.0.5", {"start": v(215.9, 48.26) * mm, "end": v(241.3, 48.26) * mm});
            skLineSegment(sketch, "E6.273.0.5", {"start": v(93.98, 48.26) * mm, "end": v(119.38, 48.26) * mm});
            skLineSegment(sketch, "E6.276.0.5", {"start": v(337.82, 48.26) * mm, "end": v(337.82, 27.94) * mm});
            skLineSegment(sketch, "E6.279.0.5", {"start": v(215.9, 48.26) * mm, "end": v(215.9, 27.94) * mm});
            skLineSegment(sketch, "E6.282.0.5", {"start": v(93.98, 48.26) * mm, "end": v(93.98, 27.94) * mm});
            skLineSegment(sketch, "E6.285.0.5", {"start": v(93.98, 27.94) * mm, "end": v(119.38, 27.94) * mm});
            skLineSegment(sketch, "E6.288.0.5", {"start": v(337.82, 27.94) * mm, "end": v(363.22, 27.94) * mm});
            skLineSegment(sketch, "E6.291.0.5", {"start": v(215.9, 27.94) * mm, "end": v(241.3, 27.94) * mm});
            skLineSegment(sketch, "E6.294.0.5", {"start": v(149.86, 48.26) * mm, "end": v(149.86, 27.94) * mm});
            skLineSegment(sketch, "E6.297.0.5", {"start": v(27.94, 48.26) * mm, "end": v(27.94, 27.94) * mm});
            skLineSegment(sketch, "E6.300.0.5", {"start": v(271.78, 48.26) * mm, "end": v(271.78, 27.94) * mm});
            skLineSegment(sketch, "E6.303.0.5", {"start": v(124.46, 48.26) * mm, "end": v(149.86, 48.26) * mm});
            skLineSegment(sketch, "E6.306.0.5", {"start": v(2.54, 48.26) * mm, "end": v(27.94, 48.26) * mm});
            skLineSegment(sketch, "E6.309.0.5", {"start": v(246.38, 48.26) * mm, "end": v(271.78, 48.26) * mm});
            skLineSegment(sketch, "E6.312.0.5", {"start": v(124.46, 48.26) * mm, "end": v(124.46, 27.94) * mm});
            skLineSegment(sketch, "E6.315.0.5", {"start": v(2.54, 48.26) * mm, "end": v(2.54, 27.94) * mm});
            skLineSegment(sketch, "E6.318.0.5", {"start": v(368.3, 48.26) * mm, "end": v(368.3, 27.94) * mm});
            skLineSegment(sketch, "E6.321.0.5", {"start": v(246.38, 48.26) * mm, "end": v(246.38, 27.94) * mm});
            skLineSegment(sketch, "E6.324.0.5", {"start": v(124.46, 27.94) * mm, "end": v(149.86, 27.94) * mm});
            skLineSegment(sketch, "E6.327.0.5", {"start": v(2.54, 27.94) * mm, "end": v(27.94, 27.94) * mm});
            skLineSegment(sketch, "E6.330.0.5", {"start": v(246.38, 27.94) * mm, "end": v(271.78, 27.94) * mm});
            skLineSegment(sketch, "E6.333.0.5", {"start": v(276.86, 48.26) * mm, "end": v(302.26, 48.26) * mm});
            skLineSegment(sketch, "E6.336.0.5", {"start": v(154.94, 48.26) * mm, "end": v(180.34, 48.26) * mm});
            skLineSegment(sketch, "E6.339.0.5", {"start": v(33.02, 48.26) * mm, "end": v(58.42, 48.26) * mm});
            skLineSegment(sketch, "E6.342.0.5", {"start": v(180.34, 48.26) * mm, "end": v(180.34, 27.94) * mm});
            skLineSegment(sketch, "E6.345.0.5", {"start": v(58.42, 48.26) * mm, "end": v(58.42, 27.94) * mm});
            skLineSegment(sketch, "E6.348.0.5", {"start": v(302.26, 48.26) * mm, "end": v(302.26, 27.94) * mm});
            skLineSegment(sketch, "E6.351.0.5", {"start": v(276.86, 48.26) * mm, "end": v(276.86, 27.94) * mm});
            skLineSegment(sketch, "E6.354.0.5", {"start": v(154.94, 48.26) * mm, "end": v(154.94, 27.94) * mm});
            skLineSegment(sketch, "E6.357.0.5", {"start": v(33.02, 48.26) * mm, "end": v(33.02, 27.94) * mm});
            skLineSegment(sketch, "E6.360.0.5", {"start": v(-520.7, 48.26) * mm, "end": v(-520.7, 27.94) * mm});
            skLineSegment(sketch, "E6.363.0.5", {"start": v(-332.74, 27.94) * mm, "end": v(-307.34, 27.94) * mm});
            skLineSegment(sketch, "E6.366.0.5", {"start": v(-398.78, 48.26) * mm, "end": v(-398.78, 27.94) * mm});
            skLineSegment(sketch, "E6.369.0.5", {"start": v(-33.02, 48.26) * mm, "end": v(-33.02, 27.94) * mm});
            skLineSegment(sketch, "E6.372.0.5", {"start": v(-88.9, 27.94) * mm, "end": v(-63.5, 27.94) * mm});
            skLineSegment(sketch, "E6.375.0.5", {"start": v(-698.5, 27.94) * mm, "end": v(-673.1, 27.94) * mm});
            skLineSegment(sketch, "E6.378.0.5", {"start": v(-454.66, 27.94) * mm, "end": v(-429.26, 27.94) * mm});
            skLineSegment(sketch, "E6.381.0.5", {"start": v(-642.62, 48.26) * mm, "end": v(-642.62, 27.94) * mm});
            skLineSegment(sketch, "E6.384.0.5", {"start": v(-764.54, 48.26) * mm, "end": v(-764.54, 27.94) * mm});
            skLineSegment(sketch, "E6.387.0.5", {"start": v(-154.94, 48.26) * mm, "end": v(-154.94, 27.94) * mm});
            skLineSegment(sketch, "E6.390.0.5", {"start": v(-210.82, 27.94) * mm, "end": v(-185.42, 27.94) * mm});
            skLineSegment(sketch, "E6.393.0.5", {"start": v(-576.58, 27.94) * mm, "end": v(-551.18, 27.94) * mm});
            skLineSegment(sketch, "E6.396.0.5", {"start": v(-276.86, 48.26) * mm, "end": v(-276.86, 27.94) * mm});
            skLineSegment(sketch, "E6.399.0.5", {"start": v(-886.46, 27.94) * mm, "end": v(-855.98, 27.94) * mm, "construction": true});
            skLineSegment(sketch, "E6.402.0.5", {"start": v(-180.34, 48.26) * mm, "end": v(-154.94, 48.26) * mm});
            skLineSegment(sketch, "E6.405.0.5", {"start": v(-302.26, 48.26) * mm, "end": v(-276.86, 48.26) * mm});
            skLineSegment(sketch, "E6.408.0.5", {"start": v(-424.18, 48.26) * mm, "end": v(-398.78, 48.26) * mm});
            skLineSegment(sketch, "E6.411.0.5", {"start": v(-546.1, 48.26) * mm, "end": v(-520.7, 48.26) * mm});
            skLineSegment(sketch, "E6.414.0.5", {"start": v(-58.42, 48.26) * mm, "end": v(-33.02, 48.26) * mm});
            skLineSegment(sketch, "E6.417.0.5", {"start": v(-668.02, 48.26) * mm, "end": v(-642.62, 48.26) * mm});
            skLineSegment(sketch, "E6.420.0.5", {"start": v(-789.94, 48.26) * mm, "end": v(-764.54, 48.26) * mm});
            skLineSegment(sketch, "E6.423.0.5", {"start": v(-58.42, 48.26) * mm, "end": v(-58.42, 27.94) * mm});
            skLineSegment(sketch, "E6.426.0.5", {"start": v(-668.02, 48.26) * mm, "end": v(-668.02, 27.94) * mm});
            skLineSegment(sketch, "E6.429.0.5", {"start": v(-789.94, 48.26) * mm, "end": v(-789.94, 27.94) * mm});
            skLineSegment(sketch, "E6.432.0.5", {"start": v(-180.34, 48.26) * mm, "end": v(-180.34, 27.94) * mm});
            skLineSegment(sketch, "E6.435.0.5", {"start": v(-302.26, 48.26) * mm, "end": v(-302.26, 27.94) * mm});
            skLineSegment(sketch, "E6.438.0.5", {"start": v(-424.18, 48.26) * mm, "end": v(-424.18, 27.94) * mm});
            skLineSegment(sketch, "E6.441.0.5", {"start": v(-546.1, 48.26) * mm, "end": v(-546.1, 27.94) * mm});
            skLineSegment(sketch, "E6.444.0.5", {"start": v(-668.02, 27.94) * mm, "end": v(-642.62, 27.94) * mm});
            skLineSegment(sketch, "E6.447.0.5", {"start": v(-789.94, 27.94) * mm, "end": v(-764.54, 27.94) * mm});
            skLineSegment(sketch, "E6.450.0.5", {"start": v(-180.34, 27.94) * mm, "end": v(-154.94, 27.94) * mm});
            skLineSegment(sketch, "E6.453.0.5", {"start": v(-302.26, 27.94) * mm, "end": v(-276.86, 27.94) * mm});
            skLineSegment(sketch, "E6.456.0.5", {"start": v(-424.18, 27.94) * mm, "end": v(-398.78, 27.94) * mm});
            skLineSegment(sketch, "E6.459.0.5", {"start": v(-546.1, 27.94) * mm, "end": v(-520.7, 27.94) * mm});
            skLineSegment(sketch, "E6.462.0.5", {"start": v(-58.42, 27.94) * mm, "end": v(-33.02, 27.94) * mm});
            skLineSegment(sketch, "E6.465.0.5", {"start": v(-612.14, 48.26) * mm, "end": v(-612.14, 27.94) * mm});
            skLineSegment(sketch, "E6.468.0.5", {"start": v(-734.06, 48.26) * mm, "end": v(-734.06, 27.94) * mm});
            skLineSegment(sketch, "E6.471.0.5", {"start": v(-124.46, 48.26) * mm, "end": v(-124.46, 27.94) * mm});
            skLineSegment(sketch, "E6.474.0.5", {"start": v(-246.38, 48.26) * mm, "end": v(-246.38, 27.94) * mm});
            skLineSegment(sketch, "E6.477.0.5", {"start": v(-368.3, 48.26) * mm, "end": v(-368.3, 27.94) * mm});
            skLineSegment(sketch, "E6.480.0.5", {"start": v(-490.22, 48.26) * mm, "end": v(-490.22, 27.94) * mm});
            skLineSegment(sketch, "E6.483.0.5", {"start": v(-2.54, 48.26) * mm, "end": v(-2.54, 27.94) * mm});
            skLineSegment(sketch, "E6.486.0.5", {"start": v(-637.54, 48.26) * mm, "end": v(-612.14, 48.26) * mm});
            skLineSegment(sketch, "E6.489.0.5", {"start": v(-759.46, 48.26) * mm, "end": v(-734.06, 48.26) * mm});
            skLineSegment(sketch, "E6.492.0.5", {"start": v(-149.86, 48.26) * mm, "end": v(-124.46, 48.26) * mm});
            skLineSegment(sketch, "E6.495.0.5", {"start": v(-271.78, 48.26) * mm, "end": v(-246.38, 48.26) * mm});
            skLineSegment(sketch, "E6.498.0.5", {"start": v(-393.7, 48.26) * mm, "end": v(-368.3, 48.26) * mm});
            skLineSegment(sketch, "E6.501.0.5", {"start": v(-515.62, 48.26) * mm, "end": v(-490.22, 48.26) * mm});
            skLineSegment(sketch, "E6.504.0.5", {"start": v(-27.94, 48.26) * mm, "end": v(-2.54, 48.26) * mm});
            skLineSegment(sketch, "E6.507.0.5", {"start": v(-637.54, 48.26) * mm, "end": v(-637.54, 27.94) * mm});
            skLineSegment(sketch, "E6.510.0.5", {"start": v(-759.46, 48.26) * mm, "end": v(-759.46, 27.94) * mm});
            skLineSegment(sketch, "E6.513.0.5", {"start": v(-149.86, 48.26) * mm, "end": v(-149.86, 27.94) * mm});
            skLineSegment(sketch, "E6.516.0.5", {"start": v(-271.78, 48.26) * mm, "end": v(-271.78, 27.94) * mm});
            skLineSegment(sketch, "E6.519.0.5", {"start": v(-393.7, 48.26) * mm, "end": v(-393.7, 27.94) * mm});
            skLineSegment(sketch, "E6.522.0.5", {"start": v(-515.62, 48.26) * mm, "end": v(-515.62, 27.94) * mm});
            skLineSegment(sketch, "E6.525.0.5", {"start": v(-27.94, 48.26) * mm, "end": v(-27.94, 27.94) * mm});
            skLineSegment(sketch, "E6.528.0.5", {"start": v(-393.7, 27.94) * mm, "end": v(-368.3, 27.94) * mm});
            skLineSegment(sketch, "E6.531.0.5", {"start": v(-515.62, 27.94) * mm, "end": v(-490.22, 27.94) * mm});
            skLineSegment(sketch, "E6.534.0.5", {"start": v(-637.54, 27.94) * mm, "end": v(-612.14, 27.94) * mm});
            skLineSegment(sketch, "E6.537.0.5", {"start": v(-759.46, 27.94) * mm, "end": v(-734.06, 27.94) * mm});
            skLineSegment(sketch, "E6.540.0.5", {"start": v(-27.94, 27.94) * mm, "end": v(-2.54, 27.94) * mm});
            skLineSegment(sketch, "E6.543.0.5", {"start": v(-149.86, 27.94) * mm, "end": v(-124.46, 27.94) * mm});
            skLineSegment(sketch, "E6.546.0.5", {"start": v(-271.78, 27.94) * mm, "end": v(-246.38, 27.94) * mm});
            skLineSegment(sketch, "E6.549.0.5", {"start": v(-337.82, 48.26) * mm, "end": v(-337.82, 27.94) * mm});
            skLineSegment(sketch, "E6.552.0.5", {"start": v(-459.74, 48.26) * mm, "end": v(-459.74, 27.94) * mm});
            skLineSegment(sketch, "E6.555.0.5", {"start": v(-581.66, 48.26) * mm, "end": v(-581.66, 27.94) * mm});
            skLineSegment(sketch, "E6.558.0.5", {"start": v(-703.58, 48.26) * mm, "end": v(-703.58, 27.94) * mm});
            skLineSegment(sketch, "E6.561.0.5", {"start": v(-93.98, 48.26) * mm, "end": v(-93.98, 27.94) * mm});
            skLineSegment(sketch, "E6.564.0.5", {"start": v(-215.9, 48.26) * mm, "end": v(-215.9, 27.94) * mm});
            skLineSegment(sketch, "E6.567.0.5", {"start": v(-363.22, 48.26) * mm, "end": v(-337.82, 48.26) * mm});
            skLineSegment(sketch, "E6.570.0.5", {"start": v(-485.14, 48.26) * mm, "end": v(-459.74, 48.26) * mm});
            skLineSegment(sketch, "E6.573.0.5", {"start": v(-607.06, 48.26) * mm, "end": v(-581.66, 48.26) * mm});
            skLineSegment(sketch, "E6.576.0.5", {"start": v(-728.98, 48.26) * mm, "end": v(-703.58, 48.26) * mm});
            skLineSegment(sketch, "E6.579.0.5", {"start": v(-119.38, 48.26) * mm, "end": v(-93.98, 48.26) * mm});
            skLineSegment(sketch, "E6.582.0.5", {"start": v(-241.3, 48.26) * mm, "end": v(-215.9, 48.26) * mm});
            skLineSegment(sketch, "E6.585.0.5", {"start": v(-363.22, 48.26) * mm, "end": v(-363.22, 27.94) * mm});
            skLineSegment(sketch, "E6.588.0.5", {"start": v(-485.14, 48.26) * mm, "end": v(-485.14, 27.94) * mm});
            skLineSegment(sketch, "E6.591.0.5", {"start": v(-607.06, 48.26) * mm, "end": v(-607.06, 27.94) * mm});
            skLineSegment(sketch, "E6.594.0.5", {"start": v(-728.98, 48.26) * mm, "end": v(-728.98, 27.94) * mm});
            skLineSegment(sketch, "E6.597.0.5", {"start": v(-119.38, 48.26) * mm, "end": v(-119.38, 27.94) * mm});
            skLineSegment(sketch, "E6.600.0.5", {"start": v(-241.3, 48.26) * mm, "end": v(-241.3, 27.94) * mm});
            skLineSegment(sketch, "E6.603.0.5", {"start": v(-363.22, 27.94) * mm, "end": v(-337.82, 27.94) * mm});
            skLineSegment(sketch, "E6.606.0.5", {"start": v(-485.14, 27.94) * mm, "end": v(-459.74, 27.94) * mm});
            skLineSegment(sketch, "E6.609.0.5", {"start": v(-607.06, 27.94) * mm, "end": v(-581.66, 27.94) * mm});
            skLineSegment(sketch, "E6.612.0.5", {"start": v(-728.98, 27.94) * mm, "end": v(-703.58, 27.94) * mm});
            skLineSegment(sketch, "E6.615.0.5", {"start": v(-119.38, 27.94) * mm, "end": v(-93.98, 27.94) * mm});
            skLineSegment(sketch, "E6.618.0.5", {"start": v(-241.3, 27.94) * mm, "end": v(-215.9, 27.94) * mm});
            skLineSegment(sketch, "E6.621.0.5", {"start": v(-698.5, 48.26) * mm, "end": v(-673.1, 48.26) * mm});
            skLineSegment(sketch, "E6.624.0.5", {"start": v(-210.82, 48.26) * mm, "end": v(-185.42, 48.26) * mm});
            skLineSegment(sketch, "E6.627.0.5", {"start": v(-332.74, 48.26) * mm, "end": v(-307.34, 48.26) * mm});
            skLineSegment(sketch, "E6.630.0.5", {"start": v(-454.66, 48.26) * mm, "end": v(-429.26, 48.26) * mm});
            skLineSegment(sketch, "E6.633.0.5", {"start": v(-576.58, 48.26) * mm, "end": v(-551.18, 48.26) * mm});
            skLineSegment(sketch, "E6.636.0.5", {"start": v(-88.9, 48.26) * mm, "end": v(-63.5, 48.26) * mm});
            skLineSegment(sketch, "E6.639.0.5", {"start": v(-820.42, 48.26) * mm, "end": v(-795.02, 48.26) * mm});
            skLineSegment(sketch, "E6.642.0.5", {"start": v(-820.42, 48.26) * mm, "end": v(-820.42, 27.94) * mm});
            skLineSegment(sketch, "E6.645.0.5", {"start": v(-820.42, 27.94) * mm, "end": v(-795.02, 27.94) * mm});
            skLineSegment(sketch, "E6.648.0.5", {"start": v(-911.86, 48.26) * mm, "end": v(-886.46, 48.26) * mm});
            skLineSegment(sketch, "E6.651.0.5", {"start": v(-911.86, 27.94) * mm, "end": v(-886.46, 27.94) * mm});
            skLineSegment(sketch, "E6.654.0.5", {"start": v(-911.86, 48.26) * mm, "end": v(-911.86, 27.94) * mm});
            skLineSegment(sketch, "E6.657.0.5", {"start": v(-886.46, 48.26) * mm, "end": v(-886.46, 27.94) * mm});
            skLineSegment(sketch, "E6.660.0.5", {"start": v(-855.98, 48.26) * mm, "end": v(-855.98, 27.94) * mm});
            skLineSegment(sketch, "E6.663.0.5", {"start": v(-881.38, 48.26) * mm, "end": v(-855.98, 48.26) * mm});
            skLineSegment(sketch, "E6.666.0.5", {"start": v(-881.38, 48.26) * mm, "end": v(-881.38, 27.94) * mm});
            skLineSegment(sketch, "E6.669.0.5", {"start": v(-825.5, 48.26) * mm, "end": v(-825.5, 27.94) * mm});
            skLineSegment(sketch, "E6.672.0.5", {"start": v(-850.9, 48.26) * mm, "end": v(-825.5, 48.26) * mm});
            skLineSegment(sketch, "E6.675.0.5", {"start": v(-307.34, 48.26) * mm, "end": v(-307.34, 27.94) * mm});
            skLineSegment(sketch, "E6.678.0.5", {"start": v(-850.9, 48.26) * mm, "end": v(-850.9, 27.94) * mm});
            skLineSegment(sketch, "E6.681.0.5", {"start": v(-429.26, 48.26) * mm, "end": v(-429.26, 27.94) * mm});
            skLineSegment(sketch, "E6.684.0.5", {"start": v(-551.18, 48.26) * mm, "end": v(-551.18, 27.94) * mm});
            skLineSegment(sketch, "E6.687.0.5", {"start": v(-673.1, 48.26) * mm, "end": v(-673.1, 27.94) * mm});
            skLineSegment(sketch, "E6.690.0.5", {"start": v(-850.9, 27.94) * mm, "end": v(-825.5, 27.94) * mm});
            skLineSegment(sketch, "E6.693.0.5", {"start": v(-63.5, 48.26) * mm, "end": v(-63.5, 27.94) * mm});
            skLineSegment(sketch, "E6.696.0.5", {"start": v(-185.42, 48.26) * mm, "end": v(-185.42, 27.94) * mm});
            skLineSegment(sketch, "E6.699.0.5", {"start": v(-795.02, 48.26) * mm, "end": v(-795.02, 27.94) * mm});
            skLineSegment(sketch, "E6.702.0.5", {"start": v(-698.5, 48.26) * mm, "end": v(-698.5, 27.94) * mm});
            skLineSegment(sketch, "E6.705.0.5", {"start": v(-210.82, 48.26) * mm, "end": v(-210.82, 27.94) * mm});
            skLineSegment(sketch, "E6.708.0.5", {"start": v(-332.74, 48.26) * mm, "end": v(-332.74, 27.94) * mm});
            skLineSegment(sketch, "E6.711.0.5", {"start": v(-454.66, 48.26) * mm, "end": v(-454.66, 27.94) * mm});
            skLineSegment(sketch, "E6.714.0.5", {"start": v(-576.58, 48.26) * mm, "end": v(-576.58, 27.94) * mm});
            skLineSegment(sketch, "E6.717.0.5", {"start": v(-88.9, 48.26) * mm, "end": v(-88.9, 27.94) * mm});
            skLineSegment(sketch, "E6.720.0.5", {"start": v(-881.38, 27.94) * mm, "end": v(-855.98, 27.94) * mm});
            skSolve(sketch);
        }
        {
            var Q0;
            Q0 = qSketchRegion(id + "F4", true);
            extrude(context, id + "F5", {"entities" : qUnion([Q0]), "operationType" : NewBodyOperationType.REMOVE, "endBound" : BoundingType.THROUGH_ALL, "oppositeDirection" : true, "depth" : 25.4 * mm, "offsetDistance" : 25.4 * mm});
        }
        {
            var Q0;
            {var subQ0=sQuery(id+"F0.wireOp",EDGE,"E0.right");var subQ2=sQuery(id+"F0.wireOp",EDGE,"E0.left");var subQ3=sQuery(id+"F0.wireOp",EDGE,"E0.top");Q0=makeQuery(id+"F3.boolean.opBoolean","SPLIT",FACE,{"disambiguationData":[TD([makeQuery(id+"F1.opExtrude","SWEPT_FACE",FACE,{"disambiguationData":[OSD([subQ3])]})])],"derivedFrom":makeQuery(id+"F1.opExtrude","CAP_FACE",FACE,{"disambiguationData":[OSD([sQuery(id+"F0.wireOp",EDGE,"E0.bottom"),subQ3,subQ2,subQ0])],"isStart":false})});}
            var sketch = newSketch(context, id + "F6", { "sketchPlane" : qUnion([Q0])});
            skLineSegment(sketch, "E7.bottom", {"start": v(-3.18, 0) * mm, "end": v(3.17, 0) * mm});
            skLineSegment(sketch, "E7.left", {"start": v(-3.18, 0) * mm, "end": v(-3.18, -1353.82) * mm});
            skLineSegment(sketch, "E7.right", {"start": v(3.17, 0) * mm, "end": v(3.17, -1353.82) * mm});
            skPoint(sketch, "E7.middle", {"position": v(0, -1371.6) * mm});
            skLineSegment(sketch, "E8.left", {"start": v(-3.18, 0) * mm, "end": v(-3.18, 1353.82) * mm});
            skLineSegment(sketch, "E8.right", {"start": v(3.17, 0) * mm, "end": v(3.17, 1353.82) * mm});
            skLineSegment(sketch, "E9", {"start": v(-3.18, 1371.6) * mm, "end": v(3.17, 1371.6) * mm});
            skPoint(sketch, "E8.top.end.orphan", {"position": v(3.17, 1953.47) * mm});
            skPoint(sketch, "E7.top.end.orphan", {"position": v(3.18, -2743.2) * mm});
            skPoint(sketch, "E7.top.start.orphan", {"position": v(-3.17, -2743.2) * mm});
            skLineSegment(sketch, "E10.bottom", {"start": v(762, -1371.6) * mm, "end": v(-762, -1371.6) * mm});
            skLineSegment(sketch, "E10.top", {"start": v(736.6, -1353.82) * mm, "end": v(3.17, -1353.82) * mm});
            skLineSegment(sketch, "E10.left", {"start": v(762, -1371.6) * mm, "end": v(762, -1353.82) * mm});
            skLineSegment(sketch, "E10.right", {"start": v(-762, -1371.6) * mm, "end": v(-762, -1353.82) * mm});
            skPoint(sketch, "E11.orphan", {"position": v(-3.18, -1371.6) * mm});
            skPoint(sketch, "E12.orphan", {"position": v(3.18, -1371.6) * mm});
            skLineSegment(sketch, "E13.trimOffspring", {"start": v(-3.18, -1353.82) * mm, "end": v(-736.6, -1353.82) * mm});
            skLineSegment(sketch, "E14.bottom", {"start": v(-762, -1371.6) * mm, "end": v(-736.6, -1371.6) * mm});
            skLineSegment(sketch, "E14.top", {"start": v(-762, 1371.6) * mm, "end": v(-736.6, 1371.6) * mm});
            skLineSegment(sketch, "E14.left", {"start": v(-762, -1371.6) * mm, "end": v(-762, 1371.6) * mm});
            skLineSegment(sketch, "E14.right", {"start": v(-736.6, -1353.82) * mm, "end": v(-736.6, 1353.82) * mm});
            skLineSegment(sketch, "E15.bottom", {"start": v(762, -1371.6) * mm, "end": v(736.6, -1371.6) * mm});
            skLineSegment(sketch, "E15.top", {"start": v(762, 1371.6) * mm, "end": v(736.6, 1371.6) * mm});
            skLineSegment(sketch, "E15.left", {"start": v(762, -1371.6) * mm, "end": v(762, 1371.6) * mm});
            skLineSegment(sketch, "E15.right", {"start": v(736.6, -1353.82) * mm, "end": v(736.6, 1353.82) * mm});
            skLineSegment(sketch, "E16.bottom", {"start": v(-762, 1371.6) * mm, "end": v(762, 1371.6) * mm});
            skLineSegment(sketch, "E16.top", {"start": v(-736.6, 1353.82) * mm, "end": v(-3.18, 1353.82) * mm});
            skLineSegment(sketch, "E16.left", {"start": v(-762, 1371.6) * mm, "end": v(-762, 1353.82) * mm});
            skLineSegment(sketch, "E16.right", {"start": v(762, 1371.6) * mm, "end": v(762, 1353.82) * mm});
            skLineSegment(sketch, "E17.trimOffspring", {"start": v(3.17, 1353.82) * mm, "end": v(736.6, 1353.82) * mm});
            skSolve(sketch);
        }
        {
            var Q0;
            Q0=makeQuery(id+"F6.imprint","IMPRINT",FACE,{"disambiguationData":[TD([[makeQuery(id+"F6.imprint","IMPRINT",EDGE,{"derivedFrom":sQuery(id+"F6.wireOp",EDGE,"E7.bottom")}),1.0]])]});
            var Q1;
            Q1=makeQuery(id+"F6.imprint","IMPRINT",FACE,{"disambiguationData":[TD([[makeQuery(id+"F6.imprint","IMPRINT",EDGE,{"derivedFrom":sQuery(id+"F6.wireOp",EDGE,"E10.bottom")}),-1.0]])]});
            extrude(context, id + "F7", {"entities" : qUnion([Q0, Q1]), "depth" : 0.03 * mm, "offsetDistance" : 25.4 * mm});
        }
    });
